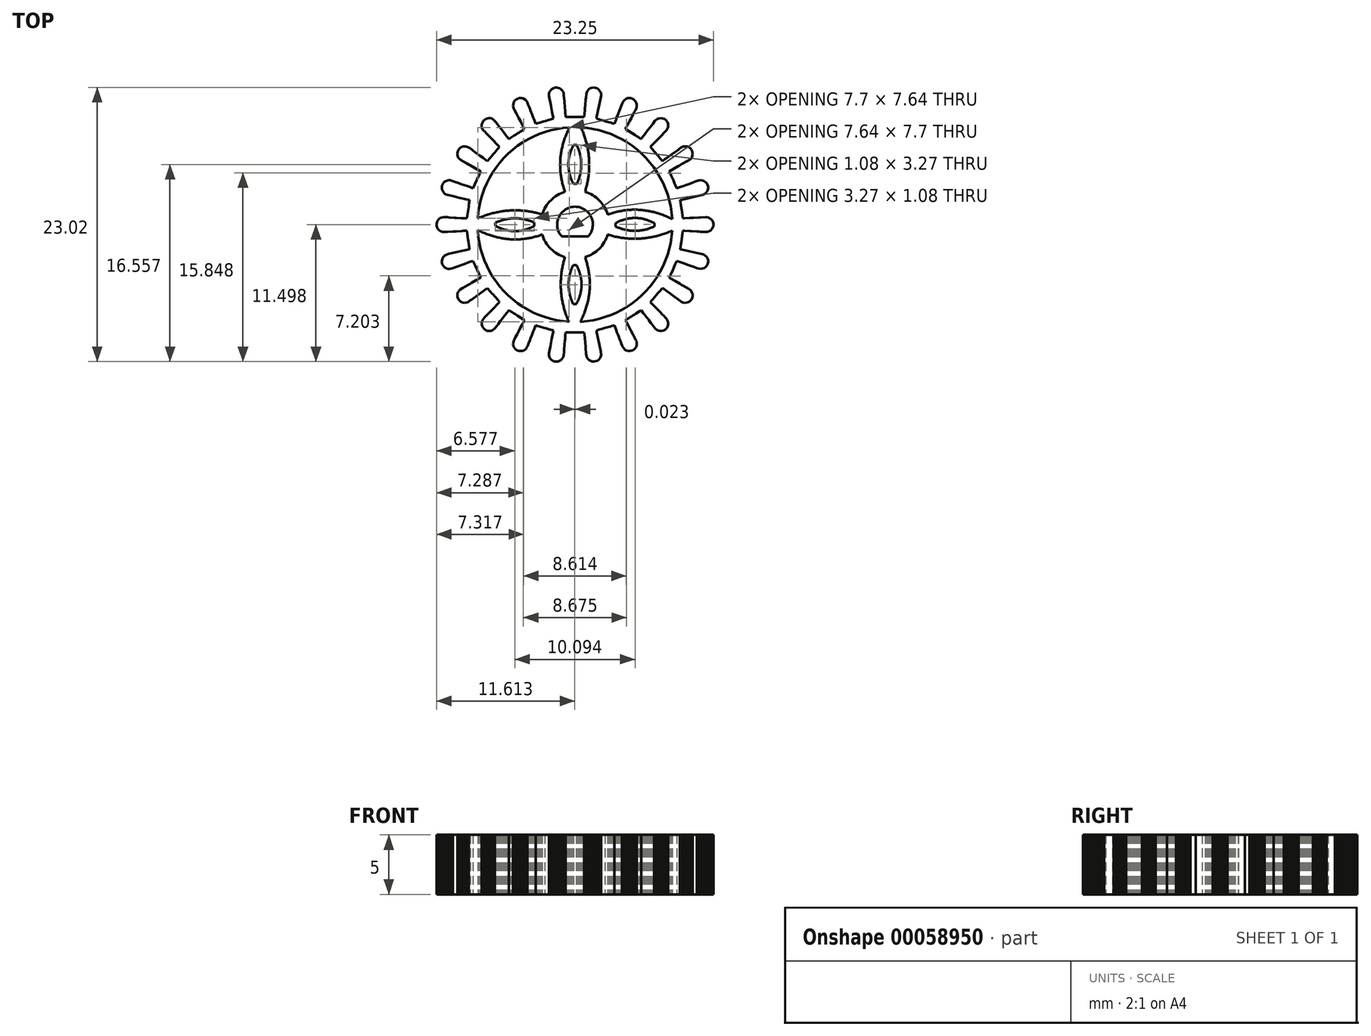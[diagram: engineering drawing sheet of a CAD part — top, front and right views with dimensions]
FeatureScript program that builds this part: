
annotation { "Feature Type Name" : "Feature", "Feature Type Description" : "" }
export const myFeature = defineFeature(function(context is Context, id is Id, definition is map)
    precondition{}
    {
        {
            var Q0;
            Q0=qCreatedBy(makeId("Top.planeOp"),FACE);
            var sketch = newSketch(context, id + "F0", { "sketchPlane" : qUnion([Q0])});
            skLineSegment(sketch, "E0", {"start": v(8.27, -0.52) * mm, "end": v(8.4, -0.52) * mm});
            skLineSegment(sketch, "E1", {"start": v(8.4, -0.52) * mm, "end": v(8.55, -0.53) * mm});
            skLineSegment(sketch, "E2", {"start": v(8.55, -0.53) * mm, "end": v(8.7, -0.54) * mm});
            skLineSegment(sketch, "E3", {"start": v(8.7, -0.54) * mm, "end": v(8.85, -0.55) * mm});
            skLineSegment(sketch, "E4", {"start": v(8.85, -0.55) * mm, "end": v(9, -0.56) * mm});
            skLineSegment(sketch, "E5", {"start": v(9, -0.56) * mm, "end": v(9.14, -0.57) * mm});
            skLineSegment(sketch, "E6", {"start": v(9.14, -0.57) * mm, "end": v(9.3, -0.57) * mm});
            skLineSegment(sketch, "E7", {"start": v(9.3, -0.57) * mm, "end": v(9.44, -0.58) * mm});
            skLineSegment(sketch, "E8", {"start": v(9.44, -0.58) * mm, "end": v(9.59, -0.6) * mm});
            skLineSegment(sketch, "E9", {"start": v(9.59, -0.6) * mm, "end": v(9.74, -0.6) * mm});
            skLineSegment(sketch, "E10", {"start": v(9.74, -0.6) * mm, "end": v(9.89, -0.6) * mm});
            skLineSegment(sketch, "E11", {"start": v(9.89, -0.6) * mm, "end": v(10.04, -0.62) * mm});
            skLineSegment(sketch, "E12", {"start": v(10.04, -0.62) * mm, "end": v(10.19, -0.63) * mm});
            skLineSegment(sketch, "E13", {"start": v(10.19, -0.63) * mm, "end": v(10.33, -0.6) * mm});
            skLineSegment(sketch, "E14", {"start": v(10.33, -0.6) * mm, "end": v(10.48, -0.56) * mm});
            skLineSegment(sketch, "E15", {"start": v(10.48, -0.56) * mm, "end": v(10.6, -0.48) * mm});
            skLineSegment(sketch, "E16", {"start": v(10.6, -0.48) * mm, "end": v(10.7, -0.37) * mm});
            skLineSegment(sketch, "E17", {"start": v(10.7, -0.37) * mm, "end": v(10.78, -0.24) * mm});
            skLineSegment(sketch, "E18", {"start": v(10.78, -0.24) * mm, "end": v(10.82, -0.1) * mm});
            skLineSegment(sketch, "E19", {"start": v(10.82, -0.1) * mm, "end": v(10.83, 0.05) * mm});
            skLineSegment(sketch, "E20", {"start": v(10.83, 0.05) * mm, "end": v(10.8, 0.2) * mm});
            skLineSegment(sketch, "E21", {"start": v(10.8, 0.2) * mm, "end": v(10.73, 0.33) * mm});
            skLineSegment(sketch, "E22", {"start": v(10.73, 0.33) * mm, "end": v(10.64, 0.45) * mm});
            skLineSegment(sketch, "E23", {"start": v(10.64, 0.45) * mm, "end": v(10.52, 0.54) * mm});
            skLineSegment(sketch, "E24", {"start": v(10.52, 0.54) * mm, "end": v(10.38, 0.6) * mm});
            skLineSegment(sketch, "E25", {"start": v(10.38, 0.6) * mm, "end": v(10.24, 0.62) * mm});
            skLineSegment(sketch, "E26", {"start": v(10.24, 0.62) * mm, "end": v(10.22, 0.62) * mm});
            skLineSegment(sketch, "E27", {"start": v(10.22, 0.62) * mm, "end": v(10.19, 0.62) * mm});
            skLineSegment(sketch, "E28", {"start": v(10.19, 0.62) * mm, "end": v(10.04, 0.62) * mm});
            skLineSegment(sketch, "E29", {"start": v(10.04, 0.62) * mm, "end": v(9.9, 0.6) * mm});
            skLineSegment(sketch, "E30", {"start": v(9.9, 0.6) * mm, "end": v(9.74, 0.6) * mm});
            skLineSegment(sketch, "E31", {"start": v(9.74, 0.6) * mm, "end": v(9.6, 0.6) * mm});
            skLineSegment(sketch, "E32", {"start": v(9.6, 0.6) * mm, "end": v(9.44, 0.58) * mm});
            skLineSegment(sketch, "E33", {"start": v(9.44, 0.58) * mm, "end": v(9.3, 0.57) * mm});
            skLineSegment(sketch, "E34", {"start": v(9.3, 0.57) * mm, "end": v(9.15, 0.57) * mm});
            skLineSegment(sketch, "E35", {"start": v(9.15, 0.57) * mm, "end": v(9, 0.56) * mm});
            skLineSegment(sketch, "E36", {"start": v(9, 0.56) * mm, "end": v(8.85, 0.55) * mm});
            skLineSegment(sketch, "E37", {"start": v(8.85, 0.55) * mm, "end": v(8.7, 0.54) * mm});
            skLineSegment(sketch, "E38", {"start": v(8.7, 0.54) * mm, "end": v(8.55, 0.53) * mm});
            skLineSegment(sketch, "E39", {"start": v(8.55, 0.53) * mm, "end": v(8.4, 0.52) * mm});
            skLineSegment(sketch, "E40", {"start": v(8.4, 0.52) * mm, "end": v(8.27, 0.52) * mm});
            skLineSegment(sketch, "E41", {"start": v(8.27, 0.52) * mm, "end": v(8.25, 0.66) * mm});
            skLineSegment(sketch, "E42", {"start": v(8.25, 0.66) * mm, "end": v(8.23, 0.8) * mm});
            skLineSegment(sketch, "E43", {"start": v(8.23, 0.8) * mm, "end": v(8.2, 0.95) * mm});
            skLineSegment(sketch, "E44", {"start": v(8.2, 0.95) * mm, "end": v(8.19, 1.1) * mm});
            skLineSegment(sketch, "E45", {"start": v(8.19, 1.1) * mm, "end": v(8.17, 1.25) * mm});
            skLineSegment(sketch, "E46", {"start": v(8.17, 1.25) * mm, "end": v(8.15, 1.4) * mm});
            skLineSegment(sketch, "E47", {"start": v(8.15, 1.4) * mm, "end": v(8.12, 1.54) * mm});
            skLineSegment(sketch, "E48", {"start": v(8.12, 1.54) * mm, "end": v(8.1, 1.69) * mm});
            skLineSegment(sketch, "E49", {"start": v(8.1, 1.69) * mm, "end": v(8.08, 1.83) * mm});
            skLineSegment(sketch, "E50", {"start": v(8.08, 1.83) * mm, "end": v(8.06, 1.98) * mm});
            skLineSegment(sketch, "E51", {"start": v(8.06, 1.98) * mm, "end": v(8.05, 2.06) * mm});
            skLineSegment(sketch, "E52", {"start": v(8.05, 2.06) * mm, "end": v(8.2, 2.1) * mm});
            skLineSegment(sketch, "E53", {"start": v(8.2, 2.1) * mm, "end": v(8.34, 2.13) * mm});
            skLineSegment(sketch, "E54", {"start": v(8.34, 2.13) * mm, "end": v(8.49, 2.16) * mm});
            skLineSegment(sketch, "E55", {"start": v(8.49, 2.16) * mm, "end": v(8.63, 2.2) * mm});
            skLineSegment(sketch, "E56", {"start": v(8.63, 2.2) * mm, "end": v(8.77, 2.23) * mm});
            skLineSegment(sketch, "E57", {"start": v(8.77, 2.23) * mm, "end": v(8.92, 2.26) * mm});
            skLineSegment(sketch, "E58", {"start": v(8.92, 2.26) * mm, "end": v(9.07, 2.3) * mm});
            skLineSegment(sketch, "E59", {"start": v(9.07, 2.3) * mm, "end": v(9.2, 2.33) * mm});
            skLineSegment(sketch, "E60", {"start": v(9.2, 2.33) * mm, "end": v(9.36, 2.36) * mm});
            skLineSegment(sketch, "E61", {"start": v(9.36, 2.36) * mm, "end": v(9.5, 2.4) * mm});
            skLineSegment(sketch, "E62", {"start": v(9.5, 2.4) * mm, "end": v(9.65, 2.43) * mm});
            skLineSegment(sketch, "E63", {"start": v(9.65, 2.43) * mm, "end": v(9.8, 2.47) * mm});
            skLineSegment(sketch, "E64", {"start": v(9.8, 2.47) * mm, "end": v(9.95, 2.5) * mm});
            skLineSegment(sketch, "E65", {"start": v(9.95, 2.5) * mm, "end": v(10.08, 2.57) * mm});
            skLineSegment(sketch, "E66", {"start": v(10.08, 2.57) * mm, "end": v(10.2, 2.66) * mm});
            skLineSegment(sketch, "E67", {"start": v(10.2, 2.66) * mm, "end": v(10.3, 2.78) * mm});
            skLineSegment(sketch, "E68", {"start": v(10.3, 2.78) * mm, "end": v(10.36, 2.91) * mm});
            skLineSegment(sketch, "E69", {"start": v(10.36, 2.91) * mm, "end": v(10.38, 3.06) * mm});
            skLineSegment(sketch, "E70", {"start": v(10.38, 3.06) * mm, "end": v(10.37, 3.21) * mm});
            skLineSegment(sketch, "E71", {"start": v(10.37, 3.21) * mm, "end": v(10.33, 3.35) * mm});
            skLineSegment(sketch, "E72", {"start": v(10.33, 3.35) * mm, "end": v(10.25, 3.48) * mm});
            skLineSegment(sketch, "E73", {"start": v(10.25, 3.48) * mm, "end": v(10.15, 3.59) * mm});
            skLineSegment(sketch, "E74", {"start": v(10.15, 3.59) * mm, "end": v(10.02, 3.67) * mm});
            skLineSegment(sketch, "E75", {"start": v(10.02, 3.67) * mm, "end": v(9.88, 3.71) * mm});
            skLineSegment(sketch, "E76", {"start": v(9.88, 3.71) * mm, "end": v(9.76, 3.72) * mm});
            skLineSegment(sketch, "E77", {"start": v(9.76, 3.72) * mm, "end": v(9.62, 3.7) * mm});
            skLineSegment(sketch, "E78", {"start": v(9.62, 3.7) * mm, "end": v(9.57, 3.7) * mm});
            skLineSegment(sketch, "E79", {"start": v(9.57, 3.7) * mm, "end": v(9.43, 3.64) * mm});
            skLineSegment(sketch, "E80", {"start": v(9.43, 3.64) * mm, "end": v(9.29, 3.6) * mm});
            skLineSegment(sketch, "E81", {"start": v(9.29, 3.6) * mm, "end": v(9.14, 3.54) * mm});
            skLineSegment(sketch, "E82", {"start": v(9.14, 3.54) * mm, "end": v(9, 3.5) * mm});
            skLineSegment(sketch, "E83", {"start": v(9, 3.5) * mm, "end": v(8.87, 3.44) * mm});
            skLineSegment(sketch, "E84", {"start": v(8.87, 3.44) * mm, "end": v(8.72, 3.4) * mm});
            skLineSegment(sketch, "E85", {"start": v(8.72, 3.4) * mm, "end": v(8.58, 3.34) * mm});
            skLineSegment(sketch, "E86", {"start": v(8.58, 3.34) * mm, "end": v(8.44, 3.3) * mm});
            skLineSegment(sketch, "E87", {"start": v(8.44, 3.3) * mm, "end": v(8.3, 3.24) * mm});
            skLineSegment(sketch, "E88", {"start": v(8.3, 3.24) * mm, "end": v(8.16, 3.2) * mm});
            skLineSegment(sketch, "E89", {"start": v(8.16, 3.2) * mm, "end": v(8.02, 3.14) * mm});
            skLineSegment(sketch, "E90", {"start": v(8.02, 3.14) * mm, "end": v(7.88, 3.1) * mm});
            skLineSegment(sketch, "E91", {"start": v(7.88, 3.1) * mm, "end": v(7.76, 3.05) * mm});
            skLineSegment(sketch, "E92", {"start": v(7.76, 3.05) * mm, "end": v(7.7, 3.18) * mm});
            skLineSegment(sketch, "E93", {"start": v(7.7, 3.18) * mm, "end": v(7.64, 3.32) * mm});
            skLineSegment(sketch, "E94", {"start": v(7.64, 3.32) * mm, "end": v(7.58, 3.45) * mm});
            skLineSegment(sketch, "E95", {"start": v(7.58, 3.45) * mm, "end": v(7.51, 3.59) * mm});
            skLineSegment(sketch, "E96", {"start": v(7.51, 3.59) * mm, "end": v(7.45, 3.72) * mm});
            skLineSegment(sketch, "E97", {"start": v(7.45, 3.72) * mm, "end": v(7.4, 3.86) * mm});
            skLineSegment(sketch, "E98", {"start": v(7.4, 3.86) * mm, "end": v(7.33, 4) * mm});
            skLineSegment(sketch, "E99", {"start": v(7.33, 4) * mm, "end": v(7.27, 4.13) * mm});
            skLineSegment(sketch, "E100", {"start": v(7.27, 4.13) * mm, "end": v(7.2, 4.26) * mm});
            skLineSegment(sketch, "E101", {"start": v(7.2, 4.26) * mm, "end": v(7.15, 4.4) * mm});
            skLineSegment(sketch, "E102", {"start": v(7.15, 4.4) * mm, "end": v(7.11, 4.47) * mm});
            skLineSegment(sketch, "E103", {"start": v(7.11, 4.47) * mm, "end": v(7.24, 4.54) * mm});
            skLineSegment(sketch, "E104", {"start": v(7.24, 4.54) * mm, "end": v(7.37, 4.61) * mm});
            skLineSegment(sketch, "E105", {"start": v(7.37, 4.61) * mm, "end": v(7.5, 4.69) * mm});
            skLineSegment(sketch, "E106", {"start": v(7.5, 4.69) * mm, "end": v(7.63, 4.76) * mm});
            skLineSegment(sketch, "E107", {"start": v(7.63, 4.76) * mm, "end": v(7.76, 4.83) * mm});
            skLineSegment(sketch, "E108", {"start": v(7.76, 4.83) * mm, "end": v(7.9, 4.9) * mm});
            skLineSegment(sketch, "E109", {"start": v(7.9, 4.9) * mm, "end": v(8.02, 4.98) * mm});
            skLineSegment(sketch, "E110", {"start": v(8.02, 4.98) * mm, "end": v(8.15, 5.05) * mm});
            skLineSegment(sketch, "E111", {"start": v(8.15, 5.05) * mm, "end": v(8.28, 5.13) * mm});
            skLineSegment(sketch, "E112", {"start": v(8.28, 5.13) * mm, "end": v(8.4, 5.2) * mm});
            skLineSegment(sketch, "E113", {"start": v(8.4, 5.2) * mm, "end": v(8.54, 5.27) * mm});
            skLineSegment(sketch, "E114", {"start": v(8.54, 5.27) * mm, "end": v(8.67, 5.35) * mm});
            skLineSegment(sketch, "E115", {"start": v(8.67, 5.35) * mm, "end": v(8.8, 5.43) * mm});
            skLineSegment(sketch, "E116", {"start": v(8.8, 5.43) * mm, "end": v(8.92, 5.53) * mm});
            skLineSegment(sketch, "E117", {"start": v(8.92, 5.53) * mm, "end": v(9, 5.65) * mm});
            skLineSegment(sketch, "E118", {"start": v(9, 5.65) * mm, "end": v(9.06, 5.79) * mm});
            skLineSegment(sketch, "E119", {"start": v(9.06, 5.79) * mm, "end": v(9.08, 5.94) * mm});
            skLineSegment(sketch, "E120", {"start": v(9.08, 5.94) * mm, "end": v(9.07, 6.08) * mm});
            skLineSegment(sketch, "E121", {"start": v(9.07, 6.08) * mm, "end": v(9.02, 6.23) * mm});
            skLineSegment(sketch, "E122", {"start": v(9.02, 6.23) * mm, "end": v(8.98, 6.28) * mm});
            skLineSegment(sketch, "E123", {"start": v(8.98, 6.28) * mm, "end": v(8.89, 6.4) * mm});
            skLineSegment(sketch, "E124", {"start": v(8.89, 6.4) * mm, "end": v(8.77, 6.49) * mm});
            skLineSegment(sketch, "E125", {"start": v(8.77, 6.49) * mm, "end": v(8.63, 6.55) * mm});
            skLineSegment(sketch, "E126", {"start": v(8.63, 6.55) * mm, "end": v(8.48, 6.57) * mm});
            skLineSegment(sketch, "E127", {"start": v(8.48, 6.57) * mm, "end": v(8.45, 6.57) * mm});
            skLineSegment(sketch, "E128", {"start": v(8.45, 6.57) * mm, "end": v(8.3, 6.55) * mm});
            skLineSegment(sketch, "E129", {"start": v(8.3, 6.55) * mm, "end": v(8.16, 6.5) * mm});
            skLineSegment(sketch, "E130", {"start": v(8.16, 6.5) * mm, "end": v(8.1, 6.46) * mm});
            skLineSegment(sketch, "E131", {"start": v(8.1, 6.46) * mm, "end": v(7.99, 6.38) * mm});
            skLineSegment(sketch, "E132", {"start": v(7.99, 6.38) * mm, "end": v(7.87, 6.29) * mm});
            skLineSegment(sketch, "E133", {"start": v(7.87, 6.29) * mm, "end": v(7.74, 6.2) * mm});
            skLineSegment(sketch, "E134", {"start": v(7.74, 6.2) * mm, "end": v(7.62, 6.11) * mm});
            skLineSegment(sketch, "E135", {"start": v(7.62, 6.11) * mm, "end": v(7.5, 6.03) * mm});
            skLineSegment(sketch, "E136", {"start": v(7.5, 6.03) * mm, "end": v(7.38, 5.94) * mm});
            skLineSegment(sketch, "E137", {"start": v(7.38, 5.94) * mm, "end": v(7.26, 5.85) * mm});
            skLineSegment(sketch, "E138", {"start": v(7.26, 5.85) * mm, "end": v(7.14, 5.76) * mm});
            skLineSegment(sketch, "E139", {"start": v(7.14, 5.76) * mm, "end": v(7.02, 5.67) * mm});
            skLineSegment(sketch, "E140", {"start": v(7.02, 5.67) * mm, "end": v(6.9, 5.59) * mm});
            skLineSegment(sketch, "E141", {"start": v(6.9, 5.59) * mm, "end": v(6.78, 5.5) * mm});
            skLineSegment(sketch, "E142", {"start": v(6.78, 5.5) * mm, "end": v(6.66, 5.41) * mm});
            skLineSegment(sketch, "E143", {"start": v(6.66, 5.41) * mm, "end": v(6.55, 5.34) * mm});
            skLineSegment(sketch, "E144", {"start": v(6.55, 5.34) * mm, "end": v(6.46, 5.45) * mm});
            skLineSegment(sketch, "E145", {"start": v(6.46, 5.45) * mm, "end": v(6.36, 5.56) * mm});
            skLineSegment(sketch, "E146", {"start": v(6.36, 5.56) * mm, "end": v(6.26, 5.67) * mm});
            skLineSegment(sketch, "E147", {"start": v(6.26, 5.67) * mm, "end": v(6.17, 5.78) * mm});
            skLineSegment(sketch, "E148", {"start": v(6.17, 5.78) * mm, "end": v(6.07, 5.9) * mm});
            skLineSegment(sketch, "E149", {"start": v(6.07, 5.9) * mm, "end": v(5.97, 6) * mm});
            skLineSegment(sketch, "E150", {"start": v(5.97, 6) * mm, "end": v(5.88, 6.12) * mm});
            skLineSegment(sketch, "E151", {"start": v(5.88, 6.12) * mm, "end": v(5.78, 6.23) * mm});
            skLineSegment(sketch, "E152", {"start": v(5.78, 6.23) * mm, "end": v(5.68, 6.34) * mm});
            skLineSegment(sketch, "E153", {"start": v(5.68, 6.34) * mm, "end": v(5.59, 6.45) * mm});
            skLineSegment(sketch, "E154", {"start": v(5.59, 6.45) * mm, "end": v(5.53, 6.52) * mm});
            skLineSegment(sketch, "E155", {"start": v(5.53, 6.52) * mm, "end": v(5.64, 6.62) * mm});
            skLineSegment(sketch, "E156", {"start": v(5.64, 6.62) * mm, "end": v(5.74, 6.73) * mm});
            skLineSegment(sketch, "E157", {"start": v(5.74, 6.73) * mm, "end": v(5.84, 6.84) * mm});
            skLineSegment(sketch, "E158", {"start": v(5.84, 6.84) * mm, "end": v(5.95, 6.94) * mm});
            skLineSegment(sketch, "E159", {"start": v(5.95, 6.94) * mm, "end": v(6.05, 7.05) * mm});
            skLineSegment(sketch, "E160", {"start": v(6.05, 7.05) * mm, "end": v(6.16, 7.16) * mm});
            skLineSegment(sketch, "E161", {"start": v(6.16, 7.16) * mm, "end": v(6.26, 7.26) * mm});
            skLineSegment(sketch, "E162", {"start": v(6.26, 7.26) * mm, "end": v(6.36, 7.37) * mm});
            skLineSegment(sketch, "E163", {"start": v(6.36, 7.37) * mm, "end": v(6.47, 7.48) * mm});
            skLineSegment(sketch, "E164", {"start": v(6.47, 7.48) * mm, "end": v(6.57, 7.58) * mm});
            skLineSegment(sketch, "E165", {"start": v(6.57, 7.58) * mm, "end": v(6.67, 7.69) * mm});
            skLineSegment(sketch, "E166", {"start": v(6.67, 7.69) * mm, "end": v(6.78, 7.8) * mm});
            skLineSegment(sketch, "E167", {"start": v(6.78, 7.8) * mm, "end": v(6.9, 7.92) * mm});
            skLineSegment(sketch, "E168", {"start": v(6.9, 7.92) * mm, "end": v(6.97, 8.04) * mm});
            skLineSegment(sketch, "E169", {"start": v(6.97, 8.04) * mm, "end": v(7.02, 8.18) * mm});
            skLineSegment(sketch, "E170", {"start": v(7.02, 8.18) * mm, "end": v(7.03, 8.33) * mm});
            skLineSegment(sketch, "E171", {"start": v(7.03, 8.33) * mm, "end": v(7.01, 8.48) * mm});
            skLineSegment(sketch, "E172", {"start": v(7.01, 8.48) * mm, "end": v(6.95, 8.62) * mm});
            skLineSegment(sketch, "E173", {"start": v(6.95, 8.62) * mm, "end": v(6.86, 8.74) * mm});
            skLineSegment(sketch, "E174", {"start": v(6.86, 8.74) * mm, "end": v(6.82, 8.79) * mm});
            skLineSegment(sketch, "E175", {"start": v(6.82, 8.79) * mm, "end": v(6.7, 8.87) * mm});
            skLineSegment(sketch, "E176", {"start": v(6.7, 8.87) * mm, "end": v(6.55, 8.92) * mm});
            skLineSegment(sketch, "E177", {"start": v(6.55, 8.92) * mm, "end": v(6.42, 8.94) * mm});
            skLineSegment(sketch, "E178", {"start": v(6.42, 8.94) * mm, "end": v(6.27, 8.92) * mm});
            skLineSegment(sketch, "E179", {"start": v(6.27, 8.92) * mm, "end": v(6.13, 8.87) * mm});
            skLineSegment(sketch, "E180", {"start": v(6.13, 8.87) * mm, "end": v(6, 8.8) * mm});
            skLineSegment(sketch, "E181", {"start": v(6, 8.8) * mm, "end": v(5.92, 8.7) * mm});
            skLineSegment(sketch, "E182", {"start": v(5.92, 8.7) * mm, "end": v(5.83, 8.6) * mm});
            skLineSegment(sketch, "E183", {"start": v(5.83, 8.6) * mm, "end": v(5.74, 8.47) * mm});
            skLineSegment(sketch, "E184", {"start": v(5.74, 8.47) * mm, "end": v(5.65, 8.35) * mm});
            skLineSegment(sketch, "E185", {"start": v(5.65, 8.35) * mm, "end": v(5.56, 8.24) * mm});
            skLineSegment(sketch, "E186", {"start": v(5.56, 8.24) * mm, "end": v(5.47, 8.12) * mm});
            skLineSegment(sketch, "E187", {"start": v(5.47, 8.12) * mm, "end": v(5.38, 8) * mm});
            skLineSegment(sketch, "E188", {"start": v(5.38, 8) * mm, "end": v(5.29, 7.88) * mm});
            skLineSegment(sketch, "E189", {"start": v(5.29, 7.88) * mm, "end": v(5.2, 7.77) * mm});
            skLineSegment(sketch, "E190", {"start": v(5.2, 7.77) * mm, "end": v(5.1, 7.65) * mm});
            skLineSegment(sketch, "E191", {"start": v(5.1, 7.65) * mm, "end": v(5.01, 7.53) * mm});
            skLineSegment(sketch, "E192", {"start": v(5.01, 7.53) * mm, "end": v(4.92, 7.41) * mm});
            skLineSegment(sketch, "E193", {"start": v(4.92, 7.41) * mm, "end": v(4.83, 7.3) * mm});
            skLineSegment(sketch, "E194", {"start": v(4.83, 7.3) * mm, "end": v(4.75, 7.2) * mm});
            skLineSegment(sketch, "E195", {"start": v(4.75, 7.2) * mm, "end": v(4.63, 7.27) * mm});
            skLineSegment(sketch, "E196", {"start": v(4.63, 7.27) * mm, "end": v(4.5, 7.35) * mm});
            skLineSegment(sketch, "E197", {"start": v(4.5, 7.35) * mm, "end": v(4.38, 7.43) * mm});
            skLineSegment(sketch, "E198", {"start": v(4.38, 7.43) * mm, "end": v(4.25, 7.51) * mm});
            skLineSegment(sketch, "E199", {"start": v(4.25, 7.51) * mm, "end": v(4.13, 7.6) * mm});
            skLineSegment(sketch, "E200", {"start": v(4.13, 7.6) * mm, "end": v(4, 7.67) * mm});
            skLineSegment(sketch, "E201", {"start": v(4, 7.67) * mm, "end": v(3.88, 7.75) * mm});
            skLineSegment(sketch, "E202", {"start": v(3.88, 7.75) * mm, "end": v(3.76, 7.83) * mm});
            skLineSegment(sketch, "E203", {"start": v(3.76, 7.83) * mm, "end": v(3.63, 7.91) * mm});
            skLineSegment(sketch, "E204", {"start": v(3.63, 7.91) * mm, "end": v(3.5, 8) * mm});
            skLineSegment(sketch, "E205", {"start": v(3.5, 8) * mm, "end": v(3.44, 8.03) * mm});
            skLineSegment(sketch, "E206", {"start": v(3.44, 8.03) * mm, "end": v(3.5, 8.16) * mm});
            skLineSegment(sketch, "E207", {"start": v(3.5, 8.16) * mm, "end": v(3.58, 8.3) * mm});
            skLineSegment(sketch, "E208", {"start": v(3.58, 8.3) * mm, "end": v(3.65, 8.43) * mm});
            skLineSegment(sketch, "E209", {"start": v(3.65, 8.43) * mm, "end": v(3.72, 8.56) * mm});
            skLineSegment(sketch, "E210", {"start": v(3.72, 8.56) * mm, "end": v(3.79, 8.7) * mm});
            skLineSegment(sketch, "E211", {"start": v(3.79, 8.7) * mm, "end": v(3.86, 8.83) * mm});
            skLineSegment(sketch, "E212", {"start": v(3.86, 8.83) * mm, "end": v(3.93, 8.96) * mm});
            skLineSegment(sketch, "E213", {"start": v(3.93, 8.96) * mm, "end": v(4, 9.09) * mm});
            skLineSegment(sketch, "E214", {"start": v(4, 9.09) * mm, "end": v(4.07, 9.22) * mm});
            skLineSegment(sketch, "E215", {"start": v(4.07, 9.22) * mm, "end": v(4.14, 9.35) * mm});
            skLineSegment(sketch, "E216", {"start": v(4.14, 9.35) * mm, "end": v(4.2, 9.48) * mm});
            skLineSegment(sketch, "E217", {"start": v(4.2, 9.48) * mm, "end": v(4.28, 9.62) * mm});
            skLineSegment(sketch, "E218", {"start": v(4.28, 9.62) * mm, "end": v(4.35, 9.76) * mm});
            skLineSegment(sketch, "E219", {"start": v(4.35, 9.76) * mm, "end": v(4.39, 9.9) * mm});
            skLineSegment(sketch, "E220", {"start": v(4.39, 9.9) * mm, "end": v(4.4, 10.05) * mm});
            skLineSegment(sketch, "E221", {"start": v(4.4, 10.05) * mm, "end": v(4.37, 10.2) * mm});
            skLineSegment(sketch, "E222", {"start": v(4.37, 10.2) * mm, "end": v(4.3, 10.34) * mm});
            skLineSegment(sketch, "E223", {"start": v(4.3, 10.34) * mm, "end": v(4.21, 10.45) * mm});
            skLineSegment(sketch, "E224", {"start": v(4.21, 10.45) * mm, "end": v(4.1, 10.54) * mm});
            skLineSegment(sketch, "E225", {"start": v(4.1, 10.54) * mm, "end": v(4.03, 10.57) * mm});
            skLineSegment(sketch, "E226", {"start": v(4.03, 10.57) * mm, "end": v(3.9, 10.62) * mm});
            skLineSegment(sketch, "E227", {"start": v(3.9, 10.62) * mm, "end": v(3.77, 10.63) * mm});
            skLineSegment(sketch, "E228", {"start": v(3.77, 10.63) * mm, "end": v(3.63, 10.61) * mm});
            skLineSegment(sketch, "E229", {"start": v(3.63, 10.61) * mm, "end": v(3.49, 10.56) * mm});
            skLineSegment(sketch, "E230", {"start": v(3.49, 10.56) * mm, "end": v(3.37, 10.48) * mm});
            skLineSegment(sketch, "E231", {"start": v(3.37, 10.48) * mm, "end": v(3.26, 10.37) * mm});
            skLineSegment(sketch, "E232", {"start": v(3.26, 10.37) * mm, "end": v(3.2, 10.25) * mm});
            skLineSegment(sketch, "E233", {"start": v(3.2, 10.25) * mm, "end": v(3.14, 10.11) * mm});
            skLineSegment(sketch, "E234", {"start": v(3.14, 10.11) * mm, "end": v(3.1, 9.97) * mm});
            skLineSegment(sketch, "E235", {"start": v(3.1, 9.97) * mm, "end": v(3.04, 9.83) * mm});
            skLineSegment(sketch, "E236", {"start": v(3.04, 9.83) * mm, "end": v(2.98, 9.7) * mm});
            skLineSegment(sketch, "E237", {"start": v(2.98, 9.7) * mm, "end": v(2.93, 9.56) * mm});
            skLineSegment(sketch, "E238", {"start": v(2.93, 9.56) * mm, "end": v(2.87, 9.42) * mm});
            skLineSegment(sketch, "E239", {"start": v(2.87, 9.42) * mm, "end": v(2.82, 9.28) * mm});
            skLineSegment(sketch, "E240", {"start": v(2.82, 9.28) * mm, "end": v(2.77, 9.14) * mm});
            skLineSegment(sketch, "E241", {"start": v(2.77, 9.14) * mm, "end": v(2.71, 9) * mm});
            skLineSegment(sketch, "E242", {"start": v(2.71, 9) * mm, "end": v(2.66, 8.86) * mm});
            skLineSegment(sketch, "E243", {"start": v(2.66, 8.86) * mm, "end": v(2.6, 8.72) * mm});
            skLineSegment(sketch, "E244", {"start": v(2.6, 8.72) * mm, "end": v(2.55, 8.58) * mm});
            skLineSegment(sketch, "E245", {"start": v(2.55, 8.58) * mm, "end": v(2.5, 8.46) * mm});
            skLineSegment(sketch, "E246", {"start": v(2.5, 8.46) * mm, "end": v(2.36, 8.5) * mm});
            skLineSegment(sketch, "E247", {"start": v(2.36, 8.5) * mm, "end": v(2.22, 8.55) * mm});
            skLineSegment(sketch, "E248", {"start": v(2.22, 8.55) * mm, "end": v(2.08, 8.59) * mm});
            skLineSegment(sketch, "E249", {"start": v(2.08, 8.59) * mm, "end": v(1.93, 8.63) * mm});
            skLineSegment(sketch, "E250", {"start": v(1.93, 8.63) * mm, "end": v(1.8, 8.67) * mm});
            skLineSegment(sketch, "E251", {"start": v(1.8, 8.67) * mm, "end": v(1.65, 8.71) * mm});
            skLineSegment(sketch, "E252", {"start": v(1.65, 8.71) * mm, "end": v(1.5, 8.75) * mm});
            skLineSegment(sketch, "E253", {"start": v(1.5, 8.75) * mm, "end": v(1.37, 8.8) * mm});
            skLineSegment(sketch, "E254", {"start": v(1.37, 8.8) * mm, "end": v(1.22, 8.84) * mm});
            skLineSegment(sketch, "E255", {"start": v(1.22, 8.84) * mm, "end": v(1.08, 8.88) * mm});
            skLineSegment(sketch, "E256", {"start": v(1.08, 8.88) * mm, "end": v(1, 8.9) * mm});
            skLineSegment(sketch, "E257", {"start": v(1, 8.9) * mm, "end": v(1.03, 9.05) * mm});
            skLineSegment(sketch, "E258", {"start": v(1.03, 9.05) * mm, "end": v(1.06, 9.2) * mm});
            skLineSegment(sketch, "E259", {"start": v(1.06, 9.2) * mm, "end": v(1.1, 9.34) * mm});
            skLineSegment(sketch, "E260", {"start": v(1.1, 9.34) * mm, "end": v(1.12, 9.49) * mm});
            skLineSegment(sketch, "E261", {"start": v(1.12, 9.49) * mm, "end": v(1.15, 9.63) * mm});
            skLineSegment(sketch, "E262", {"start": v(1.15, 9.63) * mm, "end": v(1.18, 9.78) * mm});
            skLineSegment(sketch, "E263", {"start": v(1.18, 9.78) * mm, "end": v(1.21, 9.92) * mm});
            skLineSegment(sketch, "E264", {"start": v(1.21, 9.92) * mm, "end": v(1.24, 10.07) * mm});
            skLineSegment(sketch, "E265", {"start": v(1.24, 10.07) * mm, "end": v(1.27, 10.22) * mm});
            skLineSegment(sketch, "E266", {"start": v(1.27, 10.22) * mm, "end": v(1.3, 10.36) * mm});
            skLineSegment(sketch, "E267", {"start": v(1.3, 10.36) * mm, "end": v(1.33, 10.5) * mm});
            skLineSegment(sketch, "E268", {"start": v(1.33, 10.5) * mm, "end": v(1.36, 10.66) * mm});
            skLineSegment(sketch, "E269", {"start": v(1.36, 10.66) * mm, "end": v(1.4, 10.81) * mm});
            skLineSegment(sketch, "E270", {"start": v(1.4, 10.81) * mm, "end": v(1.39, 10.96) * mm});
            skLineSegment(sketch, "E271", {"start": v(1.39, 10.96) * mm, "end": v(1.35, 11.1) * mm});
            skLineSegment(sketch, "E272", {"start": v(1.35, 11.1) * mm, "end": v(1.28, 11.24) * mm});
            skLineSegment(sketch, "E273", {"start": v(1.28, 11.24) * mm, "end": v(1.19, 11.35) * mm});
            skLineSegment(sketch, "E274", {"start": v(1.19, 11.35) * mm, "end": v(1.06, 11.44) * mm});
            skLineSegment(sketch, "E275", {"start": v(1.06, 11.44) * mm, "end": v(0.92, 11.5) * mm});
            skLineSegment(sketch, "E276", {"start": v(0.92, 11.5) * mm, "end": v(0.78, 11.51) * mm});
            skLineSegment(sketch, "E277", {"start": v(0.78, 11.51) * mm, "end": v(0.76, 11.51) * mm});
            skLineSegment(sketch, "E278", {"start": v(0.76, 11.51) * mm, "end": v(0.61, 11.5) * mm});
            skLineSegment(sketch, "E279", {"start": v(0.61, 11.5) * mm, "end": v(0.47, 11.44) * mm});
            skLineSegment(sketch, "E280", {"start": v(0.47, 11.44) * mm, "end": v(0.35, 11.35) * mm});
            skLineSegment(sketch, "E281", {"start": v(0.35, 11.35) * mm, "end": v(0.25, 11.24) * mm});
            skLineSegment(sketch, "E282", {"start": v(0.25, 11.24) * mm, "end": v(0.19, 11.1) * mm});
            skLineSegment(sketch, "E283", {"start": v(0.19, 11.1) * mm, "end": v(0.15, 10.96) * mm});
            skLineSegment(sketch, "E284", {"start": v(0.15, 10.96) * mm, "end": v(0.14, 10.81) * mm});
            skLineSegment(sketch, "E285", {"start": v(0.14, 10.81) * mm, "end": v(0.12, 10.66) * mm});
            skLineSegment(sketch, "E286", {"start": v(0.12, 10.66) * mm, "end": v(0.11, 10.51) * mm});
            skLineSegment(sketch, "E287", {"start": v(0.11, 10.51) * mm, "end": v(0.1, 10.37) * mm});
            skLineSegment(sketch, "E288", {"start": v(0.1, 10.37) * mm, "end": v(0.08, 10.22) * mm});
            skLineSegment(sketch, "E289", {"start": v(0.08, 10.22) * mm, "end": v(0.07, 10.07) * mm});
            skLineSegment(sketch, "E290", {"start": v(0.07, 10.07) * mm, "end": v(0.06, 9.92) * mm});
            skLineSegment(sketch, "E291", {"start": v(0.06, 9.92) * mm, "end": v(0.05, 9.77) * mm});
            skLineSegment(sketch, "E292", {"start": v(0.05, 9.77) * mm, "end": v(0.03, 9.62) * mm});
            skLineSegment(sketch, "E293", {"start": v(0.03, 9.62) * mm, "end": v(0.02, 9.47) * mm});
            skLineSegment(sketch, "E294", {"start": v(0.02, 9.47) * mm, "end": v(0, 9.33) * mm});
            skLineSegment(sketch, "E295", {"start": v(0, 9.33) * mm, "end": v(0, 9.18) * mm});
            skLineSegment(sketch, "E296", {"start": v(0, 9.18) * mm, "end": v(-0.02, 9.05) * mm});
            skLineSegment(sketch, "E297", {"start": v(-0.02, 9.05) * mm, "end": v(-0.16, 9.05) * mm});
            skLineSegment(sketch, "E298", {"start": v(-0.16, 9.05) * mm, "end": v(-0.31, 9.05) * mm});
            skLineSegment(sketch, "E299", {"start": v(-0.31, 9.05) * mm, "end": v(-0.46, 9.05) * mm});
            skLineSegment(sketch, "E300", {"start": v(-0.46, 9.05) * mm, "end": v(-0.6, 9.05) * mm});
            skLineSegment(sketch, "E301", {"start": v(-0.6, 9.05) * mm, "end": v(-0.76, 9.05) * mm});
            skLineSegment(sketch, "E302", {"start": v(-0.76, 9.05) * mm, "end": v(-0.9, 9.05) * mm});
            skLineSegment(sketch, "E303", {"start": v(-0.9, 9.05) * mm, "end": v(-1.05, 9.05) * mm});
            skLineSegment(sketch, "E304", {"start": v(-1.05, 9.05) * mm, "end": v(-1.2, 9.05) * mm});
            skLineSegment(sketch, "E305", {"start": v(-1.2, 9.05) * mm, "end": v(-1.35, 9.05) * mm});
            skLineSegment(sketch, "E306", {"start": v(-1.35, 9.05) * mm, "end": v(-1.5, 9.05) * mm});
            skLineSegment(sketch, "E307", {"start": v(-1.5, 9.05) * mm, "end": v(-1.58, 9.05) * mm});
            skLineSegment(sketch, "E308", {"start": v(-1.58, 9.05) * mm, "end": v(-1.59, 9.2) * mm});
            skLineSegment(sketch, "E309", {"start": v(-1.59, 9.2) * mm, "end": v(-1.6, 9.34) * mm});
            skLineSegment(sketch, "E310", {"start": v(-1.6, 9.34) * mm, "end": v(-1.61, 9.5) * mm});
            skLineSegment(sketch, "E311", {"start": v(-1.61, 9.5) * mm, "end": v(-1.63, 9.64) * mm});
            skLineSegment(sketch, "E312", {"start": v(-1.63, 9.64) * mm, "end": v(-1.64, 9.79) * mm});
            skLineSegment(sketch, "E313", {"start": v(-1.64, 9.79) * mm, "end": v(-1.65, 9.94) * mm});
            skLineSegment(sketch, "E314", {"start": v(-1.65, 9.94) * mm, "end": v(-1.67, 10.09) * mm});
            skLineSegment(sketch, "E315", {"start": v(-1.67, 10.09) * mm, "end": v(-1.68, 10.24) * mm});
            skLineSegment(sketch, "E316", {"start": v(-1.68, 10.24) * mm, "end": v(-1.7, 10.39) * mm});
            skLineSegment(sketch, "E317", {"start": v(-1.7, 10.39) * mm, "end": v(-1.7, 10.53) * mm});
            skLineSegment(sketch, "E318", {"start": v(-1.7, 10.53) * mm, "end": v(-1.72, 10.68) * mm});
            skLineSegment(sketch, "E319", {"start": v(-1.72, 10.68) * mm, "end": v(-1.73, 10.83) * mm});
            skLineSegment(sketch, "E320", {"start": v(-1.73, 10.83) * mm, "end": v(-1.74, 11) * mm});
            skLineSegment(sketch, "E321", {"start": v(-1.74, 11) * mm, "end": v(-1.79, 11.13) * mm});
            skLineSegment(sketch, "E322", {"start": v(-1.79, 11.13) * mm, "end": v(-1.86, 11.26) * mm});
            skLineSegment(sketch, "E323", {"start": v(-1.86, 11.26) * mm, "end": v(-1.97, 11.37) * mm});
            skLineSegment(sketch, "E324", {"start": v(-1.97, 11.37) * mm, "end": v(-2.1, 11.45) * mm});
            skLineSegment(sketch, "E325", {"start": v(-2.1, 11.45) * mm, "end": v(-2.23, 11.5) * mm});
            skLineSegment(sketch, "E326", {"start": v(-2.23, 11.5) * mm, "end": v(-2.35, 11.51) * mm});
            skLineSegment(sketch, "E327", {"start": v(-2.35, 11.51) * mm, "end": v(-2.45, 11.5) * mm});
            skLineSegment(sketch, "E328", {"start": v(-2.45, 11.5) * mm, "end": v(-2.6, 11.47) * mm});
            skLineSegment(sketch, "E329", {"start": v(-2.6, 11.47) * mm, "end": v(-2.73, 11.4) * mm});
            skLineSegment(sketch, "E330", {"start": v(-2.73, 11.4) * mm, "end": v(-2.83, 11.3) * mm});
            skLineSegment(sketch, "E331", {"start": v(-2.83, 11.3) * mm, "end": v(-2.92, 11.17) * mm});
            skLineSegment(sketch, "E332", {"start": v(-2.92, 11.17) * mm, "end": v(-2.97, 11.03) * mm});
            skLineSegment(sketch, "E333", {"start": v(-2.97, 11.03) * mm, "end": v(-2.99, 10.88) * mm});
            skLineSegment(sketch, "E334", {"start": v(-2.99, 10.88) * mm, "end": v(-2.98, 10.78) * mm});
            skLineSegment(sketch, "E335", {"start": v(-2.98, 10.78) * mm, "end": v(-2.95, 10.64) * mm});
            skLineSegment(sketch, "E336", {"start": v(-2.95, 10.64) * mm, "end": v(-2.92, 10.5) * mm});
            skLineSegment(sketch, "E337", {"start": v(-2.92, 10.5) * mm, "end": v(-2.89, 10.34) * mm});
            skLineSegment(sketch, "E338", {"start": v(-2.89, 10.34) * mm, "end": v(-2.86, 10.2) * mm});
            skLineSegment(sketch, "E339", {"start": v(-2.86, 10.2) * mm, "end": v(-2.83, 10.05) * mm});
            skLineSegment(sketch, "E340", {"start": v(-2.83, 10.05) * mm, "end": v(-2.8, 9.9) * mm});
            skLineSegment(sketch, "E341", {"start": v(-2.8, 9.9) * mm, "end": v(-2.77, 9.76) * mm});
            skLineSegment(sketch, "E342", {"start": v(-2.77, 9.76) * mm, "end": v(-2.74, 9.61) * mm});
            skLineSegment(sketch, "E343", {"start": v(-2.74, 9.61) * mm, "end": v(-2.71, 9.47) * mm});
            skLineSegment(sketch, "E344", {"start": v(-2.71, 9.47) * mm, "end": v(-2.68, 9.32) * mm});
            skLineSegment(sketch, "E345", {"start": v(-2.68, 9.32) * mm, "end": v(-2.65, 9.18) * mm});
            skLineSegment(sketch, "E346", {"start": v(-2.65, 9.18) * mm, "end": v(-2.62, 9.03) * mm});
            skLineSegment(sketch, "E347", {"start": v(-2.62, 9.03) * mm, "end": v(-2.6, 8.9) * mm});
            skLineSegment(sketch, "E348", {"start": v(-2.6, 8.9) * mm, "end": v(-2.74, 8.86) * mm});
            skLineSegment(sketch, "E349", {"start": v(-2.74, 8.86) * mm, "end": v(-2.88, 8.82) * mm});
            skLineSegment(sketch, "E350", {"start": v(-2.88, 8.82) * mm, "end": v(-3.02, 8.78) * mm});
            skLineSegment(sketch, "E351", {"start": v(-3.02, 8.78) * mm, "end": v(-3.16, 8.74) * mm});
            skLineSegment(sketch, "E352", {"start": v(-3.16, 8.74) * mm, "end": v(-3.3, 8.7) * mm});
            skLineSegment(sketch, "E353", {"start": v(-3.3, 8.7) * mm, "end": v(-3.45, 8.65) * mm});
            skLineSegment(sketch, "E354", {"start": v(-3.45, 8.65) * mm, "end": v(-3.6, 8.61) * mm});
            skLineSegment(sketch, "E355", {"start": v(-3.6, 8.61) * mm, "end": v(-3.73, 8.57) * mm});
            skLineSegment(sketch, "E356", {"start": v(-3.73, 8.57) * mm, "end": v(-3.87, 8.53) * mm});
            skLineSegment(sketch, "E357", {"start": v(-3.87, 8.53) * mm, "end": v(-4.02, 8.49) * mm});
            skLineSegment(sketch, "E358", {"start": v(-4.02, 8.49) * mm, "end": v(-4.1, 8.46) * mm});
            skLineSegment(sketch, "E359", {"start": v(-4.1, 8.46) * mm, "end": v(-4.15, 8.6) * mm});
            skLineSegment(sketch, "E360", {"start": v(-4.15, 8.6) * mm, "end": v(-4.2, 8.74) * mm});
            skLineSegment(sketch, "E361", {"start": v(-4.2, 8.74) * mm, "end": v(-4.26, 8.88) * mm});
            skLineSegment(sketch, "E362", {"start": v(-4.26, 8.88) * mm, "end": v(-4.3, 9.02) * mm});
            skLineSegment(sketch, "E363", {"start": v(-4.3, 9.02) * mm, "end": v(-4.36, 9.16) * mm});
            skLineSegment(sketch, "E364", {"start": v(-4.36, 9.16) * mm, "end": v(-4.42, 9.3) * mm});
            skLineSegment(sketch, "E365", {"start": v(-4.42, 9.3) * mm, "end": v(-4.47, 9.43) * mm});
            skLineSegment(sketch, "E366", {"start": v(-4.47, 9.43) * mm, "end": v(-4.53, 9.57) * mm});
            skLineSegment(sketch, "E367", {"start": v(-4.53, 9.57) * mm, "end": v(-4.58, 9.71) * mm});
            skLineSegment(sketch, "E368", {"start": v(-4.58, 9.71) * mm, "end": v(-4.63, 9.85) * mm});
            skLineSegment(sketch, "E369", {"start": v(-4.63, 9.85) * mm, "end": v(-4.69, 9.99) * mm});
            skLineSegment(sketch, "E370", {"start": v(-4.69, 9.99) * mm, "end": v(-4.74, 10.13) * mm});
            skLineSegment(sketch, "E371", {"start": v(-4.74, 10.13) * mm, "end": v(-4.8, 10.28) * mm});
            skLineSegment(sketch, "E372", {"start": v(-4.8, 10.28) * mm, "end": v(-4.89, 10.4) * mm});
            skLineSegment(sketch, "E373", {"start": v(-4.89, 10.4) * mm, "end": v(-5, 10.5) * mm});
            skLineSegment(sketch, "E374", {"start": v(-5, 10.5) * mm, "end": v(-5.12, 10.58) * mm});
            skLineSegment(sketch, "E375", {"start": v(-5.12, 10.58) * mm, "end": v(-5.27, 10.62) * mm});
            skLineSegment(sketch, "E376", {"start": v(-5.27, 10.62) * mm, "end": v(-5.37, 10.63) * mm});
            skLineSegment(sketch, "E377", {"start": v(-5.37, 10.63) * mm, "end": v(-5.51, 10.61) * mm});
            skLineSegment(sketch, "E378", {"start": v(-5.51, 10.61) * mm, "end": v(-5.62, 10.57) * mm});
            skLineSegment(sketch, "E379", {"start": v(-5.62, 10.57) * mm, "end": v(-5.75, 10.5) * mm});
            skLineSegment(sketch, "E380", {"start": v(-5.75, 10.5) * mm, "end": v(-5.86, 10.4) * mm});
            skLineSegment(sketch, "E381", {"start": v(-5.86, 10.4) * mm, "end": v(-5.93, 10.26) * mm});
            skLineSegment(sketch, "E382", {"start": v(-5.93, 10.26) * mm, "end": v(-5.98, 10.12) * mm});
            skLineSegment(sketch, "E383", {"start": v(-5.98, 10.12) * mm, "end": v(-5.99, 9.97) * mm});
            skLineSegment(sketch, "E384", {"start": v(-5.99, 9.97) * mm, "end": v(-5.96, 9.82) * mm});
            skLineSegment(sketch, "E385", {"start": v(-5.96, 9.82) * mm, "end": v(-5.93, 9.73) * mm});
            skLineSegment(sketch, "E386", {"start": v(-5.93, 9.73) * mm, "end": v(-5.86, 9.6) * mm});
            skLineSegment(sketch, "E387", {"start": v(-5.86, 9.6) * mm, "end": v(-5.79, 9.47) * mm});
            skLineSegment(sketch, "E388", {"start": v(-5.79, 9.47) * mm, "end": v(-5.72, 9.33) * mm});
            skLineSegment(sketch, "E389", {"start": v(-5.72, 9.33) * mm, "end": v(-5.65, 9.2) * mm});
            skLineSegment(sketch, "E390", {"start": v(-5.65, 9.2) * mm, "end": v(-5.58, 9.07) * mm});
            skLineSegment(sketch, "E391", {"start": v(-5.58, 9.07) * mm, "end": v(-5.5, 8.94) * mm});
            skLineSegment(sketch, "E392", {"start": v(-5.5, 8.94) * mm, "end": v(-5.44, 8.8) * mm});
            skLineSegment(sketch, "E393", {"start": v(-5.44, 8.8) * mm, "end": v(-5.37, 8.68) * mm});
            skLineSegment(sketch, "E394", {"start": v(-5.37, 8.68) * mm, "end": v(-5.3, 8.54) * mm});
            skLineSegment(sketch, "E395", {"start": v(-5.3, 8.54) * mm, "end": v(-5.23, 8.41) * mm});
            skLineSegment(sketch, "E396", {"start": v(-5.23, 8.41) * mm, "end": v(-5.16, 8.28) * mm});
            skLineSegment(sketch, "E397", {"start": v(-5.16, 8.28) * mm, "end": v(-5.1, 8.15) * mm});
            skLineSegment(sketch, "E398", {"start": v(-5.1, 8.15) * mm, "end": v(-5.03, 8.03) * mm});
            skLineSegment(sketch, "E399", {"start": v(-5.03, 8.03) * mm, "end": v(-5.16, 7.95) * mm});
            skLineSegment(sketch, "E400", {"start": v(-5.16, 7.95) * mm, "end": v(-5.28, 7.87) * mm});
            skLineSegment(sketch, "E401", {"start": v(-5.28, 7.87) * mm, "end": v(-5.4, 7.8) * mm});
            skLineSegment(sketch, "E402", {"start": v(-5.4, 7.8) * mm, "end": v(-5.53, 7.71) * mm});
            skLineSegment(sketch, "E403", {"start": v(-5.53, 7.71) * mm, "end": v(-5.65, 7.63) * mm});
            skLineSegment(sketch, "E404", {"start": v(-5.65, 7.63) * mm, "end": v(-5.78, 7.55) * mm});
            skLineSegment(sketch, "E405", {"start": v(-5.78, 7.55) * mm, "end": v(-5.9, 7.47) * mm});
            skLineSegment(sketch, "E406", {"start": v(-5.9, 7.47) * mm, "end": v(-6.03, 7.4) * mm});
            skLineSegment(sketch, "E407", {"start": v(-6.03, 7.4) * mm, "end": v(-6.15, 7.31) * mm});
            skLineSegment(sketch, "E408", {"start": v(-6.15, 7.31) * mm, "end": v(-6.28, 7.23) * mm});
            skLineSegment(sketch, "E409", {"start": v(-6.28, 7.23) * mm, "end": v(-6.34, 7.2) * mm});
            skLineSegment(sketch, "E410", {"start": v(-6.34, 7.2) * mm, "end": v(-6.43, 7.3) * mm});
            skLineSegment(sketch, "E411", {"start": v(-6.43, 7.3) * mm, "end": v(-6.52, 7.43) * mm});
            skLineSegment(sketch, "E412", {"start": v(-6.52, 7.43) * mm, "end": v(-6.62, 7.55) * mm});
            skLineSegment(sketch, "E413", {"start": v(-6.62, 7.55) * mm, "end": v(-6.7, 7.66) * mm});
            skLineSegment(sketch, "E414", {"start": v(-6.7, 7.66) * mm, "end": v(-6.8, 7.78) * mm});
            skLineSegment(sketch, "E415", {"start": v(-6.8, 7.78) * mm, "end": v(-6.9, 7.9) * mm});
            skLineSegment(sketch, "E416", {"start": v(-6.9, 7.9) * mm, "end": v(-6.98, 8.02) * mm});
            skLineSegment(sketch, "E417", {"start": v(-6.98, 8.02) * mm, "end": v(-7.07, 8.13) * mm});
            skLineSegment(sketch, "E418", {"start": v(-7.07, 8.13) * mm, "end": v(-7.16, 8.25) * mm});
            skLineSegment(sketch, "E419", {"start": v(-7.16, 8.25) * mm, "end": v(-7.25, 8.37) * mm});
            skLineSegment(sketch, "E420", {"start": v(-7.25, 8.37) * mm, "end": v(-7.34, 8.49) * mm});
            skLineSegment(sketch, "E421", {"start": v(-7.34, 8.49) * mm, "end": v(-7.44, 8.6) * mm});
            skLineSegment(sketch, "E422", {"start": v(-7.44, 8.6) * mm, "end": v(-7.54, 8.73) * mm});
            skLineSegment(sketch, "E423", {"start": v(-7.54, 8.73) * mm, "end": v(-7.65, 8.83) * mm});
            skLineSegment(sketch, "E424", {"start": v(-7.65, 8.83) * mm, "end": v(-7.78, 8.9) * mm});
            skLineSegment(sketch, "E425", {"start": v(-7.78, 8.9) * mm, "end": v(-7.93, 8.93) * mm});
            skLineSegment(sketch, "E426", {"start": v(-7.93, 8.93) * mm, "end": v(-8.01, 8.94) * mm});
            skLineSegment(sketch, "E427", {"start": v(-8.01, 8.94) * mm, "end": v(-8.16, 8.92) * mm});
            skLineSegment(sketch, "E428", {"start": v(-8.16, 8.92) * mm, "end": v(-8.3, 8.86) * mm});
            skLineSegment(sketch, "E429", {"start": v(-8.3, 8.86) * mm, "end": v(-8.4, 8.79) * mm});
            skLineSegment(sketch, "E430", {"start": v(-8.4, 8.79) * mm, "end": v(-8.5, 8.67) * mm});
            skLineSegment(sketch, "E431", {"start": v(-8.5, 8.67) * mm, "end": v(-8.58, 8.54) * mm});
            skLineSegment(sketch, "E432", {"start": v(-8.58, 8.54) * mm, "end": v(-8.62, 8.4) * mm});
            skLineSegment(sketch, "E433", {"start": v(-8.62, 8.4) * mm, "end": v(-8.62, 8.25) * mm});
            skLineSegment(sketch, "E434", {"start": v(-8.62, 8.25) * mm, "end": v(-8.59, 8.1) * mm});
            skLineSegment(sketch, "E435", {"start": v(-8.59, 8.1) * mm, "end": v(-8.52, 7.97) * mm});
            skLineSegment(sketch, "E436", {"start": v(-8.52, 7.97) * mm, "end": v(-8.46, 7.9) * mm});
            skLineSegment(sketch, "E437", {"start": v(-8.46, 7.9) * mm, "end": v(-8.36, 7.78) * mm});
            skLineSegment(sketch, "E438", {"start": v(-8.36, 7.78) * mm, "end": v(-8.25, 7.68) * mm});
            skLineSegment(sketch, "E439", {"start": v(-8.25, 7.68) * mm, "end": v(-8.15, 7.57) * mm});
            skLineSegment(sketch, "E440", {"start": v(-8.15, 7.57) * mm, "end": v(-8.05, 7.46) * mm});
            skLineSegment(sketch, "E441", {"start": v(-8.05, 7.46) * mm, "end": v(-7.94, 7.36) * mm});
            skLineSegment(sketch, "E442", {"start": v(-7.94, 7.36) * mm, "end": v(-7.84, 7.25) * mm});
            skLineSegment(sketch, "E443", {"start": v(-7.84, 7.25) * mm, "end": v(-7.73, 7.14) * mm});
            skLineSegment(sketch, "E444", {"start": v(-7.73, 7.14) * mm, "end": v(-7.63, 7.04) * mm});
            skLineSegment(sketch, "E445", {"start": v(-7.63, 7.04) * mm, "end": v(-7.52, 6.93) * mm});
            skLineSegment(sketch, "E446", {"start": v(-7.52, 6.93) * mm, "end": v(-7.42, 6.82) * mm});
            skLineSegment(sketch, "E447", {"start": v(-7.42, 6.82) * mm, "end": v(-7.32, 6.72) * mm});
            skLineSegment(sketch, "E448", {"start": v(-7.32, 6.72) * mm, "end": v(-7.21, 6.6) * mm});
            skLineSegment(sketch, "E449", {"start": v(-7.21, 6.6) * mm, "end": v(-7.12, 6.52) * mm});
            skLineSegment(sketch, "E450", {"start": v(-7.12, 6.52) * mm, "end": v(-7.22, 6.4) * mm});
            skLineSegment(sketch, "E451", {"start": v(-7.22, 6.4) * mm, "end": v(-7.32, 6.3) * mm});
            skLineSegment(sketch, "E452", {"start": v(-7.32, 6.3) * mm, "end": v(-7.41, 6.18) * mm});
            skLineSegment(sketch, "E453", {"start": v(-7.41, 6.18) * mm, "end": v(-7.51, 6.07) * mm});
            skLineSegment(sketch, "E454", {"start": v(-7.51, 6.07) * mm, "end": v(-7.6, 5.96) * mm});
            skLineSegment(sketch, "E455", {"start": v(-7.6, 5.96) * mm, "end": v(-7.7, 5.84) * mm});
            skLineSegment(sketch, "E456", {"start": v(-7.7, 5.84) * mm, "end": v(-7.8, 5.73) * mm});
            skLineSegment(sketch, "E457", {"start": v(-7.8, 5.73) * mm, "end": v(-7.9, 5.62) * mm});
            skLineSegment(sketch, "E458", {"start": v(-7.9, 5.62) * mm, "end": v(-8, 5.5) * mm});
            skLineSegment(sketch, "E459", {"start": v(-8, 5.5) * mm, "end": v(-8.1, 5.4) * mm});
            skLineSegment(sketch, "E460", {"start": v(-8.1, 5.4) * mm, "end": v(-8.15, 5.34) * mm});
            skLineSegment(sketch, "E461", {"start": v(-8.15, 5.34) * mm, "end": v(-8.26, 5.42) * mm});
            skLineSegment(sketch, "E462", {"start": v(-8.26, 5.42) * mm, "end": v(-8.38, 5.51) * mm});
            skLineSegment(sketch, "E463", {"start": v(-8.38, 5.51) * mm, "end": v(-8.5, 5.6) * mm});
            skLineSegment(sketch, "E464", {"start": v(-8.5, 5.6) * mm, "end": v(-8.63, 5.69) * mm});
            skLineSegment(sketch, "E465", {"start": v(-8.63, 5.69) * mm, "end": v(-8.75, 5.77) * mm});
            skLineSegment(sketch, "E466", {"start": v(-8.75, 5.77) * mm, "end": v(-8.87, 5.86) * mm});
            skLineSegment(sketch, "E467", {"start": v(-8.87, 5.86) * mm, "end": v(-8.99, 5.95) * mm});
            skLineSegment(sketch, "E468", {"start": v(-8.99, 5.95) * mm, "end": v(-9.1, 6.04) * mm});
            skLineSegment(sketch, "E469", {"start": v(-9.1, 6.04) * mm, "end": v(-9.23, 6.13) * mm});
            skLineSegment(sketch, "E470", {"start": v(-9.23, 6.13) * mm, "end": v(-9.35, 6.21) * mm});
            skLineSegment(sketch, "E471", {"start": v(-9.35, 6.21) * mm, "end": v(-9.47, 6.3) * mm});
            skLineSegment(sketch, "E472", {"start": v(-9.47, 6.3) * mm, "end": v(-9.6, 6.39) * mm});
            skLineSegment(sketch, "E473", {"start": v(-9.6, 6.39) * mm, "end": v(-9.72, 6.48) * mm});
            skLineSegment(sketch, "E474", {"start": v(-9.72, 6.48) * mm, "end": v(-9.86, 6.54) * mm});
            skLineSegment(sketch, "E475", {"start": v(-9.86, 6.54) * mm, "end": v(-10, 6.57) * mm});
            skLineSegment(sketch, "E476", {"start": v(-10, 6.57) * mm, "end": v(-10.04, 6.57) * mm});
            skLineSegment(sketch, "E477", {"start": v(-10.04, 6.57) * mm, "end": v(-10.19, 6.55) * mm});
            skLineSegment(sketch, "E478", {"start": v(-10.19, 6.55) * mm, "end": v(-10.33, 6.5) * mm});
            skLineSegment(sketch, "E479", {"start": v(-10.33, 6.5) * mm, "end": v(-10.45, 6.42) * mm});
            skLineSegment(sketch, "E480", {"start": v(-10.45, 6.42) * mm, "end": v(-10.56, 6.31) * mm});
            skLineSegment(sketch, "E481", {"start": v(-10.56, 6.31) * mm, "end": v(-10.58, 6.28) * mm});
            skLineSegment(sketch, "E482", {"start": v(-10.58, 6.28) * mm, "end": v(-10.64, 6.15) * mm});
            skLineSegment(sketch, "E483", {"start": v(-10.64, 6.15) * mm, "end": v(-10.67, 6) * mm});
            skLineSegment(sketch, "E484", {"start": v(-10.67, 6) * mm, "end": v(-10.67, 5.86) * mm});
            skLineSegment(sketch, "E485", {"start": v(-10.67, 5.86) * mm, "end": v(-10.63, 5.71) * mm});
            skLineSegment(sketch, "E486", {"start": v(-10.63, 5.71) * mm, "end": v(-10.55, 5.58) * mm});
            skLineSegment(sketch, "E487", {"start": v(-10.55, 5.58) * mm, "end": v(-10.45, 5.47) * mm});
            skLineSegment(sketch, "E488", {"start": v(-10.45, 5.47) * mm, "end": v(-10.37, 5.41) * mm});
            skLineSegment(sketch, "E489", {"start": v(-10.37, 5.41) * mm, "end": v(-10.24, 5.34) * mm});
            skLineSegment(sketch, "E490", {"start": v(-10.24, 5.34) * mm, "end": v(-10.12, 5.27) * mm});
            skLineSegment(sketch, "E491", {"start": v(-10.12, 5.27) * mm, "end": v(-9.98, 5.2) * mm});
            skLineSegment(sketch, "E492", {"start": v(-9.98, 5.2) * mm, "end": v(-9.85, 5.12) * mm});
            skLineSegment(sketch, "E493", {"start": v(-9.85, 5.12) * mm, "end": v(-9.73, 5.05) * mm});
            skLineSegment(sketch, "E494", {"start": v(-9.73, 5.05) * mm, "end": v(-9.6, 4.97) * mm});
            skLineSegment(sketch, "E495", {"start": v(-9.6, 4.97) * mm, "end": v(-9.46, 4.9) * mm});
            skLineSegment(sketch, "E496", {"start": v(-9.46, 4.9) * mm, "end": v(-9.34, 4.83) * mm});
            skLineSegment(sketch, "E497", {"start": v(-9.34, 4.83) * mm, "end": v(-9.2, 4.75) * mm});
            skLineSegment(sketch, "E498", {"start": v(-9.2, 4.75) * mm, "end": v(-9.08, 4.68) * mm});
            skLineSegment(sketch, "E499", {"start": v(-9.08, 4.68) * mm, "end": v(-8.95, 4.6) * mm});
            skLineSegment(sketch, "E500", {"start": v(-8.95, 4.6) * mm, "end": v(-8.81, 4.53) * mm});
            skLineSegment(sketch, "E501", {"start": v(-8.81, 4.53) * mm, "end": v(-8.7, 4.47) * mm});
            skLineSegment(sketch, "E502", {"start": v(-8.7, 4.47) * mm, "end": v(-8.76, 4.33) * mm});
            skLineSegment(sketch, "E503", {"start": v(-8.76, 4.33) * mm, "end": v(-8.83, 4.2) * mm});
            skLineSegment(sketch, "E504", {"start": v(-8.83, 4.2) * mm, "end": v(-8.89, 4.06) * mm});
            skLineSegment(sketch, "E505", {"start": v(-8.89, 4.06) * mm, "end": v(-8.95, 3.93) * mm});
            skLineSegment(sketch, "E506", {"start": v(-8.95, 3.93) * mm, "end": v(-9.01, 3.8) * mm});
            skLineSegment(sketch, "E507", {"start": v(-9.01, 3.8) * mm, "end": v(-9.07, 3.66) * mm});
            skLineSegment(sketch, "E508", {"start": v(-9.07, 3.66) * mm, "end": v(-9.13, 3.53) * mm});
            skLineSegment(sketch, "E509", {"start": v(-9.13, 3.53) * mm, "end": v(-9.2, 3.4) * mm});
            skLineSegment(sketch, "E510", {"start": v(-9.2, 3.4) * mm, "end": v(-9.26, 3.26) * mm});
            skLineSegment(sketch, "E511", {"start": v(-9.26, 3.26) * mm, "end": v(-9.32, 3.12) * mm});
            skLineSegment(sketch, "E512", {"start": v(-9.32, 3.12) * mm, "end": v(-9.35, 3.05) * mm});
            skLineSegment(sketch, "E513", {"start": v(-9.35, 3.05) * mm, "end": v(-9.5, 3.1) * mm});
            skLineSegment(sketch, "E514", {"start": v(-9.5, 3.1) * mm, "end": v(-9.63, 3.15) * mm});
            skLineSegment(sketch, "E515", {"start": v(-9.63, 3.15) * mm, "end": v(-9.77, 3.2) * mm});
            skLineSegment(sketch, "E516", {"start": v(-9.77, 3.2) * mm, "end": v(-9.91, 3.25) * mm});
            skLineSegment(sketch, "E517", {"start": v(-9.91, 3.25) * mm, "end": v(-10.05, 3.3) * mm});
            skLineSegment(sketch, "E518", {"start": v(-10.05, 3.3) * mm, "end": v(-10.2, 3.35) * mm});
            skLineSegment(sketch, "E519", {"start": v(-10.2, 3.35) * mm, "end": v(-10.33, 3.4) * mm});
            skLineSegment(sketch, "E520", {"start": v(-10.33, 3.4) * mm, "end": v(-10.47, 3.45) * mm});
            skLineSegment(sketch, "E521", {"start": v(-10.47, 3.45) * mm, "end": v(-10.62, 3.5) * mm});
            skLineSegment(sketch, "E522", {"start": v(-10.62, 3.5) * mm, "end": v(-10.75, 3.55) * mm});
            skLineSegment(sketch, "E523", {"start": v(-10.75, 3.55) * mm, "end": v(-10.9, 3.6) * mm});
            skLineSegment(sketch, "E524", {"start": v(-10.9, 3.6) * mm, "end": v(-11.04, 3.65) * mm});
            skLineSegment(sketch, "E525", {"start": v(-11.04, 3.65) * mm, "end": v(-11.19, 3.7) * mm});
            skLineSegment(sketch, "E526", {"start": v(-11.19, 3.7) * mm, "end": v(-11.34, 3.72) * mm});
            skLineSegment(sketch, "E527", {"start": v(-11.34, 3.72) * mm, "end": v(-11.35, 3.72) * mm});
            skLineSegment(sketch, "E528", {"start": v(-11.35, 3.72) * mm, "end": v(-11.5, 3.7) * mm});
            skLineSegment(sketch, "E529", {"start": v(-11.5, 3.7) * mm, "end": v(-11.64, 3.65) * mm});
            skLineSegment(sketch, "E530", {"start": v(-11.64, 3.65) * mm, "end": v(-11.76, 3.57) * mm});
            skLineSegment(sketch, "E531", {"start": v(-11.76, 3.57) * mm, "end": v(-11.86, 3.45) * mm});
            skLineSegment(sketch, "E532", {"start": v(-11.86, 3.45) * mm, "end": v(-11.93, 3.32) * mm});
            skLineSegment(sketch, "E533", {"start": v(-11.93, 3.32) * mm, "end": v(-11.95, 3.27) * mm});
            skLineSegment(sketch, "E534", {"start": v(-11.95, 3.27) * mm, "end": v(-11.97, 3.13) * mm});
            skLineSegment(sketch, "E535", {"start": v(-11.97, 3.13) * mm, "end": v(-11.96, 2.98) * mm});
            skLineSegment(sketch, "E536", {"start": v(-11.96, 2.98) * mm, "end": v(-11.92, 2.84) * mm});
            skLineSegment(sketch, "E537", {"start": v(-11.92, 2.84) * mm, "end": v(-11.84, 2.7) * mm});
            skLineSegment(sketch, "E538", {"start": v(-11.84, 2.7) * mm, "end": v(-11.73, 2.6) * mm});
            skLineSegment(sketch, "E539", {"start": v(-11.73, 2.6) * mm, "end": v(-11.6, 2.53) * mm});
            skLineSegment(sketch, "E540", {"start": v(-11.6, 2.53) * mm, "end": v(-11.5, 2.5) * mm});
            skLineSegment(sketch, "E541", {"start": v(-11.5, 2.5) * mm, "end": v(-11.37, 2.46) * mm});
            skLineSegment(sketch, "E542", {"start": v(-11.37, 2.46) * mm, "end": v(-11.22, 2.43) * mm});
            skLineSegment(sketch, "E543", {"start": v(-11.22, 2.43) * mm, "end": v(-11.07, 2.4) * mm});
            skLineSegment(sketch, "E544", {"start": v(-11.07, 2.4) * mm, "end": v(-10.93, 2.36) * mm});
            skLineSegment(sketch, "E545", {"start": v(-10.93, 2.36) * mm, "end": v(-10.79, 2.33) * mm});
            skLineSegment(sketch, "E546", {"start": v(-10.79, 2.33) * mm, "end": v(-10.64, 2.3) * mm});
            skLineSegment(sketch, "E547", {"start": v(-10.64, 2.3) * mm, "end": v(-10.5, 2.26) * mm});
            skLineSegment(sketch, "E548", {"start": v(-10.5, 2.26) * mm, "end": v(-10.35, 2.22) * mm});
            skLineSegment(sketch, "E549", {"start": v(-10.35, 2.22) * mm, "end": v(-10.2, 2.19) * mm});
            skLineSegment(sketch, "E550", {"start": v(-10.2, 2.19) * mm, "end": v(-10.06, 2.16) * mm});
            skLineSegment(sketch, "E551", {"start": v(-10.06, 2.16) * mm, "end": v(-9.91, 2.12) * mm});
            skLineSegment(sketch, "E552", {"start": v(-9.91, 2.12) * mm, "end": v(-9.77, 2.09) * mm});
            skLineSegment(sketch, "E553", {"start": v(-9.77, 2.09) * mm, "end": v(-9.64, 2.06) * mm});
            skLineSegment(sketch, "E554", {"start": v(-9.64, 2.06) * mm, "end": v(-9.66, 1.91) * mm});
            skLineSegment(sketch, "E555", {"start": v(-9.66, 1.91) * mm, "end": v(-9.68, 1.77) * mm});
            skLineSegment(sketch, "E556", {"start": v(-9.68, 1.77) * mm, "end": v(-9.7, 1.62) * mm});
            skLineSegment(sketch, "E557", {"start": v(-9.7, 1.62) * mm, "end": v(-9.73, 1.47) * mm});
            skLineSegment(sketch, "E558", {"start": v(-9.73, 1.47) * mm, "end": v(-9.75, 1.33) * mm});
            skLineSegment(sketch, "E559", {"start": v(-9.75, 1.33) * mm, "end": v(-9.77, 1.18) * mm});
            skLineSegment(sketch, "E560", {"start": v(-9.77, 1.18) * mm, "end": v(-9.79, 1.03) * mm});
            skLineSegment(sketch, "E561", {"start": v(-9.79, 1.03) * mm, "end": v(-9.81, 0.89) * mm});
            skLineSegment(sketch, "E562", {"start": v(-9.81, 0.89) * mm, "end": v(-9.83, 0.74) * mm});
            skLineSegment(sketch, "E563", {"start": v(-9.83, 0.74) * mm, "end": v(-9.85, 0.6) * mm});
            skLineSegment(sketch, "E564", {"start": v(-9.85, 0.6) * mm, "end": v(-9.86, 0.52) * mm});
            skLineSegment(sketch, "E565", {"start": v(-9.86, 0.52) * mm, "end": v(-10.01, 0.52) * mm});
            skLineSegment(sketch, "E566", {"start": v(-10.01, 0.52) * mm, "end": v(-10.16, 0.53) * mm});
            skLineSegment(sketch, "E567", {"start": v(-10.16, 0.53) * mm, "end": v(-10.31, 0.54) * mm});
            skLineSegment(sketch, "E568", {"start": v(-10.31, 0.54) * mm, "end": v(-10.46, 0.55) * mm});
            skLineSegment(sketch, "E569", {"start": v(-10.46, 0.55) * mm, "end": v(-10.6, 0.56) * mm});
            skLineSegment(sketch, "E570", {"start": v(-10.6, 0.56) * mm, "end": v(-10.76, 0.57) * mm});
            skLineSegment(sketch, "E571", {"start": v(-10.76, 0.57) * mm, "end": v(-10.9, 0.58) * mm});
            skLineSegment(sketch, "E572", {"start": v(-10.9, 0.58) * mm, "end": v(-11.05, 0.58) * mm});
            skLineSegment(sketch, "E573", {"start": v(-11.05, 0.58) * mm, "end": v(-11.2, 0.6) * mm});
            skLineSegment(sketch, "E574", {"start": v(-11.2, 0.6) * mm, "end": v(-11.35, 0.6) * mm});
            skLineSegment(sketch, "E575", {"start": v(-11.35, 0.6) * mm, "end": v(-11.5, 0.6) * mm});
            skLineSegment(sketch, "E576", {"start": v(-11.5, 0.6) * mm, "end": v(-11.65, 0.62) * mm});
            skLineSegment(sketch, "E577", {"start": v(-11.65, 0.62) * mm, "end": v(-11.81, 0.62) * mm});
            skLineSegment(sketch, "E578", {"start": v(-11.81, 0.62) * mm, "end": v(-11.96, 0.6) * mm});
            skLineSegment(sketch, "E579", {"start": v(-11.96, 0.6) * mm, "end": v(-12.1, 0.55) * mm});
            skLineSegment(sketch, "E580", {"start": v(-12.1, 0.55) * mm, "end": v(-12.22, 0.46) * mm});
            skLineSegment(sketch, "E581", {"start": v(-12.22, 0.46) * mm, "end": v(-12.32, 0.35) * mm});
            skLineSegment(sketch, "E582", {"start": v(-12.32, 0.35) * mm, "end": v(-12.38, 0.21) * mm});
            skLineSegment(sketch, "E583", {"start": v(-12.38, 0.21) * mm, "end": v(-12.42, 0.07) * mm});
            skLineSegment(sketch, "E584", {"start": v(-12.42, 0.07) * mm, "end": v(-12.41, -0.08) * mm});
            skLineSegment(sketch, "E585", {"start": v(-12.41, -0.08) * mm, "end": v(-12.38, -0.23) * mm});
            skLineSegment(sketch, "E586", {"start": v(-12.38, -0.23) * mm, "end": v(-12.3, -0.36) * mm});
            skLineSegment(sketch, "E587", {"start": v(-12.3, -0.36) * mm, "end": v(-12.2, -0.47) * mm});
            skLineSegment(sketch, "E588", {"start": v(-12.2, -0.47) * mm, "end": v(-12.08, -0.55) * mm});
            skLineSegment(sketch, "E589", {"start": v(-12.08, -0.55) * mm, "end": v(-11.94, -0.6) * mm});
            skLineSegment(sketch, "E590", {"start": v(-11.94, -0.6) * mm, "end": v(-11.8, -0.62) * mm});
            skLineSegment(sketch, "E591", {"start": v(-11.8, -0.62) * mm, "end": v(-11.65, -0.62) * mm});
            skLineSegment(sketch, "E592", {"start": v(-11.65, -0.62) * mm, "end": v(-11.5, -0.6) * mm});
            skLineSegment(sketch, "E593", {"start": v(-11.5, -0.6) * mm, "end": v(-11.36, -0.6) * mm});
            skLineSegment(sketch, "E594", {"start": v(-11.36, -0.6) * mm, "end": v(-11.2, -0.6) * mm});
            skLineSegment(sketch, "E595", {"start": v(-11.2, -0.6) * mm, "end": v(-11.06, -0.58) * mm});
            skLineSegment(sketch, "E596", {"start": v(-11.06, -0.58) * mm, "end": v(-10.9, -0.58) * mm});
            skLineSegment(sketch, "E597", {"start": v(-10.9, -0.58) * mm, "end": v(-10.76, -0.57) * mm});
            skLineSegment(sketch, "E598", {"start": v(-10.76, -0.57) * mm, "end": v(-10.6, -0.56) * mm});
            skLineSegment(sketch, "E599", {"start": v(-10.6, -0.56) * mm, "end": v(-10.46, -0.55) * mm});
            skLineSegment(sketch, "E600", {"start": v(-10.46, -0.55) * mm, "end": v(-10.31, -0.54) * mm});
            skLineSegment(sketch, "E601", {"start": v(-10.31, -0.54) * mm, "end": v(-10.16, -0.53) * mm});
            skLineSegment(sketch, "E602", {"start": v(-10.16, -0.53) * mm, "end": v(-10.02, -0.52) * mm});
            skLineSegment(sketch, "E603", {"start": v(-10.02, -0.52) * mm, "end": v(-9.86, -0.52) * mm});
            skLineSegment(sketch, "E604", {"start": v(-9.86, -0.52) * mm, "end": v(-9.84, -0.66) * mm});
            skLineSegment(sketch, "E605", {"start": v(-9.84, -0.66) * mm, "end": v(-9.82, -0.8) * mm});
            skLineSegment(sketch, "E606", {"start": v(-9.82, -0.8) * mm, "end": v(-9.8, -0.96) * mm});
            skLineSegment(sketch, "E607", {"start": v(-9.8, -0.96) * mm, "end": v(-9.78, -1.1) * mm});
            skLineSegment(sketch, "E608", {"start": v(-9.78, -1.1) * mm, "end": v(-9.76, -1.25) * mm});
            skLineSegment(sketch, "E609", {"start": v(-9.76, -1.25) * mm, "end": v(-9.74, -1.4) * mm});
            skLineSegment(sketch, "E610", {"start": v(-9.74, -1.4) * mm, "end": v(-9.72, -1.54) * mm});
            skLineSegment(sketch, "E611", {"start": v(-9.72, -1.54) * mm, "end": v(-9.7, -1.69) * mm});
            skLineSegment(sketch, "E612", {"start": v(-9.7, -1.69) * mm, "end": v(-9.67, -1.83) * mm});
            skLineSegment(sketch, "E613", {"start": v(-9.67, -1.83) * mm, "end": v(-9.65, -1.98) * mm});
            skLineSegment(sketch, "E614", {"start": v(-9.65, -1.98) * mm, "end": v(-9.64, -2.06) * mm});
            skLineSegment(sketch, "E615", {"start": v(-9.64, -2.06) * mm, "end": v(-9.79, -2.1) * mm});
            skLineSegment(sketch, "E616", {"start": v(-9.79, -2.1) * mm, "end": v(-9.93, -2.13) * mm});
            skLineSegment(sketch, "E617", {"start": v(-9.93, -2.13) * mm, "end": v(-10.08, -2.16) * mm});
            skLineSegment(sketch, "E618", {"start": v(-10.08, -2.16) * mm, "end": v(-10.22, -2.2) * mm});
            skLineSegment(sketch, "E619", {"start": v(-10.22, -2.2) * mm, "end": v(-10.37, -2.23) * mm});
            skLineSegment(sketch, "E620", {"start": v(-10.37, -2.23) * mm, "end": v(-10.51, -2.26) * mm});
            skLineSegment(sketch, "E621", {"start": v(-10.51, -2.26) * mm, "end": v(-10.66, -2.3) * mm});
            skLineSegment(sketch, "E622", {"start": v(-10.66, -2.3) * mm, "end": v(-10.8, -2.33) * mm});
            skLineSegment(sketch, "E623", {"start": v(-10.8, -2.33) * mm, "end": v(-10.95, -2.36) * mm});
            skLineSegment(sketch, "E624", {"start": v(-10.95, -2.36) * mm, "end": v(-11.1, -2.4) * mm});
            skLineSegment(sketch, "E625", {"start": v(-11.1, -2.4) * mm, "end": v(-11.24, -2.43) * mm});
            skLineSegment(sketch, "E626", {"start": v(-11.24, -2.43) * mm, "end": v(-11.38, -2.47) * mm});
            skLineSegment(sketch, "E627", {"start": v(-11.38, -2.47) * mm, "end": v(-11.54, -2.5) * mm});
            skLineSegment(sketch, "E628", {"start": v(-11.54, -2.5) * mm, "end": v(-11.67, -2.57) * mm});
            skLineSegment(sketch, "E629", {"start": v(-11.67, -2.57) * mm, "end": v(-11.8, -2.66) * mm});
            skLineSegment(sketch, "E630", {"start": v(-11.8, -2.66) * mm, "end": v(-11.88, -2.78) * mm});
            skLineSegment(sketch, "E631", {"start": v(-11.88, -2.78) * mm, "end": v(-11.95, -2.91) * mm});
            skLineSegment(sketch, "E632", {"start": v(-11.95, -2.91) * mm, "end": v(-11.97, -3.06) * mm});
            skLineSegment(sketch, "E633", {"start": v(-11.97, -3.06) * mm, "end": v(-11.97, -3.21) * mm});
            skLineSegment(sketch, "E634", {"start": v(-11.97, -3.21) * mm, "end": v(-11.92, -3.35) * mm});
            skLineSegment(sketch, "E635", {"start": v(-11.92, -3.35) * mm, "end": v(-11.84, -3.48) * mm});
            skLineSegment(sketch, "E636", {"start": v(-11.84, -3.48) * mm, "end": v(-11.74, -3.59) * mm});
            skLineSegment(sketch, "E637", {"start": v(-11.74, -3.59) * mm, "end": v(-11.61, -3.67) * mm});
            skLineSegment(sketch, "E638", {"start": v(-11.61, -3.67) * mm, "end": v(-11.47, -3.71) * mm});
            skLineSegment(sketch, "E639", {"start": v(-11.47, -3.71) * mm, "end": v(-11.32, -3.72) * mm});
            skLineSegment(sketch, "E640", {"start": v(-11.32, -3.72) * mm, "end": v(-11.18, -3.7) * mm});
            skLineSegment(sketch, "E641", {"start": v(-11.18, -3.7) * mm, "end": v(-11.04, -3.65) * mm});
            skLineSegment(sketch, "E642", {"start": v(-11.04, -3.65) * mm, "end": v(-10.9, -3.6) * mm});
            skLineSegment(sketch, "E643", {"start": v(-10.9, -3.6) * mm, "end": v(-10.76, -3.55) * mm});
            skLineSegment(sketch, "E644", {"start": v(-10.76, -3.55) * mm, "end": v(-10.62, -3.5) * mm});
            skLineSegment(sketch, "E645", {"start": v(-10.62, -3.5) * mm, "end": v(-10.48, -3.45) * mm});
            skLineSegment(sketch, "E646", {"start": v(-10.48, -3.45) * mm, "end": v(-10.34, -3.4) * mm});
            skLineSegment(sketch, "E647", {"start": v(-10.34, -3.4) * mm, "end": v(-10.2, -3.35) * mm});
            skLineSegment(sketch, "E648", {"start": v(-10.2, -3.35) * mm, "end": v(-10.05, -3.3) * mm});
            skLineSegment(sketch, "E649", {"start": v(-10.05, -3.3) * mm, "end": v(-9.92, -3.25) * mm});
            skLineSegment(sketch, "E650", {"start": v(-9.92, -3.25) * mm, "end": v(-9.77, -3.2) * mm});
            skLineSegment(sketch, "E651", {"start": v(-9.77, -3.2) * mm, "end": v(-9.63, -3.15) * mm});
            skLineSegment(sketch, "E652", {"start": v(-9.63, -3.15) * mm, "end": v(-9.5, -3.1) * mm});
            skLineSegment(sketch, "E653", {"start": v(-9.5, -3.1) * mm, "end": v(-9.35, -3.05) * mm});
            skLineSegment(sketch, "E654", {"start": v(-9.35, -3.05) * mm, "end": v(-9.29, -3.18) * mm});
            skLineSegment(sketch, "E655", {"start": v(-9.29, -3.18) * mm, "end": v(-9.23, -3.32) * mm});
            skLineSegment(sketch, "E656", {"start": v(-9.23, -3.32) * mm, "end": v(-9.17, -3.45) * mm});
            skLineSegment(sketch, "E657", {"start": v(-9.17, -3.45) * mm, "end": v(-9.1, -3.59) * mm});
            skLineSegment(sketch, "E658", {"start": v(-9.1, -3.59) * mm, "end": v(-9.04, -3.72) * mm});
            skLineSegment(sketch, "E659", {"start": v(-9.04, -3.72) * mm, "end": v(-8.98, -3.86) * mm});
            skLineSegment(sketch, "E660", {"start": v(-8.98, -3.86) * mm, "end": v(-8.92, -4) * mm});
            skLineSegment(sketch, "E661", {"start": v(-8.92, -4) * mm, "end": v(-8.86, -4.13) * mm});
            skLineSegment(sketch, "E662", {"start": v(-8.86, -4.13) * mm, "end": v(-8.8, -4.26) * mm});
            skLineSegment(sketch, "E663", {"start": v(-8.8, -4.26) * mm, "end": v(-8.74, -4.4) * mm});
            skLineSegment(sketch, "E664", {"start": v(-8.74, -4.4) * mm, "end": v(-8.7, -4.47) * mm});
            skLineSegment(sketch, "E665", {"start": v(-8.7, -4.47) * mm, "end": v(-8.83, -4.54) * mm});
            skLineSegment(sketch, "E666", {"start": v(-8.83, -4.54) * mm, "end": v(-8.96, -4.61) * mm});
            skLineSegment(sketch, "E667", {"start": v(-8.96, -4.61) * mm, "end": v(-9.1, -4.69) * mm});
            skLineSegment(sketch, "E668", {"start": v(-9.1, -4.69) * mm, "end": v(-9.22, -4.76) * mm});
            skLineSegment(sketch, "E669", {"start": v(-9.22, -4.76) * mm, "end": v(-9.35, -4.83) * mm});
            skLineSegment(sketch, "E670", {"start": v(-9.35, -4.83) * mm, "end": v(-9.48, -4.9) * mm});
            skLineSegment(sketch, "E671", {"start": v(-9.48, -4.9) * mm, "end": v(-9.61, -4.98) * mm});
            skLineSegment(sketch, "E672", {"start": v(-9.61, -4.98) * mm, "end": v(-9.74, -5.05) * mm});
            skLineSegment(sketch, "E673", {"start": v(-9.74, -5.05) * mm, "end": v(-9.87, -5.13) * mm});
            skLineSegment(sketch, "E674", {"start": v(-9.87, -5.13) * mm, "end": v(-10, -5.2) * mm});
            skLineSegment(sketch, "E675", {"start": v(-10, -5.2) * mm, "end": v(-10.13, -5.27) * mm});
            skLineSegment(sketch, "E676", {"start": v(-10.13, -5.27) * mm, "end": v(-10.26, -5.35) * mm});
            skLineSegment(sketch, "E677", {"start": v(-10.26, -5.35) * mm, "end": v(-10.4, -5.43) * mm});
            skLineSegment(sketch, "E678", {"start": v(-10.4, -5.43) * mm, "end": v(-10.51, -5.53) * mm});
            skLineSegment(sketch, "E679", {"start": v(-10.51, -5.53) * mm, "end": v(-10.6, -5.65) * mm});
            skLineSegment(sketch, "E680", {"start": v(-10.6, -5.65) * mm, "end": v(-10.65, -5.79) * mm});
            skLineSegment(sketch, "E681", {"start": v(-10.65, -5.79) * mm, "end": v(-10.67, -5.94) * mm});
            skLineSegment(sketch, "E682", {"start": v(-10.67, -5.94) * mm, "end": v(-10.66, -6.08) * mm});
            skLineSegment(sketch, "E683", {"start": v(-10.66, -6.08) * mm, "end": v(-10.6, -6.23) * mm});
            skLineSegment(sketch, "E684", {"start": v(-10.6, -6.23) * mm, "end": v(-10.58, -6.29) * mm});
            skLineSegment(sketch, "E685", {"start": v(-10.58, -6.29) * mm, "end": v(-10.48, -6.4) * mm});
            skLineSegment(sketch, "E686", {"start": v(-10.48, -6.4) * mm, "end": v(-10.36, -6.49) * mm});
            skLineSegment(sketch, "E687", {"start": v(-10.36, -6.49) * mm, "end": v(-10.22, -6.55) * mm});
            skLineSegment(sketch, "E688", {"start": v(-10.22, -6.55) * mm, "end": v(-10.07, -6.57) * mm});
            skLineSegment(sketch, "E689", {"start": v(-10.07, -6.57) * mm, "end": v(-9.93, -6.56) * mm});
            skLineSegment(sketch, "E690", {"start": v(-9.93, -6.56) * mm, "end": v(-9.78, -6.51) * mm});
            skLineSegment(sketch, "E691", {"start": v(-9.78, -6.51) * mm, "end": v(-9.7, -6.46) * mm});
            skLineSegment(sketch, "E692", {"start": v(-9.7, -6.46) * mm, "end": v(-9.58, -6.38) * mm});
            skLineSegment(sketch, "E693", {"start": v(-9.58, -6.38) * mm, "end": v(-9.46, -6.29) * mm});
            skLineSegment(sketch, "E694", {"start": v(-9.46, -6.29) * mm, "end": v(-9.33, -6.2) * mm});
            skLineSegment(sketch, "E695", {"start": v(-9.33, -6.2) * mm, "end": v(-9.22, -6.11) * mm});
            skLineSegment(sketch, "E696", {"start": v(-9.22, -6.11) * mm, "end": v(-9.1, -6.03) * mm});
            skLineSegment(sketch, "E697", {"start": v(-9.1, -6.03) * mm, "end": v(-8.97, -5.94) * mm});
            skLineSegment(sketch, "E698", {"start": v(-8.97, -5.94) * mm, "end": v(-8.85, -5.85) * mm});
            skLineSegment(sketch, "E699", {"start": v(-8.85, -5.85) * mm, "end": v(-8.73, -5.76) * mm});
            skLineSegment(sketch, "E700", {"start": v(-8.73, -5.76) * mm, "end": v(-8.61, -5.67) * mm});
            skLineSegment(sketch, "E701", {"start": v(-8.61, -5.67) * mm, "end": v(-8.5, -5.59) * mm});
            skLineSegment(sketch, "E702", {"start": v(-8.5, -5.59) * mm, "end": v(-8.37, -5.5) * mm});
            skLineSegment(sketch, "E703", {"start": v(-8.37, -5.5) * mm, "end": v(-8.25, -5.41) * mm});
            skLineSegment(sketch, "E704", {"start": v(-8.25, -5.41) * mm, "end": v(-8.15, -5.34) * mm});
            skLineSegment(sketch, "E705", {"start": v(-8.15, -5.34) * mm, "end": v(-8.05, -5.45) * mm});
            skLineSegment(sketch, "E706", {"start": v(-8.05, -5.45) * mm, "end": v(-7.95, -5.56) * mm});
            skLineSegment(sketch, "E707", {"start": v(-7.95, -5.56) * mm, "end": v(-7.85, -5.67) * mm});
            skLineSegment(sketch, "E708", {"start": v(-7.85, -5.67) * mm, "end": v(-7.76, -5.78) * mm});
            skLineSegment(sketch, "E709", {"start": v(-7.76, -5.78) * mm, "end": v(-7.66, -5.9) * mm});
            skLineSegment(sketch, "E710", {"start": v(-7.66, -5.9) * mm, "end": v(-7.56, -6) * mm});
            skLineSegment(sketch, "E711", {"start": v(-7.56, -6) * mm, "end": v(-7.47, -6.12) * mm});
            skLineSegment(sketch, "E712", {"start": v(-7.47, -6.12) * mm, "end": v(-7.37, -6.23) * mm});
            skLineSegment(sketch, "E713", {"start": v(-7.37, -6.23) * mm, "end": v(-7.27, -6.34) * mm});
            skLineSegment(sketch, "E714", {"start": v(-7.27, -6.34) * mm, "end": v(-7.18, -6.45) * mm});
            skLineSegment(sketch, "E715", {"start": v(-7.18, -6.45) * mm, "end": v(-7.12, -6.52) * mm});
            skLineSegment(sketch, "E716", {"start": v(-7.12, -6.52) * mm, "end": v(-7.23, -6.62) * mm});
            skLineSegment(sketch, "E717", {"start": v(-7.23, -6.62) * mm, "end": v(-7.33, -6.73) * mm});
            skLineSegment(sketch, "E718", {"start": v(-7.33, -6.73) * mm, "end": v(-7.44, -6.84) * mm});
            skLineSegment(sketch, "E719", {"start": v(-7.44, -6.84) * mm, "end": v(-7.54, -6.94) * mm});
            skLineSegment(sketch, "E720", {"start": v(-7.54, -6.94) * mm, "end": v(-7.64, -7.05) * mm});
            skLineSegment(sketch, "E721", {"start": v(-7.64, -7.05) * mm, "end": v(-7.75, -7.16) * mm});
            skLineSegment(sketch, "E722", {"start": v(-7.75, -7.16) * mm, "end": v(-7.85, -7.26) * mm});
            skLineSegment(sketch, "E723", {"start": v(-7.85, -7.26) * mm, "end": v(-7.95, -7.37) * mm});
            skLineSegment(sketch, "E724", {"start": v(-7.95, -7.37) * mm, "end": v(-8.06, -7.48) * mm});
            skLineSegment(sketch, "E725", {"start": v(-8.06, -7.48) * mm, "end": v(-8.16, -7.58) * mm});
            skLineSegment(sketch, "E726", {"start": v(-8.16, -7.58) * mm, "end": v(-8.27, -7.7) * mm});
            skLineSegment(sketch, "E727", {"start": v(-8.27, -7.7) * mm, "end": v(-8.37, -7.8) * mm});
            skLineSegment(sketch, "E728", {"start": v(-8.37, -7.8) * mm, "end": v(-8.48, -7.92) * mm});
            skLineSegment(sketch, "E729", {"start": v(-8.48, -7.92) * mm, "end": v(-8.56, -8.04) * mm});
            skLineSegment(sketch, "E730", {"start": v(-8.56, -8.04) * mm, "end": v(-8.61, -8.18) * mm});
            skLineSegment(sketch, "E731", {"start": v(-8.61, -8.18) * mm, "end": v(-8.62, -8.33) * mm});
            skLineSegment(sketch, "E732", {"start": v(-8.62, -8.33) * mm, "end": v(-8.6, -8.48) * mm});
            skLineSegment(sketch, "E733", {"start": v(-8.6, -8.48) * mm, "end": v(-8.54, -8.62) * mm});
            skLineSegment(sketch, "E734", {"start": v(-8.54, -8.62) * mm, "end": v(-8.46, -8.74) * mm});
            skLineSegment(sketch, "E735", {"start": v(-8.46, -8.74) * mm, "end": v(-8.4, -8.79) * mm});
            skLineSegment(sketch, "E736", {"start": v(-8.4, -8.79) * mm, "end": v(-8.28, -8.87) * mm});
            skLineSegment(sketch, "E737", {"start": v(-8.28, -8.87) * mm, "end": v(-8.14, -8.92) * mm});
            skLineSegment(sketch, "E738", {"start": v(-8.14, -8.92) * mm, "end": v(-8, -8.94) * mm});
            skLineSegment(sketch, "E739", {"start": v(-8, -8.94) * mm, "end": v(-7.85, -8.92) * mm});
            skLineSegment(sketch, "E740", {"start": v(-7.85, -8.92) * mm, "end": v(-7.7, -8.87) * mm});
            skLineSegment(sketch, "E741", {"start": v(-7.7, -8.87) * mm, "end": v(-7.58, -8.78) * mm});
            skLineSegment(sketch, "E742", {"start": v(-7.58, -8.78) * mm, "end": v(-7.52, -8.7) * mm});
            skLineSegment(sketch, "E743", {"start": v(-7.52, -8.7) * mm, "end": v(-7.42, -8.6) * mm});
            skLineSegment(sketch, "E744", {"start": v(-7.42, -8.6) * mm, "end": v(-7.33, -8.48) * mm});
            skLineSegment(sketch, "E745", {"start": v(-7.33, -8.48) * mm, "end": v(-7.24, -8.36) * mm});
            skLineSegment(sketch, "E746", {"start": v(-7.24, -8.36) * mm, "end": v(-7.15, -8.24) * mm});
            skLineSegment(sketch, "E747", {"start": v(-7.15, -8.24) * mm, "end": v(-7.06, -8.12) * mm});
            skLineSegment(sketch, "E748", {"start": v(-7.06, -8.12) * mm, "end": v(-6.97, -8) * mm});
            skLineSegment(sketch, "E749", {"start": v(-6.97, -8) * mm, "end": v(-6.88, -7.88) * mm});
            skLineSegment(sketch, "E750", {"start": v(-6.88, -7.88) * mm, "end": v(-6.79, -7.77) * mm});
            skLineSegment(sketch, "E751", {"start": v(-6.79, -7.77) * mm, "end": v(-6.7, -7.65) * mm});
            skLineSegment(sketch, "E752", {"start": v(-6.7, -7.65) * mm, "end": v(-6.6, -7.53) * mm});
            skLineSegment(sketch, "E753", {"start": v(-6.6, -7.53) * mm, "end": v(-6.51, -7.41) * mm});
            skLineSegment(sketch, "E754", {"start": v(-6.51, -7.41) * mm, "end": v(-6.42, -7.3) * mm});
            skLineSegment(sketch, "E755", {"start": v(-6.42, -7.3) * mm, "end": v(-6.34, -7.2) * mm});
            skLineSegment(sketch, "E756", {"start": v(-6.34, -7.2) * mm, "end": v(-6.22, -7.27) * mm});
            skLineSegment(sketch, "E757", {"start": v(-6.22, -7.27) * mm, "end": v(-6.1, -7.35) * mm});
            skLineSegment(sketch, "E758", {"start": v(-6.1, -7.35) * mm, "end": v(-5.97, -7.43) * mm});
            skLineSegment(sketch, "E759", {"start": v(-5.97, -7.43) * mm, "end": v(-5.85, -7.51) * mm});
            skLineSegment(sketch, "E760", {"start": v(-5.85, -7.51) * mm, "end": v(-5.72, -7.6) * mm});
            skLineSegment(sketch, "E761", {"start": v(-5.72, -7.6) * mm, "end": v(-5.6, -7.67) * mm});
            skLineSegment(sketch, "E762", {"start": v(-5.6, -7.67) * mm, "end": v(-5.47, -7.75) * mm});
            skLineSegment(sketch, "E763", {"start": v(-5.47, -7.75) * mm, "end": v(-5.35, -7.83) * mm});
            skLineSegment(sketch, "E764", {"start": v(-5.35, -7.83) * mm, "end": v(-5.22, -7.91) * mm});
            skLineSegment(sketch, "E765", {"start": v(-5.22, -7.91) * mm, "end": v(-5.1, -8) * mm});
            skLineSegment(sketch, "E766", {"start": v(-5.1, -8) * mm, "end": v(-5.03, -8.03) * mm});
            skLineSegment(sketch, "E767", {"start": v(-5.03, -8.03) * mm, "end": v(-5.1, -8.17) * mm});
            skLineSegment(sketch, "E768", {"start": v(-5.1, -8.17) * mm, "end": v(-5.17, -8.3) * mm});
            skLineSegment(sketch, "E769", {"start": v(-5.17, -8.3) * mm, "end": v(-5.24, -8.43) * mm});
            skLineSegment(sketch, "E770", {"start": v(-5.24, -8.43) * mm, "end": v(-5.3, -8.56) * mm});
            skLineSegment(sketch, "E771", {"start": v(-5.3, -8.56) * mm, "end": v(-5.38, -8.7) * mm});
            skLineSegment(sketch, "E772", {"start": v(-5.38, -8.7) * mm, "end": v(-5.45, -8.83) * mm});
            skLineSegment(sketch, "E773", {"start": v(-5.45, -8.83) * mm, "end": v(-5.52, -8.96) * mm});
            skLineSegment(sketch, "E774", {"start": v(-5.52, -8.96) * mm, "end": v(-5.59, -9.09) * mm});
            skLineSegment(sketch, "E775", {"start": v(-5.59, -9.09) * mm, "end": v(-5.66, -9.22) * mm});
            skLineSegment(sketch, "E776", {"start": v(-5.66, -9.22) * mm, "end": v(-5.73, -9.35) * mm});
            skLineSegment(sketch, "E777", {"start": v(-5.73, -9.35) * mm, "end": v(-5.8, -9.48) * mm});
            skLineSegment(sketch, "E778", {"start": v(-5.8, -9.48) * mm, "end": v(-5.87, -9.62) * mm});
            skLineSegment(sketch, "E779", {"start": v(-5.87, -9.62) * mm, "end": v(-5.94, -9.76) * mm});
            skLineSegment(sketch, "E780", {"start": v(-5.94, -9.76) * mm, "end": v(-5.98, -9.9) * mm});
            skLineSegment(sketch, "E781", {"start": v(-5.98, -9.9) * mm, "end": v(-5.99, -10.05) * mm});
            skLineSegment(sketch, "E782", {"start": v(-5.99, -10.05) * mm, "end": v(-5.96, -10.2) * mm});
            skLineSegment(sketch, "E783", {"start": v(-5.96, -10.2) * mm, "end": v(-5.9, -10.34) * mm});
            skLineSegment(sketch, "E784", {"start": v(-5.9, -10.34) * mm, "end": v(-5.8, -10.45) * mm});
            skLineSegment(sketch, "E785", {"start": v(-5.8, -10.45) * mm, "end": v(-5.68, -10.54) * mm});
            skLineSegment(sketch, "E786", {"start": v(-5.68, -10.54) * mm, "end": v(-5.62, -10.57) * mm});
            skLineSegment(sketch, "E787", {"start": v(-5.62, -10.57) * mm, "end": v(-5.48, -10.62) * mm});
            skLineSegment(sketch, "E788", {"start": v(-5.48, -10.62) * mm, "end": v(-5.33, -10.63) * mm});
            skLineSegment(sketch, "E789", {"start": v(-5.33, -10.63) * mm, "end": v(-5.19, -10.6) * mm});
            skLineSegment(sketch, "E790", {"start": v(-5.19, -10.6) * mm, "end": v(-5.05, -10.55) * mm});
            skLineSegment(sketch, "E791", {"start": v(-5.05, -10.55) * mm, "end": v(-4.93, -10.45) * mm});
            skLineSegment(sketch, "E792", {"start": v(-4.93, -10.45) * mm, "end": v(-4.84, -10.34) * mm});
            skLineSegment(sketch, "E793", {"start": v(-4.84, -10.34) * mm, "end": v(-4.79, -10.25) * mm});
            skLineSegment(sketch, "E794", {"start": v(-4.79, -10.25) * mm, "end": v(-4.74, -10.11) * mm});
            skLineSegment(sketch, "E795", {"start": v(-4.74, -10.11) * mm, "end": v(-4.68, -9.97) * mm});
            skLineSegment(sketch, "E796", {"start": v(-4.68, -9.97) * mm, "end": v(-4.63, -9.83) * mm});
            skLineSegment(sketch, "E797", {"start": v(-4.63, -9.83) * mm, "end": v(-4.57, -9.7) * mm});
            skLineSegment(sketch, "E798", {"start": v(-4.57, -9.7) * mm, "end": v(-4.52, -9.56) * mm});
            skLineSegment(sketch, "E799", {"start": v(-4.52, -9.56) * mm, "end": v(-4.46, -9.42) * mm});
            skLineSegment(sketch, "E800", {"start": v(-4.46, -9.42) * mm, "end": v(-4.41, -9.28) * mm});
            skLineSegment(sketch, "E801", {"start": v(-4.41, -9.28) * mm, "end": v(-4.36, -9.14) * mm});
            skLineSegment(sketch, "E802", {"start": v(-4.36, -9.14) * mm, "end": v(-4.3, -9) * mm});
            skLineSegment(sketch, "E803", {"start": v(-4.3, -9) * mm, "end": v(-4.25, -8.86) * mm});
            skLineSegment(sketch, "E804", {"start": v(-4.25, -8.86) * mm, "end": v(-4.2, -8.72) * mm});
            skLineSegment(sketch, "E805", {"start": v(-4.2, -8.72) * mm, "end": v(-4.14, -8.58) * mm});
            skLineSegment(sketch, "E806", {"start": v(-4.14, -8.58) * mm, "end": v(-4.1, -8.46) * mm});
            skLineSegment(sketch, "E807", {"start": v(-4.1, -8.46) * mm, "end": v(-3.95, -8.5) * mm});
            skLineSegment(sketch, "E808", {"start": v(-3.95, -8.5) * mm, "end": v(-3.8, -8.55) * mm});
            skLineSegment(sketch, "E809", {"start": v(-3.8, -8.55) * mm, "end": v(-3.67, -8.59) * mm});
            skLineSegment(sketch, "E810", {"start": v(-3.67, -8.59) * mm, "end": v(-3.53, -8.63) * mm});
            skLineSegment(sketch, "E811", {"start": v(-3.53, -8.63) * mm, "end": v(-3.38, -8.67) * mm});
            skLineSegment(sketch, "E812", {"start": v(-3.38, -8.67) * mm, "end": v(-3.24, -8.71) * mm});
            skLineSegment(sketch, "E813", {"start": v(-3.24, -8.71) * mm, "end": v(-3.1, -8.75) * mm});
            skLineSegment(sketch, "E814", {"start": v(-3.1, -8.75) * mm, "end": v(-2.96, -8.8) * mm});
            skLineSegment(sketch, "E815", {"start": v(-2.96, -8.8) * mm, "end": v(-2.82, -8.84) * mm});
            skLineSegment(sketch, "E816", {"start": v(-2.82, -8.84) * mm, "end": v(-2.67, -8.88) * mm});
            skLineSegment(sketch, "E817", {"start": v(-2.67, -8.88) * mm, "end": v(-2.6, -8.9) * mm});
            skLineSegment(sketch, "E818", {"start": v(-2.6, -8.9) * mm, "end": v(-2.63, -9.05) * mm});
            skLineSegment(sketch, "E819", {"start": v(-2.63, -9.05) * mm, "end": v(-2.66, -9.2) * mm});
            skLineSegment(sketch, "E820", {"start": v(-2.66, -9.2) * mm, "end": v(-2.69, -9.34) * mm});
            skLineSegment(sketch, "E821", {"start": v(-2.69, -9.34) * mm, "end": v(-2.72, -9.49) * mm});
            skLineSegment(sketch, "E822", {"start": v(-2.72, -9.49) * mm, "end": v(-2.74, -9.63) * mm});
            skLineSegment(sketch, "E823", {"start": v(-2.74, -9.63) * mm, "end": v(-2.77, -9.78) * mm});
            skLineSegment(sketch, "E824", {"start": v(-2.77, -9.78) * mm, "end": v(-2.8, -9.92) * mm});
            skLineSegment(sketch, "E825", {"start": v(-2.8, -9.92) * mm, "end": v(-2.83, -10.07) * mm});
            skLineSegment(sketch, "E826", {"start": v(-2.83, -10.07) * mm, "end": v(-2.86, -10.22) * mm});
            skLineSegment(sketch, "E827", {"start": v(-2.86, -10.22) * mm, "end": v(-2.9, -10.36) * mm});
            skLineSegment(sketch, "E828", {"start": v(-2.9, -10.36) * mm, "end": v(-2.92, -10.5) * mm});
            skLineSegment(sketch, "E829", {"start": v(-2.92, -10.5) * mm, "end": v(-2.95, -10.66) * mm});
            skLineSegment(sketch, "E830", {"start": v(-2.95, -10.66) * mm, "end": v(-2.98, -10.81) * mm});
            skLineSegment(sketch, "E831", {"start": v(-2.98, -10.81) * mm, "end": v(-2.98, -10.96) * mm});
            skLineSegment(sketch, "E832", {"start": v(-2.98, -10.96) * mm, "end": v(-2.95, -11.1) * mm});
            skLineSegment(sketch, "E833", {"start": v(-2.95, -11.1) * mm, "end": v(-2.88, -11.24) * mm});
            skLineSegment(sketch, "E834", {"start": v(-2.88, -11.24) * mm, "end": v(-2.78, -11.35) * mm});
            skLineSegment(sketch, "E835", {"start": v(-2.78, -11.35) * mm, "end": v(-2.66, -11.44) * mm});
            skLineSegment(sketch, "E836", {"start": v(-2.66, -11.44) * mm, "end": v(-2.52, -11.5) * mm});
            skLineSegment(sketch, "E837", {"start": v(-2.52, -11.5) * mm, "end": v(-2.37, -11.51) * mm});
            skLineSegment(sketch, "E838", {"start": v(-2.37, -11.51) * mm, "end": v(-2.22, -11.5) * mm});
            skLineSegment(sketch, "E839", {"start": v(-2.22, -11.5) * mm, "end": v(-2.08, -11.44) * mm});
            skLineSegment(sketch, "E840", {"start": v(-2.08, -11.44) * mm, "end": v(-1.95, -11.36) * mm});
            skLineSegment(sketch, "E841", {"start": v(-1.95, -11.36) * mm, "end": v(-1.86, -11.25) * mm});
            skLineSegment(sketch, "E842", {"start": v(-1.86, -11.25) * mm, "end": v(-1.78, -11.12) * mm});
            skLineSegment(sketch, "E843", {"start": v(-1.78, -11.12) * mm, "end": v(-1.74, -10.98) * mm});
            skLineSegment(sketch, "E844", {"start": v(-1.74, -10.98) * mm, "end": v(-1.74, -10.96) * mm});
            skLineSegment(sketch, "E845", {"start": v(-1.74, -10.96) * mm, "end": v(-1.73, -10.81) * mm});
            skLineSegment(sketch, "E846", {"start": v(-1.73, -10.81) * mm, "end": v(-1.71, -10.66) * mm});
            skLineSegment(sketch, "E847", {"start": v(-1.71, -10.66) * mm, "end": v(-1.7, -10.51) * mm});
            skLineSegment(sketch, "E848", {"start": v(-1.7, -10.51) * mm, "end": v(-1.69, -10.37) * mm});
            skLineSegment(sketch, "E849", {"start": v(-1.69, -10.37) * mm, "end": v(-1.68, -10.22) * mm});
            skLineSegment(sketch, "E850", {"start": v(-1.68, -10.22) * mm, "end": v(-1.66, -10.07) * mm});
            skLineSegment(sketch, "E851", {"start": v(-1.66, -10.07) * mm, "end": v(-1.65, -9.92) * mm});
            skLineSegment(sketch, "E852", {"start": v(-1.65, -9.92) * mm, "end": v(-1.64, -9.77) * mm});
            skLineSegment(sketch, "E853", {"start": v(-1.64, -9.77) * mm, "end": v(-1.62, -9.62) * mm});
            skLineSegment(sketch, "E854", {"start": v(-1.62, -9.62) * mm, "end": v(-1.61, -9.48) * mm});
            skLineSegment(sketch, "E855", {"start": v(-1.61, -9.48) * mm, "end": v(-1.6, -9.33) * mm});
            skLineSegment(sketch, "E856", {"start": v(-1.6, -9.33) * mm, "end": v(-1.59, -9.18) * mm});
            skLineSegment(sketch, "E857", {"start": v(-1.59, -9.18) * mm, "end": v(-1.58, -9.05) * mm});
            skLineSegment(sketch, "E858", {"start": v(-1.58, -9.05) * mm, "end": v(-1.43, -9.05) * mm});
            skLineSegment(sketch, "E859", {"start": v(-1.43, -9.05) * mm, "end": v(-1.28, -9.05) * mm});
            skLineSegment(sketch, "E860", {"start": v(-1.28, -9.05) * mm, "end": v(-1.13, -9.05) * mm});
            skLineSegment(sketch, "E861", {"start": v(-1.13, -9.05) * mm, "end": v(-0.98, -9.05) * mm});
            skLineSegment(sketch, "E862", {"start": v(-0.98, -9.05) * mm, "end": v(-0.84, -9.05) * mm});
            skLineSegment(sketch, "E863", {"start": v(-0.84, -9.05) * mm, "end": v(-0.69, -9.05) * mm});
            skLineSegment(sketch, "E864", {"start": v(-0.69, -9.05) * mm, "end": v(-0.54, -9.05) * mm});
            skLineSegment(sketch, "E865", {"start": v(-0.54, -9.05) * mm, "end": v(-0.4, -9.05) * mm});
            skLineSegment(sketch, "E866", {"start": v(-0.4, -9.05) * mm, "end": v(-0.24, -9.05) * mm});
            skLineSegment(sketch, "E867", {"start": v(-0.24, -9.05) * mm, "end": v(-0.1, -9.05) * mm});
            skLineSegment(sketch, "E868", {"start": v(-0.1, -9.05) * mm, "end": v(-0.02, -9.05) * mm});
            skLineSegment(sketch, "E869", {"start": v(-0.02, -9.05) * mm, "end": v(0, -9.2) * mm});
            skLineSegment(sketch, "E870", {"start": v(0, -9.2) * mm, "end": v(0, -9.34) * mm});
            skLineSegment(sketch, "E871", {"start": v(0, -9.34) * mm, "end": v(0.02, -9.5) * mm});
            skLineSegment(sketch, "E872", {"start": v(0.02, -9.5) * mm, "end": v(0.04, -9.64) * mm});
            skLineSegment(sketch, "E873", {"start": v(0.04, -9.64) * mm, "end": v(0.05, -9.79) * mm});
            skLineSegment(sketch, "E874", {"start": v(0.05, -9.79) * mm, "end": v(0.06, -9.94) * mm});
            skLineSegment(sketch, "E875", {"start": v(0.06, -9.94) * mm, "end": v(0.07, -10.09) * mm});
            skLineSegment(sketch, "E876", {"start": v(0.07, -10.09) * mm, "end": v(0.09, -10.24) * mm});
            skLineSegment(sketch, "E877", {"start": v(0.09, -10.24) * mm, "end": v(0.1, -10.39) * mm});
            skLineSegment(sketch, "E878", {"start": v(0.1, -10.39) * mm, "end": v(0.11, -10.53) * mm});
            skLineSegment(sketch, "E879", {"start": v(0.11, -10.53) * mm, "end": v(0.12, -10.68) * mm});
            skLineSegment(sketch, "E880", {"start": v(0.12, -10.68) * mm, "end": v(0.14, -10.83) * mm});
            skLineSegment(sketch, "E881", {"start": v(0.14, -10.83) * mm, "end": v(0.15, -11) * mm});
            skLineSegment(sketch, "E882", {"start": v(0.15, -11) * mm, "end": v(0.2, -11.13) * mm});
            skLineSegment(sketch, "E883", {"start": v(0.2, -11.13) * mm, "end": v(0.27, -11.27) * mm});
            skLineSegment(sketch, "E884", {"start": v(0.27, -11.27) * mm, "end": v(0.38, -11.37) * mm});
            skLineSegment(sketch, "E885", {"start": v(0.38, -11.37) * mm, "end": v(0.5, -11.45) * mm});
            skLineSegment(sketch, "E886", {"start": v(0.5, -11.45) * mm, "end": v(0.64, -11.5) * mm});
            skLineSegment(sketch, "E887", {"start": v(0.64, -11.5) * mm, "end": v(0.8, -11.51) * mm});
            skLineSegment(sketch, "E888", {"start": v(0.8, -11.51) * mm, "end": v(0.94, -11.49) * mm});
            skLineSegment(sketch, "E889", {"start": v(0.94, -11.49) * mm, "end": v(1.08, -11.43) * mm});
            skLineSegment(sketch, "E890", {"start": v(1.08, -11.43) * mm, "end": v(1.2, -11.34) * mm});
            skLineSegment(sketch, "E891", {"start": v(1.2, -11.34) * mm, "end": v(1.3, -11.23) * mm});
            skLineSegment(sketch, "E892", {"start": v(1.3, -11.23) * mm, "end": v(1.36, -11.1) * mm});
            skLineSegment(sketch, "E893", {"start": v(1.36, -11.1) * mm, "end": v(1.4, -10.95) * mm});
            skLineSegment(sketch, "E894", {"start": v(1.4, -10.95) * mm, "end": v(1.39, -10.8) * mm});
            skLineSegment(sketch, "E895", {"start": v(1.39, -10.8) * mm, "end": v(1.39, -10.78) * mm});
            skLineSegment(sketch, "E896", {"start": v(1.39, -10.78) * mm, "end": v(1.36, -10.64) * mm});
            skLineSegment(sketch, "E897", {"start": v(1.36, -10.64) * mm, "end": v(1.33, -10.5) * mm});
            skLineSegment(sketch, "E898", {"start": v(1.33, -10.5) * mm, "end": v(1.3, -10.34) * mm});
            skLineSegment(sketch, "E899", {"start": v(1.3, -10.34) * mm, "end": v(1.27, -10.2) * mm});
            skLineSegment(sketch, "E900", {"start": v(1.27, -10.2) * mm, "end": v(1.24, -10.05) * mm});
            skLineSegment(sketch, "E901", {"start": v(1.24, -10.05) * mm, "end": v(1.2, -9.9) * mm});
            skLineSegment(sketch, "E902", {"start": v(1.2, -9.9) * mm, "end": v(1.18, -9.76) * mm});
            skLineSegment(sketch, "E903", {"start": v(1.18, -9.76) * mm, "end": v(1.15, -9.61) * mm});
            skLineSegment(sketch, "E904", {"start": v(1.15, -9.61) * mm, "end": v(1.12, -9.47) * mm});
            skLineSegment(sketch, "E905", {"start": v(1.12, -9.47) * mm, "end": v(1.1, -9.32) * mm});
            skLineSegment(sketch, "E906", {"start": v(1.1, -9.32) * mm, "end": v(1.06, -9.18) * mm});
            skLineSegment(sketch, "E907", {"start": v(1.06, -9.18) * mm, "end": v(1.03, -9.03) * mm});
            skLineSegment(sketch, "E908", {"start": v(1.03, -9.03) * mm, "end": v(1, -8.9) * mm});
            skLineSegment(sketch, "E909", {"start": v(1, -8.9) * mm, "end": v(1.15, -8.86) * mm});
            skLineSegment(sketch, "E910", {"start": v(1.15, -8.86) * mm, "end": v(1.29, -8.82) * mm});
            skLineSegment(sketch, "E911", {"start": v(1.29, -8.82) * mm, "end": v(1.43, -8.78) * mm});
            skLineSegment(sketch, "E912", {"start": v(1.43, -8.78) * mm, "end": v(1.57, -8.74) * mm});
            skLineSegment(sketch, "E913", {"start": v(1.57, -8.74) * mm, "end": v(1.71, -8.7) * mm});
            skLineSegment(sketch, "E914", {"start": v(1.71, -8.7) * mm, "end": v(1.86, -8.65) * mm});
            skLineSegment(sketch, "E915", {"start": v(1.86, -8.65) * mm, "end": v(2, -8.61) * mm});
            skLineSegment(sketch, "E916", {"start": v(2, -8.61) * mm, "end": v(2.14, -8.57) * mm});
            skLineSegment(sketch, "E917", {"start": v(2.14, -8.57) * mm, "end": v(2.28, -8.53) * mm});
            skLineSegment(sketch, "E918", {"start": v(2.28, -8.53) * mm, "end": v(2.42, -8.49) * mm});
            skLineSegment(sketch, "E919", {"start": v(2.42, -8.49) * mm, "end": v(2.5, -8.46) * mm});
            skLineSegment(sketch, "E920", {"start": v(2.5, -8.46) * mm, "end": v(2.56, -8.6) * mm});
            skLineSegment(sketch, "E921", {"start": v(2.56, -8.6) * mm, "end": v(2.6, -8.74) * mm});
            skLineSegment(sketch, "E922", {"start": v(2.6, -8.74) * mm, "end": v(2.66, -8.88) * mm});
            skLineSegment(sketch, "E923", {"start": v(2.66, -8.88) * mm, "end": v(2.72, -9.02) * mm});
            skLineSegment(sketch, "E924", {"start": v(2.72, -9.02) * mm, "end": v(2.77, -9.16) * mm});
            skLineSegment(sketch, "E925", {"start": v(2.77, -9.16) * mm, "end": v(2.83, -9.3) * mm});
            skLineSegment(sketch, "E926", {"start": v(2.83, -9.3) * mm, "end": v(2.88, -9.43) * mm});
            skLineSegment(sketch, "E927", {"start": v(2.88, -9.43) * mm, "end": v(2.93, -9.57) * mm});
            skLineSegment(sketch, "E928", {"start": v(2.93, -9.57) * mm, "end": v(2.99, -9.71) * mm});
            skLineSegment(sketch, "E929", {"start": v(2.99, -9.71) * mm, "end": v(3.04, -9.85) * mm});
            skLineSegment(sketch, "E930", {"start": v(3.04, -9.85) * mm, "end": v(3.1, -9.99) * mm});
            skLineSegment(sketch, "E931", {"start": v(3.1, -9.99) * mm, "end": v(3.15, -10.13) * mm});
            skLineSegment(sketch, "E932", {"start": v(3.15, -10.13) * mm, "end": v(3.21, -10.28) * mm});
            skLineSegment(sketch, "E933", {"start": v(3.21, -10.28) * mm, "end": v(3.3, -10.4) * mm});
            skLineSegment(sketch, "E934", {"start": v(3.3, -10.4) * mm, "end": v(3.4, -10.5) * mm});
            skLineSegment(sketch, "E935", {"start": v(3.4, -10.5) * mm, "end": v(3.53, -10.58) * mm});
            skLineSegment(sketch, "E936", {"start": v(3.53, -10.58) * mm, "end": v(3.68, -10.62) * mm});
            skLineSegment(sketch, "E937", {"start": v(3.68, -10.62) * mm, "end": v(3.82, -10.63) * mm});
            skLineSegment(sketch, "E938", {"start": v(3.82, -10.63) * mm, "end": v(3.97, -10.6) * mm});
            skLineSegment(sketch, "E939", {"start": v(3.97, -10.6) * mm, "end": v(4.03, -10.57) * mm});
            skLineSegment(sketch, "E940", {"start": v(4.03, -10.57) * mm, "end": v(4.16, -10.5) * mm});
            skLineSegment(sketch, "E941", {"start": v(4.16, -10.5) * mm, "end": v(4.27, -10.4) * mm});
            skLineSegment(sketch, "E942", {"start": v(4.27, -10.4) * mm, "end": v(4.34, -10.26) * mm});
            skLineSegment(sketch, "E943", {"start": v(4.34, -10.26) * mm, "end": v(4.39, -10.12) * mm});
            skLineSegment(sketch, "E944", {"start": v(4.39, -10.12) * mm, "end": v(4.4, -9.97) * mm});
            skLineSegment(sketch, "E945", {"start": v(4.4, -9.97) * mm, "end": v(4.37, -9.82) * mm});
            skLineSegment(sketch, "E946", {"start": v(4.37, -9.82) * mm, "end": v(4.33, -9.73) * mm});
            skLineSegment(sketch, "E947", {"start": v(4.33, -9.73) * mm, "end": v(4.27, -9.6) * mm});
            skLineSegment(sketch, "E948", {"start": v(4.27, -9.6) * mm, "end": v(4.2, -9.47) * mm});
            skLineSegment(sketch, "E949", {"start": v(4.2, -9.47) * mm, "end": v(4.13, -9.33) * mm});
            skLineSegment(sketch, "E950", {"start": v(4.13, -9.33) * mm, "end": v(4.06, -9.2) * mm});
            skLineSegment(sketch, "E951", {"start": v(4.06, -9.2) * mm, "end": v(3.99, -9.07) * mm});
            skLineSegment(sketch, "E952", {"start": v(3.99, -9.07) * mm, "end": v(3.92, -8.94) * mm});
            skLineSegment(sketch, "E953", {"start": v(3.92, -8.94) * mm, "end": v(3.85, -8.8) * mm});
            skLineSegment(sketch, "E954", {"start": v(3.85, -8.8) * mm, "end": v(3.78, -8.68) * mm});
            skLineSegment(sketch, "E955", {"start": v(3.78, -8.68) * mm, "end": v(3.7, -8.54) * mm});
            skLineSegment(sketch, "E956", {"start": v(3.7, -8.54) * mm, "end": v(3.64, -8.41) * mm});
            skLineSegment(sketch, "E957", {"start": v(3.64, -8.41) * mm, "end": v(3.57, -8.28) * mm});
            skLineSegment(sketch, "E958", {"start": v(3.57, -8.28) * mm, "end": v(3.5, -8.15) * mm});
            skLineSegment(sketch, "E959", {"start": v(3.5, -8.15) * mm, "end": v(3.44, -8.03) * mm});
            skLineSegment(sketch, "E960", {"start": v(3.44, -8.03) * mm, "end": v(3.56, -7.95) * mm});
            skLineSegment(sketch, "E961", {"start": v(3.56, -7.95) * mm, "end": v(3.69, -7.87) * mm});
            skLineSegment(sketch, "E962", {"start": v(3.69, -7.87) * mm, "end": v(3.81, -7.8) * mm});
            skLineSegment(sketch, "E963", {"start": v(3.81, -7.8) * mm, "end": v(3.94, -7.71) * mm});
            skLineSegment(sketch, "E964", {"start": v(3.94, -7.71) * mm, "end": v(4.06, -7.63) * mm});
            skLineSegment(sketch, "E965", {"start": v(4.06, -7.63) * mm, "end": v(4.19, -7.55) * mm});
            skLineSegment(sketch, "E966", {"start": v(4.19, -7.55) * mm, "end": v(4.31, -7.47) * mm});
            skLineSegment(sketch, "E967", {"start": v(4.31, -7.47) * mm, "end": v(4.44, -7.4) * mm});
            skLineSegment(sketch, "E968", {"start": v(4.44, -7.4) * mm, "end": v(4.56, -7.31) * mm});
            skLineSegment(sketch, "E969", {"start": v(4.56, -7.31) * mm, "end": v(4.68, -7.23) * mm});
            skLineSegment(sketch, "E970", {"start": v(4.68, -7.23) * mm, "end": v(4.75, -7.2) * mm});
            skLineSegment(sketch, "E971", {"start": v(4.75, -7.2) * mm, "end": v(4.84, -7.3) * mm});
            skLineSegment(sketch, "E972", {"start": v(4.84, -7.3) * mm, "end": v(4.93, -7.43) * mm});
            skLineSegment(sketch, "E973", {"start": v(4.93, -7.43) * mm, "end": v(5.03, -7.55) * mm});
            skLineSegment(sketch, "E974", {"start": v(5.03, -7.55) * mm, "end": v(5.12, -7.66) * mm});
            skLineSegment(sketch, "E975", {"start": v(5.12, -7.66) * mm, "end": v(5.2, -7.78) * mm});
            skLineSegment(sketch, "E976", {"start": v(5.2, -7.78) * mm, "end": v(5.3, -7.9) * mm});
            skLineSegment(sketch, "E977", {"start": v(5.3, -7.9) * mm, "end": v(5.39, -8.02) * mm});
            skLineSegment(sketch, "E978", {"start": v(5.39, -8.02) * mm, "end": v(5.48, -8.13) * mm});
            skLineSegment(sketch, "E979", {"start": v(5.48, -8.13) * mm, "end": v(5.57, -8.25) * mm});
            skLineSegment(sketch, "E980", {"start": v(5.57, -8.25) * mm, "end": v(5.66, -8.37) * mm});
            skLineSegment(sketch, "E981", {"start": v(5.66, -8.37) * mm, "end": v(5.75, -8.49) * mm});
            skLineSegment(sketch, "E982", {"start": v(5.75, -8.49) * mm, "end": v(5.85, -8.6) * mm});
            skLineSegment(sketch, "E983", {"start": v(5.85, -8.6) * mm, "end": v(5.95, -8.73) * mm});
            skLineSegment(sketch, "E984", {"start": v(5.95, -8.73) * mm, "end": v(6.06, -8.83) * mm});
            skLineSegment(sketch, "E985", {"start": v(6.06, -8.83) * mm, "end": v(6.2, -8.9) * mm});
            skLineSegment(sketch, "E986", {"start": v(6.2, -8.9) * mm, "end": v(6.34, -8.93) * mm});
            skLineSegment(sketch, "E987", {"start": v(6.34, -8.93) * mm, "end": v(6.49, -8.93) * mm});
            skLineSegment(sketch, "E988", {"start": v(6.49, -8.93) * mm, "end": v(6.63, -8.9) * mm});
            skLineSegment(sketch, "E989", {"start": v(6.63, -8.9) * mm, "end": v(6.76, -8.83) * mm});
            skLineSegment(sketch, "E990", {"start": v(6.76, -8.83) * mm, "end": v(6.82, -8.79) * mm});
            skLineSegment(sketch, "E991", {"start": v(6.82, -8.79) * mm, "end": v(6.91, -8.67) * mm});
            skLineSegment(sketch, "E992", {"start": v(6.91, -8.67) * mm, "end": v(6.99, -8.54) * mm});
            skLineSegment(sketch, "E993", {"start": v(6.99, -8.54) * mm, "end": v(7.02, -8.4) * mm});
            skLineSegment(sketch, "E994", {"start": v(7.02, -8.4) * mm, "end": v(7.03, -8.25) * mm});
            skLineSegment(sketch, "E995", {"start": v(7.03, -8.25) * mm, "end": v(7, -8.1) * mm});
            skLineSegment(sketch, "E996", {"start": v(7, -8.1) * mm, "end": v(6.93, -7.97) * mm});
            skLineSegment(sketch, "E997", {"start": v(6.93, -7.97) * mm, "end": v(6.87, -7.9) * mm});
            skLineSegment(sketch, "E998", {"start": v(6.87, -7.9) * mm, "end": v(6.77, -7.78) * mm});
            skLineSegment(sketch, "E999", {"start": v(6.77, -7.78) * mm, "end": v(6.66, -7.68) * mm});
            skLineSegment(sketch, "E1000", {"start": v(6.66, -7.68) * mm, "end": v(6.56, -7.57) * mm});
            skLineSegment(sketch, "E1001", {"start": v(6.56, -7.57) * mm, "end": v(6.45, -7.46) * mm});
            skLineSegment(sketch, "E1002", {"start": v(6.45, -7.46) * mm, "end": v(6.35, -7.36) * mm});
            skLineSegment(sketch, "E1003", {"start": v(6.35, -7.36) * mm, "end": v(6.24, -7.25) * mm});
            skLineSegment(sketch, "E1004", {"start": v(6.24, -7.25) * mm, "end": v(6.14, -7.14) * mm});
            skLineSegment(sketch, "E1005", {"start": v(6.14, -7.14) * mm, "end": v(6.04, -7.04) * mm});
            skLineSegment(sketch, "E1006", {"start": v(6.04, -7.04) * mm, "end": v(5.93, -6.93) * mm});
            skLineSegment(sketch, "E1007", {"start": v(5.93, -6.93) * mm, "end": v(5.83, -6.82) * mm});
            skLineSegment(sketch, "E1008", {"start": v(5.83, -6.82) * mm, "end": v(5.73, -6.72) * mm});
            skLineSegment(sketch, "E1009", {"start": v(5.73, -6.72) * mm, "end": v(5.62, -6.6) * mm});
            skLineSegment(sketch, "E1010", {"start": v(5.62, -6.6) * mm, "end": v(5.53, -6.52) * mm});
            skLineSegment(sketch, "E1011", {"start": v(5.53, -6.52) * mm, "end": v(5.63, -6.4) * mm});
            skLineSegment(sketch, "E1012", {"start": v(5.63, -6.4) * mm, "end": v(5.73, -6.3) * mm});
            skLineSegment(sketch, "E1013", {"start": v(5.73, -6.3) * mm, "end": v(5.82, -6.18) * mm});
            skLineSegment(sketch, "E1014", {"start": v(5.82, -6.18) * mm, "end": v(5.92, -6.07) * mm});
            skLineSegment(sketch, "E1015", {"start": v(5.92, -6.07) * mm, "end": v(6.02, -5.96) * mm});
            skLineSegment(sketch, "E1016", {"start": v(6.02, -5.96) * mm, "end": v(6.11, -5.84) * mm});
            skLineSegment(sketch, "E1017", {"start": v(6.11, -5.84) * mm, "end": v(6.21, -5.73) * mm});
            skLineSegment(sketch, "E1018", {"start": v(6.21, -5.73) * mm, "end": v(6.3, -5.62) * mm});
            skLineSegment(sketch, "E1019", {"start": v(6.3, -5.62) * mm, "end": v(6.4, -5.5) * mm});
            skLineSegment(sketch, "E1020", {"start": v(6.4, -5.5) * mm, "end": v(6.5, -5.4) * mm});
            skLineSegment(sketch, "E1021", {"start": v(6.5, -5.4) * mm, "end": v(6.55, -5.34) * mm});
            skLineSegment(sketch, "E1022", {"start": v(6.55, -5.34) * mm, "end": v(6.67, -5.42) * mm});
            skLineSegment(sketch, "E1023", {"start": v(6.67, -5.42) * mm, "end": v(6.8, -5.51) * mm});
            skLineSegment(sketch, "E1024", {"start": v(6.8, -5.51) * mm, "end": v(6.92, -5.6) * mm});
            skLineSegment(sketch, "E1025", {"start": v(6.92, -5.6) * mm, "end": v(7.04, -5.69) * mm});
            skLineSegment(sketch, "E1026", {"start": v(7.04, -5.69) * mm, "end": v(7.15, -5.77) * mm});
            skLineSegment(sketch, "E1027", {"start": v(7.15, -5.77) * mm, "end": v(7.28, -5.86) * mm});
            skLineSegment(sketch, "E1028", {"start": v(7.28, -5.86) * mm, "end": v(7.4, -5.95) * mm});
            skLineSegment(sketch, "E1029", {"start": v(7.4, -5.95) * mm, "end": v(7.52, -6.04) * mm});
            skLineSegment(sketch, "E1030", {"start": v(7.52, -6.04) * mm, "end": v(7.64, -6.13) * mm});
            skLineSegment(sketch, "E1031", {"start": v(7.64, -6.13) * mm, "end": v(7.76, -6.21) * mm});
            skLineSegment(sketch, "E1032", {"start": v(7.76, -6.21) * mm, "end": v(7.88, -6.3) * mm});
            skLineSegment(sketch, "E1033", {"start": v(7.88, -6.3) * mm, "end": v(8, -6.39) * mm});
            skLineSegment(sketch, "E1034", {"start": v(8, -6.39) * mm, "end": v(8.13, -6.48) * mm});
            skLineSegment(sketch, "E1035", {"start": v(8.13, -6.48) * mm, "end": v(8.27, -6.54) * mm});
            skLineSegment(sketch, "E1036", {"start": v(8.27, -6.54) * mm, "end": v(8.42, -6.57) * mm});
            skLineSegment(sketch, "E1037", {"start": v(8.42, -6.57) * mm, "end": v(8.56, -6.56) * mm});
            skLineSegment(sketch, "E1038", {"start": v(8.56, -6.56) * mm, "end": v(8.7, -6.52) * mm});
            skLineSegment(sketch, "E1039", {"start": v(8.7, -6.52) * mm, "end": v(8.84, -6.44) * mm});
            skLineSegment(sketch, "E1040", {"start": v(8.84, -6.44) * mm, "end": v(8.94, -6.34) * mm});
            skLineSegment(sketch, "E1041", {"start": v(8.94, -6.34) * mm, "end": v(8.98, -6.29) * mm});
            skLineSegment(sketch, "E1042", {"start": v(8.98, -6.29) * mm, "end": v(9.05, -6.15) * mm});
            skLineSegment(sketch, "E1043", {"start": v(9.05, -6.15) * mm, "end": v(9.08, -6) * mm});
            skLineSegment(sketch, "E1044", {"start": v(9.08, -6) * mm, "end": v(9.07, -5.86) * mm});
            skLineSegment(sketch, "E1045", {"start": v(9.07, -5.86) * mm, "end": v(9.04, -5.71) * mm});
            skLineSegment(sketch, "E1046", {"start": v(9.04, -5.71) * mm, "end": v(8.96, -5.58) * mm});
            skLineSegment(sketch, "E1047", {"start": v(8.96, -5.58) * mm, "end": v(8.86, -5.47) * mm});
            skLineSegment(sketch, "E1048", {"start": v(8.86, -5.47) * mm, "end": v(8.78, -5.41) * mm});
            skLineSegment(sketch, "E1049", {"start": v(8.78, -5.41) * mm, "end": v(8.65, -5.34) * mm});
            skLineSegment(sketch, "E1050", {"start": v(8.65, -5.34) * mm, "end": v(8.52, -5.27) * mm});
            skLineSegment(sketch, "E1051", {"start": v(8.52, -5.27) * mm, "end": v(8.4, -5.2) * mm});
            skLineSegment(sketch, "E1052", {"start": v(8.4, -5.2) * mm, "end": v(8.26, -5.12) * mm});
            skLineSegment(sketch, "E1053", {"start": v(8.26, -5.12) * mm, "end": v(8.13, -5.05) * mm});
            skLineSegment(sketch, "E1054", {"start": v(8.13, -5.05) * mm, "end": v(8, -4.97) * mm});
            skLineSegment(sketch, "E1055", {"start": v(8, -4.97) * mm, "end": v(7.87, -4.9) * mm});
            skLineSegment(sketch, "E1056", {"start": v(7.87, -4.9) * mm, "end": v(7.74, -4.83) * mm});
            skLineSegment(sketch, "E1057", {"start": v(7.74, -4.83) * mm, "end": v(7.61, -4.75) * mm});
            skLineSegment(sketch, "E1058", {"start": v(7.61, -4.75) * mm, "end": v(7.48, -4.68) * mm});
            skLineSegment(sketch, "E1059", {"start": v(7.48, -4.68) * mm, "end": v(7.35, -4.6) * mm});
            skLineSegment(sketch, "E1060", {"start": v(7.35, -4.6) * mm, "end": v(7.22, -4.53) * mm});
            skLineSegment(sketch, "E1061", {"start": v(7.22, -4.53) * mm, "end": v(7.11, -4.47) * mm});
            skLineSegment(sketch, "E1062", {"start": v(7.11, -4.47) * mm, "end": v(7.17, -4.33) * mm});
            skLineSegment(sketch, "E1063", {"start": v(7.17, -4.33) * mm, "end": v(7.23, -4.2) * mm});
            skLineSegment(sketch, "E1064", {"start": v(7.23, -4.2) * mm, "end": v(7.3, -4.07) * mm});
            skLineSegment(sketch, "E1065", {"start": v(7.3, -4.07) * mm, "end": v(7.36, -3.93) * mm});
            skLineSegment(sketch, "E1066", {"start": v(7.36, -3.93) * mm, "end": v(7.42, -3.8) * mm});
            skLineSegment(sketch, "E1067", {"start": v(7.42, -3.8) * mm, "end": v(7.48, -3.66) * mm});
            skLineSegment(sketch, "E1068", {"start": v(7.48, -3.66) * mm, "end": v(7.54, -3.53) * mm});
            skLineSegment(sketch, "E1069", {"start": v(7.54, -3.53) * mm, "end": v(7.6, -3.4) * mm});
            skLineSegment(sketch, "E1070", {"start": v(7.6, -3.4) * mm, "end": v(7.66, -3.26) * mm});
            skLineSegment(sketch, "E1071", {"start": v(7.66, -3.26) * mm, "end": v(7.73, -3.12) * mm});
            skLineSegment(sketch, "E1072", {"start": v(7.73, -3.12) * mm, "end": v(7.76, -3.05) * mm});
            skLineSegment(sketch, "E1073", {"start": v(7.76, -3.05) * mm, "end": v(7.9, -3.1) * mm});
            skLineSegment(sketch, "E1074", {"start": v(7.9, -3.1) * mm, "end": v(8.04, -3.15) * mm});
            skLineSegment(sketch, "E1075", {"start": v(8.04, -3.15) * mm, "end": v(8.18, -3.2) * mm});
            skLineSegment(sketch, "E1076", {"start": v(8.18, -3.2) * mm, "end": v(8.32, -3.25) * mm});
            skLineSegment(sketch, "E1077", {"start": v(8.32, -3.25) * mm, "end": v(8.46, -3.3) * mm});
            skLineSegment(sketch, "E1078", {"start": v(8.46, -3.3) * mm, "end": v(8.6, -3.35) * mm});
            skLineSegment(sketch, "E1079", {"start": v(8.6, -3.35) * mm, "end": v(8.74, -3.4) * mm});
            skLineSegment(sketch, "E1080", {"start": v(8.74, -3.4) * mm, "end": v(8.88, -3.45) * mm});
            skLineSegment(sketch, "E1081", {"start": v(8.88, -3.45) * mm, "end": v(9.02, -3.5) * mm});
            skLineSegment(sketch, "E1082", {"start": v(9.02, -3.5) * mm, "end": v(9.16, -3.55) * mm});
            skLineSegment(sketch, "E1083", {"start": v(9.16, -3.55) * mm, "end": v(9.3, -3.6) * mm});
            skLineSegment(sketch, "E1084", {"start": v(9.3, -3.6) * mm, "end": v(9.45, -3.65) * mm});
            skLineSegment(sketch, "E1085", {"start": v(9.45, -3.65) * mm, "end": v(9.6, -3.7) * mm});
            skLineSegment(sketch, "E1086", {"start": v(9.6, -3.7) * mm, "end": v(9.74, -3.72) * mm});
            skLineSegment(sketch, "E1087", {"start": v(9.74, -3.72) * mm, "end": v(9.9, -3.7) * mm});
            skLineSegment(sketch, "E1088", {"start": v(9.9, -3.7) * mm, "end": v(10.03, -3.66) * mm});
            skLineSegment(sketch, "E1089", {"start": v(10.03, -3.66) * mm, "end": v(10.16, -3.58) * mm});
            skLineSegment(sketch, "E1090", {"start": v(10.16, -3.58) * mm, "end": v(10.26, -3.47) * mm});
            skLineSegment(sketch, "E1091", {"start": v(10.26, -3.47) * mm, "end": v(10.34, -3.34) * mm});
            skLineSegment(sketch, "E1092", {"start": v(10.34, -3.34) * mm, "end": v(10.36, -3.28) * mm});
            skLineSegment(sketch, "E1093", {"start": v(10.36, -3.28) * mm, "end": v(10.38, -3.13) * mm});
            skLineSegment(sketch, "E1094", {"start": v(10.38, -3.13) * mm, "end": v(10.37, -2.98) * mm});
            skLineSegment(sketch, "E1095", {"start": v(10.37, -2.98) * mm, "end": v(10.32, -2.84) * mm});
            skLineSegment(sketch, "E1096", {"start": v(10.32, -2.84) * mm, "end": v(10.25, -2.7) * mm});
            skLineSegment(sketch, "E1097", {"start": v(10.25, -2.7) * mm, "end": v(10.14, -2.6) * mm});
            skLineSegment(sketch, "E1098", {"start": v(10.14, -2.6) * mm, "end": v(10.01, -2.53) * mm});
            skLineSegment(sketch, "E1099", {"start": v(10.01, -2.53) * mm, "end": v(9.92, -2.5) * mm});
            skLineSegment(sketch, "E1100", {"start": v(9.92, -2.5) * mm, "end": v(9.77, -2.46) * mm});
            skLineSegment(sketch, "E1101", {"start": v(9.77, -2.46) * mm, "end": v(9.63, -2.43) * mm});
            skLineSegment(sketch, "E1102", {"start": v(9.63, -2.43) * mm, "end": v(9.48, -2.4) * mm});
            skLineSegment(sketch, "E1103", {"start": v(9.48, -2.4) * mm, "end": v(9.34, -2.36) * mm});
            skLineSegment(sketch, "E1104", {"start": v(9.34, -2.36) * mm, "end": v(9.2, -2.33) * mm});
            skLineSegment(sketch, "E1105", {"start": v(9.2, -2.33) * mm, "end": v(9.05, -2.3) * mm});
            skLineSegment(sketch, "E1106", {"start": v(9.05, -2.3) * mm, "end": v(8.9, -2.26) * mm});
            skLineSegment(sketch, "E1107", {"start": v(8.9, -2.26) * mm, "end": v(8.76, -2.22) * mm});
            skLineSegment(sketch, "E1108", {"start": v(8.76, -2.22) * mm, "end": v(8.61, -2.2) * mm});
            skLineSegment(sketch, "E1109", {"start": v(8.61, -2.2) * mm, "end": v(8.47, -2.16) * mm});
            skLineSegment(sketch, "E1110", {"start": v(8.47, -2.16) * mm, "end": v(8.32, -2.12) * mm});
            skLineSegment(sketch, "E1111", {"start": v(8.32, -2.12) * mm, "end": v(8.17, -2.09) * mm});
            skLineSegment(sketch, "E1112", {"start": v(8.17, -2.09) * mm, "end": v(8.05, -2.06) * mm});
            skLineSegment(sketch, "E1113", {"start": v(8.05, -2.06) * mm, "end": v(8.07, -1.91) * mm});
            skLineSegment(sketch, "E1114", {"start": v(8.07, -1.91) * mm, "end": v(8.1, -1.77) * mm});
            skLineSegment(sketch, "E1115", {"start": v(8.1, -1.77) * mm, "end": v(8.11, -1.62) * mm});
            skLineSegment(sketch, "E1116", {"start": v(8.11, -1.62) * mm, "end": v(8.13, -1.47) * mm});
            skLineSegment(sketch, "E1117", {"start": v(8.13, -1.47) * mm, "end": v(8.16, -1.33) * mm});
            skLineSegment(sketch, "E1118", {"start": v(8.16, -1.33) * mm, "end": v(8.18, -1.18) * mm});
            skLineSegment(sketch, "E1119", {"start": v(8.18, -1.18) * mm, "end": v(8.2, -1.04) * mm});
            skLineSegment(sketch, "E1120", {"start": v(8.2, -1.04) * mm, "end": v(8.22, -0.89) * mm});
            skLineSegment(sketch, "E1121", {"start": v(8.22, -0.89) * mm, "end": v(8.24, -0.74) * mm});
            skLineSegment(sketch, "E1122", {"start": v(8.24, -0.74) * mm, "end": v(8.26, -0.6) * mm});
            skLineSegment(sketch, "E1123", {"start": v(8.26, -0.6) * mm, "end": v(8.27, -0.52) * mm});
            skLineSegment(sketch, "E1124", {"start": v(-8.9, 0.54) * mm, "end": v(-8.8, 0.58) * mm});
            skLineSegment(sketch, "E1125", {"start": v(-8.8, 0.58) * mm, "end": v(-8.7, 0.63) * mm});
            skLineSegment(sketch, "E1126", {"start": v(-8.7, 0.63) * mm, "end": v(-8.59, 0.66) * mm});
            skLineSegment(sketch, "E1127", {"start": v(-8.59, 0.66) * mm, "end": v(-8.49, 0.7) * mm});
            skLineSegment(sketch, "E1128", {"start": v(-8.49, 0.7) * mm, "end": v(-8.39, 0.74) * mm});
            skLineSegment(sketch, "E1129", {"start": v(-8.39, 0.74) * mm, "end": v(-8.28, 0.78) * mm});
            skLineSegment(sketch, "E1130", {"start": v(-8.28, 0.78) * mm, "end": v(-8.18, 0.8) * mm});
            skLineSegment(sketch, "E1131", {"start": v(-8.18, 0.8) * mm, "end": v(-8.08, 0.84) * mm});
            skLineSegment(sketch, "E1132", {"start": v(-8.08, 0.84) * mm, "end": v(-7.98, 0.87) * mm});
            skLineSegment(sketch, "E1133", {"start": v(-7.98, 0.87) * mm, "end": v(-7.88, 0.9) * mm});
            skLineSegment(sketch, "E1134", {"start": v(-7.88, 0.9) * mm, "end": v(-7.77, 0.93) * mm});
            skLineSegment(sketch, "E1135", {"start": v(-7.77, 0.93) * mm, "end": v(-7.67, 0.96) * mm});
            skLineSegment(sketch, "E1136", {"start": v(-7.67, 0.96) * mm, "end": v(-7.57, 0.98) * mm});
            skLineSegment(sketch, "E1137", {"start": v(-7.57, 0.98) * mm, "end": v(-7.47, 1) * mm});
            skLineSegment(sketch, "E1138", {"start": v(-7.47, 1) * mm, "end": v(-7.36, 1.03) * mm});
            skLineSegment(sketch, "E1139", {"start": v(-7.36, 1.03) * mm, "end": v(-7.26, 1.05) * mm});
            skLineSegment(sketch, "E1140", {"start": v(-7.26, 1.05) * mm, "end": v(-7.16, 1.07) * mm});
            skLineSegment(sketch, "E1141", {"start": v(-7.16, 1.07) * mm, "end": v(-7.06, 1.09) * mm});
            skLineSegment(sketch, "E1142", {"start": v(-7.06, 1.09) * mm, "end": v(-6.95, 1.1) * mm});
            skLineSegment(sketch, "E1143", {"start": v(-6.95, 1.1) * mm, "end": v(-6.85, 1.12) * mm});
            skLineSegment(sketch, "E1144", {"start": v(-6.85, 1.12) * mm, "end": v(-6.75, 1.14) * mm});
            skLineSegment(sketch, "E1145", {"start": v(-6.75, 1.14) * mm, "end": v(-6.64, 1.15) * mm});
            skLineSegment(sketch, "E1146", {"start": v(-6.64, 1.15) * mm, "end": v(-6.54, 1.16) * mm});
            skLineSegment(sketch, "E1147", {"start": v(-6.54, 1.16) * mm, "end": v(-6.44, 1.17) * mm});
            skLineSegment(sketch, "E1148", {"start": v(-6.44, 1.17) * mm, "end": v(-6.33, 1.18) * mm});
            skLineSegment(sketch, "E1149", {"start": v(-6.33, 1.18) * mm, "end": v(-6.23, 1.18) * mm});
            skLineSegment(sketch, "E1150", {"start": v(-6.23, 1.18) * mm, "end": v(-6.12, 1.19) * mm});
            skLineSegment(sketch, "E1151", {"start": v(-6.12, 1.19) * mm, "end": v(-6.02, 1.2) * mm});
            skLineSegment(sketch, "E1152", {"start": v(-6.02, 1.2) * mm, "end": v(-5.92, 1.2) * mm});
            skLineSegment(sketch, "E1153", {"start": v(-5.92, 1.2) * mm, "end": v(-5.81, 1.2) * mm});
            skLineSegment(sketch, "E1154", {"start": v(-5.81, 1.2) * mm, "end": v(-5.7, 1.2) * mm});
            skLineSegment(sketch, "E1155", {"start": v(-5.7, 1.2) * mm, "end": v(-5.6, 1.2) * mm});
            skLineSegment(sketch, "E1156", {"start": v(-5.6, 1.2) * mm, "end": v(-5.5, 1.19) * mm});
            skLineSegment(sketch, "E1157", {"start": v(-5.5, 1.19) * mm, "end": v(-5.4, 1.18) * mm});
            skLineSegment(sketch, "E1158", {"start": v(-5.4, 1.18) * mm, "end": v(-5.3, 1.18) * mm});
            skLineSegment(sketch, "E1159", {"start": v(-5.3, 1.18) * mm, "end": v(-5.2, 1.17) * mm});
            skLineSegment(sketch, "E1160", {"start": v(-5.2, 1.17) * mm, "end": v(-5.1, 1.16) * mm});
            skLineSegment(sketch, "E1161", {"start": v(-5.1, 1.16) * mm, "end": v(-5, 1.15) * mm});
            skLineSegment(sketch, "E1162", {"start": v(-5, 1.15) * mm, "end": v(-4.9, 1.14) * mm});
            skLineSegment(sketch, "E1163", {"start": v(-4.9, 1.14) * mm, "end": v(-4.79, 1.12) * mm});
            skLineSegment(sketch, "E1164", {"start": v(-4.79, 1.12) * mm, "end": v(-4.69, 1.1) * mm});
            skLineSegment(sketch, "E1165", {"start": v(-4.69, 1.1) * mm, "end": v(-4.59, 1.1) * mm});
            skLineSegment(sketch, "E1166", {"start": v(-4.59, 1.1) * mm, "end": v(-4.48, 1.07) * mm});
            skLineSegment(sketch, "E1167", {"start": v(-4.48, 1.07) * mm, "end": v(-4.38, 1.06) * mm});
            skLineSegment(sketch, "E1168", {"start": v(-4.38, 1.06) * mm, "end": v(-4.28, 1.03) * mm});
            skLineSegment(sketch, "E1169", {"start": v(-4.28, 1.03) * mm, "end": v(-4.18, 1.01) * mm});
            skLineSegment(sketch, "E1170", {"start": v(-4.18, 1.01) * mm, "end": v(-4.08, 0.99) * mm});
            skLineSegment(sketch, "E1171", {"start": v(-4.08, 0.99) * mm, "end": v(-3.98, 0.96) * mm});
            skLineSegment(sketch, "E1172", {"start": v(-3.98, 0.96) * mm, "end": v(-3.88, 0.94) * mm});
            skLineSegment(sketch, "E1173", {"start": v(-3.88, 0.94) * mm, "end": v(-3.78, 0.91) * mm});
            skLineSegment(sketch, "E1174", {"start": v(-3.78, 0.91) * mm, "end": v(-3.68, 0.88) * mm});
            skLineSegment(sketch, "E1175", {"start": v(-3.68, 0.88) * mm, "end": v(-3.57, 0.85) * mm});
            skLineSegment(sketch, "E1176", {"start": v(-3.57, 0.85) * mm, "end": v(-3.47, 0.82) * mm});
            skLineSegment(sketch, "E1177", {"start": v(-3.47, 0.82) * mm, "end": v(-3.37, 0.79) * mm});
            skLineSegment(sketch, "E1178", {"start": v(-3.37, 0.79) * mm, "end": v(-3.27, 0.75) * mm});
            skLineSegment(sketch, "E1179", {"start": v(-3.27, 0.75) * mm, "end": v(-3.17, 0.72) * mm});
            skLineSegment(sketch, "E1180", {"start": v(-3.17, 0.72) * mm, "end": v(-3.07, 0.68) * mm});
            skLineSegment(sketch, "E1181", {"start": v(-3.07, 0.68) * mm, "end": v(-2.97, 0.64) * mm});
            skLineSegment(sketch, "E1182", {"start": v(-2.97, 0.64) * mm, "end": v(-2.87, 0.6) * mm});
            skLineSegment(sketch, "E1183", {"start": v(-2.87, 0.6) * mm, "end": v(-2.82, 0.58) * mm});
            skLineSegment(sketch, "E1184", {"start": v(-2.82, 0.58) * mm, "end": v(-2.8, 0.65) * mm});
            skLineSegment(sketch, "E1185", {"start": v(-2.8, 0.65) * mm, "end": v(-2.76, 0.78) * mm});
            skLineSegment(sketch, "E1186", {"start": v(-2.76, 0.78) * mm, "end": v(-2.7, 0.9) * mm});
            skLineSegment(sketch, "E1187", {"start": v(-2.7, 0.9) * mm, "end": v(-2.64, 1.02) * mm});
            skLineSegment(sketch, "E1188", {"start": v(-2.64, 1.02) * mm, "end": v(-2.58, 1.13) * mm});
            skLineSegment(sketch, "E1189", {"start": v(-2.58, 1.13) * mm, "end": v(-2.5, 1.24) * mm});
            skLineSegment(sketch, "E1190", {"start": v(-2.5, 1.24) * mm, "end": v(-2.42, 1.34) * mm});
            skLineSegment(sketch, "E1191", {"start": v(-2.42, 1.34) * mm, "end": v(-2.33, 1.44) * mm});
            skLineSegment(sketch, "E1192", {"start": v(-2.33, 1.44) * mm, "end": v(-2.24, 1.54) * mm});
            skLineSegment(sketch, "E1193", {"start": v(-2.24, 1.54) * mm, "end": v(-2.14, 1.62) * mm});
            skLineSegment(sketch, "E1194", {"start": v(-2.14, 1.62) * mm, "end": v(-2.03, 1.7) * mm});
            skLineSegment(sketch, "E1195", {"start": v(-2.03, 1.7) * mm, "end": v(-1.93, 1.78) * mm});
            skLineSegment(sketch, "E1196", {"start": v(-1.93, 1.78) * mm, "end": v(-1.81, 1.85) * mm});
            skLineSegment(sketch, "E1197", {"start": v(-1.81, 1.85) * mm, "end": v(-1.7, 1.9) * mm});
            skLineSegment(sketch, "E1198", {"start": v(-1.7, 1.9) * mm, "end": v(-1.57, 1.96) * mm});
            skLineSegment(sketch, "E1199", {"start": v(-1.57, 1.96) * mm, "end": v(-1.45, 2) * mm});
            skLineSegment(sketch, "E1200", {"start": v(-1.45, 2) * mm, "end": v(-1.33, 2.04) * mm});
            skLineSegment(sketch, "E1201", {"start": v(-1.33, 2.04) * mm, "end": v(-1.35, 2.08) * mm});
            skLineSegment(sketch, "E1202", {"start": v(-1.35, 2.08) * mm, "end": v(-1.4, 2.18) * mm});
            skLineSegment(sketch, "E1203", {"start": v(-1.4, 2.18) * mm, "end": v(-1.44, 2.28) * mm});
            skLineSegment(sketch, "E1204", {"start": v(-1.44, 2.28) * mm, "end": v(-1.49, 2.38) * mm});
            skLineSegment(sketch, "E1205", {"start": v(-1.49, 2.38) * mm, "end": v(-1.53, 2.48) * mm});
            skLineSegment(sketch, "E1206", {"start": v(-1.53, 2.48) * mm, "end": v(-1.57, 2.58) * mm});
            skLineSegment(sketch, "E1207", {"start": v(-1.57, 2.58) * mm, "end": v(-1.6, 2.68) * mm});
            skLineSegment(sketch, "E1208", {"start": v(-1.6, 2.68) * mm, "end": v(-1.64, 2.78) * mm});
            skLineSegment(sketch, "E1209", {"start": v(-1.64, 2.78) * mm, "end": v(-1.68, 2.88) * mm});
            skLineSegment(sketch, "E1210", {"start": v(-1.68, 2.88) * mm, "end": v(-1.71, 2.98) * mm});
            skLineSegment(sketch, "E1211", {"start": v(-1.71, 2.98) * mm, "end": v(-1.75, 3.08) * mm});
            skLineSegment(sketch, "E1212", {"start": v(-1.75, 3.08) * mm, "end": v(-1.78, 3.18) * mm});
            skLineSegment(sketch, "E1213", {"start": v(-1.78, 3.18) * mm, "end": v(-1.8, 3.28) * mm});
            skLineSegment(sketch, "E1214", {"start": v(-1.8, 3.28) * mm, "end": v(-1.83, 3.38) * mm});
            skLineSegment(sketch, "E1215", {"start": v(-1.83, 3.38) * mm, "end": v(-1.86, 3.49) * mm});
            skLineSegment(sketch, "E1216", {"start": v(-1.86, 3.49) * mm, "end": v(-1.88, 3.59) * mm});
            skLineSegment(sketch, "E1217", {"start": v(-1.88, 3.59) * mm, "end": v(-1.9, 3.69) * mm});
            skLineSegment(sketch, "E1218", {"start": v(-1.9, 3.69) * mm, "end": v(-1.92, 3.8) * mm});
            skLineSegment(sketch, "E1219", {"start": v(-1.92, 3.8) * mm, "end": v(-1.94, 3.9) * mm});
            skLineSegment(sketch, "E1220", {"start": v(-1.94, 3.9) * mm, "end": v(-1.96, 4) * mm});
            skLineSegment(sketch, "E1221", {"start": v(-1.96, 4) * mm, "end": v(-1.98, 4.1) * mm});
            skLineSegment(sketch, "E1222", {"start": v(-1.98, 4.1) * mm, "end": v(-2, 4.2) * mm});
            skLineSegment(sketch, "E1223", {"start": v(-2, 4.2) * mm, "end": v(-2, 4.3) * mm});
            skLineSegment(sketch, "E1224", {"start": v(-2, 4.3) * mm, "end": v(-2.01, 4.4) * mm});
            skLineSegment(sketch, "E1225", {"start": v(-2.01, 4.4) * mm, "end": v(-2.02, 4.5) * mm});
            skLineSegment(sketch, "E1226", {"start": v(-2.02, 4.5) * mm, "end": v(-2.03, 4.6) * mm});
            skLineSegment(sketch, "E1227", {"start": v(-2.03, 4.6) * mm, "end": v(-2.04, 4.7) * mm});
            skLineSegment(sketch, "E1228", {"start": v(-2.04, 4.7) * mm, "end": v(-2.04, 4.81) * mm});
            skLineSegment(sketch, "E1229", {"start": v(-2.04, 4.81) * mm, "end": v(-2.04, 4.91) * mm});
            skLineSegment(sketch, "E1230", {"start": v(-2.04, 4.91) * mm, "end": v(-2.04, 5.02) * mm});
            skLineSegment(sketch, "E1231", {"start": v(-2.04, 5.02) * mm, "end": v(-2.04, 5.12) * mm});
            skLineSegment(sketch, "E1232", {"start": v(-2.04, 5.12) * mm, "end": v(-2.04, 5.22) * mm});
            skLineSegment(sketch, "E1233", {"start": v(-2.04, 5.22) * mm, "end": v(-2.04, 5.33) * mm});
            skLineSegment(sketch, "E1234", {"start": v(-2.04, 5.33) * mm, "end": v(-2.03, 5.43) * mm});
            skLineSegment(sketch, "E1235", {"start": v(-2.03, 5.43) * mm, "end": v(-2.02, 5.54) * mm});
            skLineSegment(sketch, "E1236", {"start": v(-2.02, 5.54) * mm, "end": v(-2.01, 5.64) * mm});
            skLineSegment(sketch, "E1237", {"start": v(-2.01, 5.64) * mm, "end": v(-2, 5.74) * mm});
            skLineSegment(sketch, "E1238", {"start": v(-2, 5.74) * mm, "end": v(-1.99, 5.85) * mm});
            skLineSegment(sketch, "E1239", {"start": v(-1.99, 5.85) * mm, "end": v(-1.97, 5.95) * mm});
            skLineSegment(sketch, "E1240", {"start": v(-1.97, 5.95) * mm, "end": v(-1.96, 6.05) * mm});
            skLineSegment(sketch, "E1241", {"start": v(-1.96, 6.05) * mm, "end": v(-1.94, 6.16) * mm});
            skLineSegment(sketch, "E1242", {"start": v(-1.94, 6.16) * mm, "end": v(-1.92, 6.26) * mm});
            skLineSegment(sketch, "E1243", {"start": v(-1.92, 6.26) * mm, "end": v(-1.9, 6.36) * mm});
            skLineSegment(sketch, "E1244", {"start": v(-1.9, 6.36) * mm, "end": v(-1.88, 6.46) * mm});
            skLineSegment(sketch, "E1245", {"start": v(-1.88, 6.46) * mm, "end": v(-1.85, 6.57) * mm});
            skLineSegment(sketch, "E1246", {"start": v(-1.85, 6.57) * mm, "end": v(-1.83, 6.67) * mm});
            skLineSegment(sketch, "E1247", {"start": v(-1.83, 6.67) * mm, "end": v(-1.8, 6.77) * mm});
            skLineSegment(sketch, "E1248", {"start": v(-1.8, 6.77) * mm, "end": v(-1.77, 6.88) * mm});
            skLineSegment(sketch, "E1249", {"start": v(-1.77, 6.88) * mm, "end": v(-1.74, 6.98) * mm});
            skLineSegment(sketch, "E1250", {"start": v(-1.74, 6.98) * mm, "end": v(-1.7, 7.08) * mm});
            skLineSegment(sketch, "E1251", {"start": v(-1.7, 7.08) * mm, "end": v(-1.67, 7.18) * mm});
            skLineSegment(sketch, "E1252", {"start": v(-1.67, 7.18) * mm, "end": v(-1.63, 7.28) * mm});
            skLineSegment(sketch, "E1253", {"start": v(-1.63, 7.28) * mm, "end": v(-1.6, 7.39) * mm});
            skLineSegment(sketch, "E1254", {"start": v(-1.6, 7.39) * mm, "end": v(-1.56, 7.49) * mm});
            skLineSegment(sketch, "E1255", {"start": v(-1.56, 7.49) * mm, "end": v(-1.51, 7.6) * mm});
            skLineSegment(sketch, "E1256", {"start": v(-1.51, 7.6) * mm, "end": v(-1.47, 7.7) * mm});
            skLineSegment(sketch, "E1257", {"start": v(-1.47, 7.7) * mm, "end": v(-1.43, 7.8) * mm});
            skLineSegment(sketch, "E1258", {"start": v(-1.43, 7.8) * mm, "end": v(-1.38, 7.9) * mm});
            skLineSegment(sketch, "E1259", {"start": v(-1.38, 7.9) * mm, "end": v(-1.33, 8) * mm});
            skLineSegment(sketch, "E1260", {"start": v(-1.33, 8) * mm, "end": v(-1.28, 8.1) * mm});
            skLineSegment(sketch, "E1261", {"start": v(-1.28, 8.1) * mm, "end": v(-1.25, 8.16) * mm});
            skLineSegment(sketch, "E1262", {"start": v(-1.25, 8.16) * mm, "end": v(-1.3, 8.16) * mm});
            skLineSegment(sketch, "E1263", {"start": v(-1.3, 8.16) * mm, "end": v(-1.82, 8.1) * mm});
            skLineSegment(sketch, "E1264", {"start": v(-1.82, 8.1) * mm, "end": v(-2.33, 8.03) * mm});
            skLineSegment(sketch, "E1265", {"start": v(-2.33, 8.03) * mm, "end": v(-2.83, 7.92) * mm});
            skLineSegment(sketch, "E1266", {"start": v(-2.83, 7.92) * mm, "end": v(-3.32, 7.77) * mm});
            skLineSegment(sketch, "E1267", {"start": v(-3.32, 7.77) * mm, "end": v(-3.8, 7.6) * mm});
            skLineSegment(sketch, "E1268", {"start": v(-3.8, 7.6) * mm, "end": v(-4.28, 7.4) * mm});
            skLineSegment(sketch, "E1269", {"start": v(-4.28, 7.4) * mm, "end": v(-4.73, 7.16) * mm});
            skLineSegment(sketch, "E1270", {"start": v(-4.73, 7.16) * mm, "end": v(-5.18, 6.9) * mm});
            skLineSegment(sketch, "E1271", {"start": v(-5.18, 6.9) * mm, "end": v(-5.6, 6.61) * mm});
            skLineSegment(sketch, "E1272", {"start": v(-5.6, 6.61) * mm, "end": v(-6, 6.3) * mm});
            skLineSegment(sketch, "E1273", {"start": v(-6, 6.3) * mm, "end": v(-6.4, 5.96) * mm});
            skLineSegment(sketch, "E1274", {"start": v(-6.4, 5.96) * mm, "end": v(-6.75, 5.6) * mm});
            skLineSegment(sketch, "E1275", {"start": v(-6.75, 5.6) * mm, "end": v(-7.1, 5.2) * mm});
            skLineSegment(sketch, "E1276", {"start": v(-7.1, 5.2) * mm, "end": v(-7.4, 4.8) * mm});
            skLineSegment(sketch, "E1277", {"start": v(-7.4, 4.8) * mm, "end": v(-7.7, 4.38) * mm});
            skLineSegment(sketch, "E1278", {"start": v(-7.7, 4.38) * mm, "end": v(-7.96, 3.94) * mm});
            skLineSegment(sketch, "E1279", {"start": v(-7.96, 3.94) * mm, "end": v(-8.2, 3.48) * mm});
            skLineSegment(sketch, "E1280", {"start": v(-8.2, 3.48) * mm, "end": v(-8.4, 3) * mm});
            skLineSegment(sketch, "E1281", {"start": v(-8.4, 3) * mm, "end": v(-8.57, 2.53) * mm});
            skLineSegment(sketch, "E1282", {"start": v(-8.57, 2.53) * mm, "end": v(-8.71, 2.03) * mm});
            skLineSegment(sketch, "E1283", {"start": v(-8.71, 2.03) * mm, "end": v(-8.82, 1.53) * mm});
            skLineSegment(sketch, "E1284", {"start": v(-8.82, 1.53) * mm, "end": v(-8.9, 1.02) * mm});
            skLineSegment(sketch, "E1285", {"start": v(-8.9, 1.02) * mm, "end": v(-8.95, 0.52) * mm});
            skLineSegment(sketch, "E1286", {"start": v(-8.95, 0.52) * mm, "end": v(-8.9, 0.54) * mm});
            skLineSegment(sketch, "E1287", {"start": v(7.36, 0.51) * mm, "end": v(7.31, 1.02) * mm});
            skLineSegment(sketch, "E1288", {"start": v(7.31, 1.02) * mm, "end": v(7.23, 1.53) * mm});
            skLineSegment(sketch, "E1289", {"start": v(7.23, 1.53) * mm, "end": v(7.12, 2.03) * mm});
            skLineSegment(sketch, "E1290", {"start": v(7.12, 2.03) * mm, "end": v(6.98, 2.53) * mm});
            skLineSegment(sketch, "E1291", {"start": v(6.98, 2.53) * mm, "end": v(6.8, 3) * mm});
            skLineSegment(sketch, "E1292", {"start": v(6.8, 3) * mm, "end": v(6.6, 3.48) * mm});
            skLineSegment(sketch, "E1293", {"start": v(6.6, 3.48) * mm, "end": v(6.37, 3.94) * mm});
            skLineSegment(sketch, "E1294", {"start": v(6.37, 3.94) * mm, "end": v(6.1, 4.38) * mm});
            skLineSegment(sketch, "E1295", {"start": v(6.1, 4.38) * mm, "end": v(5.82, 4.8) * mm});
            skLineSegment(sketch, "E1296", {"start": v(5.82, 4.8) * mm, "end": v(5.5, 5.2) * mm});
            skLineSegment(sketch, "E1297", {"start": v(5.5, 5.2) * mm, "end": v(5.16, 5.6) * mm});
            skLineSegment(sketch, "E1298", {"start": v(5.16, 5.6) * mm, "end": v(4.8, 5.96) * mm});
            skLineSegment(sketch, "E1299", {"start": v(4.8, 5.96) * mm, "end": v(4.41, 6.3) * mm});
            skLineSegment(sketch, "E1300", {"start": v(4.41, 6.3) * mm, "end": v(4, 6.61) * mm});
            skLineSegment(sketch, "E1301", {"start": v(4, 6.61) * mm, "end": v(3.58, 6.9) * mm});
            skLineSegment(sketch, "E1302", {"start": v(3.58, 6.9) * mm, "end": v(3.14, 7.16) * mm});
            skLineSegment(sketch, "E1303", {"start": v(3.14, 7.16) * mm, "end": v(2.68, 7.4) * mm});
            skLineSegment(sketch, "E1304", {"start": v(2.68, 7.4) * mm, "end": v(2.21, 7.6) * mm});
            skLineSegment(sketch, "E1305", {"start": v(2.21, 7.6) * mm, "end": v(1.73, 7.77) * mm});
            skLineSegment(sketch, "E1306", {"start": v(1.73, 7.77) * mm, "end": v(1.24, 7.92) * mm});
            skLineSegment(sketch, "E1307", {"start": v(1.24, 7.92) * mm, "end": v(0.74, 8.03) * mm});
            skLineSegment(sketch, "E1308", {"start": v(0.74, 8.03) * mm, "end": v(0.23, 8.1) * mm});
            skLineSegment(sketch, "E1309", {"start": v(0.23, 8.1) * mm, "end": v(-0.28, 8.16) * mm});
            skLineSegment(sketch, "E1310", {"start": v(-0.28, 8.16) * mm, "end": v(-0.25, 8.1) * mm});
            skLineSegment(sketch, "E1311", {"start": v(-0.25, 8.1) * mm, "end": v(-0.21, 8) * mm});
            skLineSegment(sketch, "E1312", {"start": v(-0.21, 8) * mm, "end": v(-0.17, 7.9) * mm});
            skLineSegment(sketch, "E1313", {"start": v(-0.17, 7.9) * mm, "end": v(-0.13, 7.8) * mm});
            skLineSegment(sketch, "E1314", {"start": v(-0.13, 7.8) * mm, "end": v(-0.1, 7.7) * mm});
            skLineSegment(sketch, "E1315", {"start": v(-0.1, 7.7) * mm, "end": v(-0.06, 7.6) * mm});
            skLineSegment(sketch, "E1316", {"start": v(-0.06, 7.6) * mm, "end": v(-0.02, 7.49) * mm});
            skLineSegment(sketch, "E1317", {"start": v(-0.02, 7.49) * mm, "end": v(0.01, 7.39) * mm});
            skLineSegment(sketch, "E1318", {"start": v(0.01, 7.39) * mm, "end": v(0.05, 7.28) * mm});
            skLineSegment(sketch, "E1319", {"start": v(0.05, 7.28) * mm, "end": v(0.08, 7.18) * mm});
            skLineSegment(sketch, "E1320", {"start": v(0.08, 7.18) * mm, "end": v(0.1, 7.08) * mm});
            skLineSegment(sketch, "E1321", {"start": v(0.1, 7.08) * mm, "end": v(0.14, 6.98) * mm});
            skLineSegment(sketch, "E1322", {"start": v(0.14, 6.98) * mm, "end": v(0.16, 6.88) * mm});
            skLineSegment(sketch, "E1323", {"start": v(0.16, 6.88) * mm, "end": v(0.19, 6.77) * mm});
            skLineSegment(sketch, "E1324", {"start": v(0.19, 6.77) * mm, "end": v(0.21, 6.67) * mm});
            skLineSegment(sketch, "E1325", {"start": v(0.21, 6.67) * mm, "end": v(0.23, 6.57) * mm});
            skLineSegment(sketch, "E1326", {"start": v(0.23, 6.57) * mm, "end": v(0.26, 6.46) * mm});
            skLineSegment(sketch, "E1327", {"start": v(0.26, 6.46) * mm, "end": v(0.28, 6.36) * mm});
            skLineSegment(sketch, "E1328", {"start": v(0.28, 6.36) * mm, "end": v(0.3, 6.26) * mm});
            skLineSegment(sketch, "E1329", {"start": v(0.3, 6.26) * mm, "end": v(0.31, 6.16) * mm});
            skLineSegment(sketch, "E1330", {"start": v(0.31, 6.16) * mm, "end": v(0.33, 6.05) * mm});
            skLineSegment(sketch, "E1331", {"start": v(0.33, 6.05) * mm, "end": v(0.34, 5.95) * mm});
            skLineSegment(sketch, "E1332", {"start": v(0.34, 5.95) * mm, "end": v(0.35, 5.85) * mm});
            skLineSegment(sketch, "E1333", {"start": v(0.35, 5.85) * mm, "end": v(0.36, 5.74) * mm});
            skLineSegment(sketch, "E1334", {"start": v(0.36, 5.74) * mm, "end": v(0.37, 5.64) * mm});
            skLineSegment(sketch, "E1335", {"start": v(0.37, 5.64) * mm, "end": v(0.38, 5.54) * mm});
            skLineSegment(sketch, "E1336", {"start": v(0.38, 5.54) * mm, "end": v(0.39, 5.43) * mm});
            skLineSegment(sketch, "E1337", {"start": v(0.39, 5.43) * mm, "end": v(0.4, 5.33) * mm});
            skLineSegment(sketch, "E1338", {"start": v(0.4, 5.33) * mm, "end": v(0.4, 5.22) * mm});
            skLineSegment(sketch, "E1339", {"start": v(0.4, 5.22) * mm, "end": v(0.4, 5.12) * mm});
            skLineSegment(sketch, "E1340", {"start": v(0.4, 5.12) * mm, "end": v(0.4, 5.02) * mm});
            skLineSegment(sketch, "E1341", {"start": v(0.4, 5.02) * mm, "end": v(0.4, 4.91) * mm});
            skLineSegment(sketch, "E1342", {"start": v(0.4, 4.91) * mm, "end": v(0.4, 4.81) * mm});
            skLineSegment(sketch, "E1343", {"start": v(0.4, 4.81) * mm, "end": v(0.4, 4.7) * mm});
            skLineSegment(sketch, "E1344", {"start": v(0.4, 4.7) * mm, "end": v(0.39, 4.6) * mm});
            skLineSegment(sketch, "E1345", {"start": v(0.39, 4.6) * mm, "end": v(0.38, 4.5) * mm});
            skLineSegment(sketch, "E1346", {"start": v(0.38, 4.5) * mm, "end": v(0.37, 4.4) * mm});
            skLineSegment(sketch, "E1347", {"start": v(0.37, 4.4) * mm, "end": v(0.36, 4.3) * mm});
            skLineSegment(sketch, "E1348", {"start": v(0.36, 4.3) * mm, "end": v(0.35, 4.2) * mm});
            skLineSegment(sketch, "E1349", {"start": v(0.35, 4.2) * mm, "end": v(0.34, 4.1) * mm});
            skLineSegment(sketch, "E1350", {"start": v(0.34, 4.1) * mm, "end": v(0.33, 4) * mm});
            skLineSegment(sketch, "E1351", {"start": v(0.33, 4) * mm, "end": v(0.31, 3.9) * mm});
            skLineSegment(sketch, "E1352", {"start": v(0.31, 3.9) * mm, "end": v(0.3, 3.8) * mm});
            skLineSegment(sketch, "E1353", {"start": v(0.3, 3.8) * mm, "end": v(0.28, 3.69) * mm});
            skLineSegment(sketch, "E1354", {"start": v(0.28, 3.69) * mm, "end": v(0.26, 3.59) * mm});
            skLineSegment(sketch, "E1355", {"start": v(0.26, 3.59) * mm, "end": v(0.24, 3.49) * mm});
            skLineSegment(sketch, "E1356", {"start": v(0.24, 3.49) * mm, "end": v(0.22, 3.38) * mm});
            skLineSegment(sketch, "E1357", {"start": v(0.22, 3.38) * mm, "end": v(0.2, 3.28) * mm});
            skLineSegment(sketch, "E1358", {"start": v(0.2, 3.28) * mm, "end": v(0.17, 3.18) * mm});
            skLineSegment(sketch, "E1359", {"start": v(0.17, 3.18) * mm, "end": v(0.14, 3.08) * mm});
            skLineSegment(sketch, "E1360", {"start": v(0.14, 3.08) * mm, "end": v(0.12, 2.98) * mm});
            skLineSegment(sketch, "E1361", {"start": v(0.12, 2.98) * mm, "end": v(0.09, 2.88) * mm});
            skLineSegment(sketch, "E1362", {"start": v(0.09, 2.88) * mm, "end": v(0.06, 2.78) * mm});
            skLineSegment(sketch, "E1363", {"start": v(0.06, 2.78) * mm, "end": v(0.02, 2.68) * mm});
            skLineSegment(sketch, "E1364", {"start": v(0.02, 2.68) * mm, "end": v(0, 2.58) * mm});
            skLineSegment(sketch, "E1365", {"start": v(0, 2.58) * mm, "end": v(-0.04, 2.48) * mm});
            skLineSegment(sketch, "E1366", {"start": v(-0.04, 2.48) * mm, "end": v(-0.08, 2.38) * mm});
            skLineSegment(sketch, "E1367", {"start": v(-0.08, 2.38) * mm, "end": v(-0.12, 2.28) * mm});
            skLineSegment(sketch, "E1368", {"start": v(-0.12, 2.28) * mm, "end": v(-0.15, 2.18) * mm});
            skLineSegment(sketch, "E1369", {"start": v(-0.15, 2.18) * mm, "end": v(-0.2, 2.08) * mm});
            skLineSegment(sketch, "E1370", {"start": v(-0.2, 2.08) * mm, "end": v(-0.22, 2.03) * mm});
            skLineSegment(sketch, "E1371", {"start": v(-0.22, 2.03) * mm, "end": v(-0.14, 2) * mm});
            skLineSegment(sketch, "E1372", {"start": v(-0.14, 2) * mm, "end": v(-0.02, 1.96) * mm});
            skLineSegment(sketch, "E1373", {"start": v(-0.02, 1.96) * mm, "end": v(0.1, 1.9) * mm});
            skLineSegment(sketch, "E1374", {"start": v(0.1, 1.9) * mm, "end": v(0.22, 1.85) * mm});
            skLineSegment(sketch, "E1375", {"start": v(0.22, 1.85) * mm, "end": v(0.33, 1.78) * mm});
            skLineSegment(sketch, "E1376", {"start": v(0.33, 1.78) * mm, "end": v(0.44, 1.7) * mm});
            skLineSegment(sketch, "E1377", {"start": v(0.44, 1.7) * mm, "end": v(0.55, 1.62) * mm});
            skLineSegment(sketch, "E1378", {"start": v(0.55, 1.62) * mm, "end": v(0.65, 1.54) * mm});
            skLineSegment(sketch, "E1379", {"start": v(0.65, 1.54) * mm, "end": v(0.74, 1.44) * mm});
            skLineSegment(sketch, "E1380", {"start": v(0.74, 1.44) * mm, "end": v(0.83, 1.34) * mm});
            skLineSegment(sketch, "E1381", {"start": v(0.83, 1.34) * mm, "end": v(0.9, 1.24) * mm});
            skLineSegment(sketch, "E1382", {"start": v(0.9, 1.24) * mm, "end": v(0.98, 1.13) * mm});
            skLineSegment(sketch, "E1383", {"start": v(0.98, 1.13) * mm, "end": v(1.05, 1.02) * mm});
            skLineSegment(sketch, "E1384", {"start": v(1.05, 1.02) * mm, "end": v(1.11, 0.9) * mm});
            skLineSegment(sketch, "E1385", {"start": v(1.11, 0.9) * mm, "end": v(1.16, 0.78) * mm});
            skLineSegment(sketch, "E1386", {"start": v(1.16, 0.78) * mm, "end": v(1.2, 0.65) * mm});
            skLineSegment(sketch, "E1387", {"start": v(1.2, 0.65) * mm, "end": v(1.24, 0.54) * mm});
            skLineSegment(sketch, "E1388", {"start": v(1.24, 0.54) * mm, "end": v(1.28, 0.56) * mm});
            skLineSegment(sketch, "E1389", {"start": v(1.28, 0.56) * mm, "end": v(1.38, 0.6) * mm});
            skLineSegment(sketch, "E1390", {"start": v(1.38, 0.6) * mm, "end": v(1.48, 0.65) * mm});
            skLineSegment(sketch, "E1391", {"start": v(1.48, 0.65) * mm, "end": v(1.58, 0.7) * mm});
            skLineSegment(sketch, "E1392", {"start": v(1.58, 0.7) * mm, "end": v(1.68, 0.73) * mm});
            skLineSegment(sketch, "E1393", {"start": v(1.68, 0.73) * mm, "end": v(1.78, 0.77) * mm});
            skLineSegment(sketch, "E1394", {"start": v(1.78, 0.77) * mm, "end": v(1.88, 0.81) * mm});
            skLineSegment(sketch, "E1395", {"start": v(1.88, 0.81) * mm, "end": v(1.98, 0.85) * mm});
            skLineSegment(sketch, "E1396", {"start": v(1.98, 0.85) * mm, "end": v(2.08, 0.88) * mm});
            skLineSegment(sketch, "E1397", {"start": v(2.08, 0.88) * mm, "end": v(2.18, 0.92) * mm});
            skLineSegment(sketch, "E1398", {"start": v(2.18, 0.92) * mm, "end": v(2.29, 0.95) * mm});
            skLineSegment(sketch, "E1399", {"start": v(2.29, 0.95) * mm, "end": v(2.39, 0.98) * mm});
            skLineSegment(sketch, "E1400", {"start": v(2.39, 0.98) * mm, "end": v(2.49, 1) * mm});
            skLineSegment(sketch, "E1401", {"start": v(2.49, 1) * mm, "end": v(2.59, 1.04) * mm});
            skLineSegment(sketch, "E1402", {"start": v(2.59, 1.04) * mm, "end": v(2.7, 1.06) * mm});
            skLineSegment(sketch, "E1403", {"start": v(2.7, 1.06) * mm, "end": v(2.8, 1.09) * mm});
            skLineSegment(sketch, "E1404", {"start": v(2.8, 1.09) * mm, "end": v(2.9, 1.1) * mm});
            skLineSegment(sketch, "E1405", {"start": v(2.9, 1.1) * mm, "end": v(3, 1.13) * mm});
            skLineSegment(sketch, "E1406", {"start": v(3, 1.13) * mm, "end": v(3.1, 1.15) * mm});
            skLineSegment(sketch, "E1407", {"start": v(3.1, 1.15) * mm, "end": v(3.2, 1.16) * mm});
            skLineSegment(sketch, "E1408", {"start": v(3.2, 1.16) * mm, "end": v(3.3, 1.18) * mm});
            skLineSegment(sketch, "E1409", {"start": v(3.3, 1.18) * mm, "end": v(3.4, 1.2) * mm});
            skLineSegment(sketch, "E1410", {"start": v(3.4, 1.2) * mm, "end": v(3.5, 1.2) * mm});
            skLineSegment(sketch, "E1411", {"start": v(3.5, 1.2) * mm, "end": v(3.6, 1.22) * mm});
            skLineSegment(sketch, "E1412", {"start": v(3.6, 1.22) * mm, "end": v(3.7, 1.23) * mm});
            skLineSegment(sketch, "E1413", {"start": v(3.7, 1.23) * mm, "end": v(3.81, 1.23) * mm});
            skLineSegment(sketch, "E1414", {"start": v(3.81, 1.23) * mm, "end": v(3.91, 1.24) * mm});
            skLineSegment(sketch, "E1415", {"start": v(3.91, 1.24) * mm, "end": v(4.02, 1.24) * mm});
            skLineSegment(sketch, "E1416", {"start": v(4.02, 1.24) * mm, "end": v(4.12, 1.25) * mm});
            skLineSegment(sketch, "E1417", {"start": v(4.12, 1.25) * mm, "end": v(4.22, 1.25) * mm});
            skLineSegment(sketch, "E1418", {"start": v(4.22, 1.25) * mm, "end": v(4.32, 1.25) * mm});
            skLineSegment(sketch, "E1419", {"start": v(4.32, 1.25) * mm, "end": v(4.43, 1.24) * mm});
            skLineSegment(sketch, "E1420", {"start": v(4.43, 1.24) * mm, "end": v(4.53, 1.24) * mm});
            skLineSegment(sketch, "E1421", {"start": v(4.53, 1.24) * mm, "end": v(4.64, 1.23) * mm});
            skLineSegment(sketch, "E1422", {"start": v(4.64, 1.23) * mm, "end": v(4.74, 1.23) * mm});
            skLineSegment(sketch, "E1423", {"start": v(4.74, 1.23) * mm, "end": v(4.84, 1.22) * mm});
            skLineSegment(sketch, "E1424", {"start": v(4.84, 1.22) * mm, "end": v(4.95, 1.2) * mm});
            skLineSegment(sketch, "E1425", {"start": v(4.95, 1.2) * mm, "end": v(5.05, 1.2) * mm});
            skLineSegment(sketch, "E1426", {"start": v(5.05, 1.2) * mm, "end": v(5.15, 1.18) * mm});
            skLineSegment(sketch, "E1427", {"start": v(5.15, 1.18) * mm, "end": v(5.26, 1.16) * mm});
            skLineSegment(sketch, "E1428", {"start": v(5.26, 1.16) * mm, "end": v(5.36, 1.14) * mm});
            skLineSegment(sketch, "E1429", {"start": v(5.36, 1.14) * mm, "end": v(5.46, 1.12) * mm});
            skLineSegment(sketch, "E1430", {"start": v(5.46, 1.12) * mm, "end": v(5.57, 1.1) * mm});
            skLineSegment(sketch, "E1431", {"start": v(5.57, 1.1) * mm, "end": v(5.67, 1.08) * mm});
            skLineSegment(sketch, "E1432", {"start": v(5.67, 1.08) * mm, "end": v(5.77, 1.06) * mm});
            skLineSegment(sketch, "E1433", {"start": v(5.77, 1.06) * mm, "end": v(5.87, 1.03) * mm});
            skLineSegment(sketch, "E1434", {"start": v(5.87, 1.03) * mm, "end": v(5.98, 1) * mm});
            skLineSegment(sketch, "E1435", {"start": v(5.98, 1) * mm, "end": v(6.08, 0.97) * mm});
            skLineSegment(sketch, "E1436", {"start": v(6.08, 0.97) * mm, "end": v(6.18, 0.94) * mm});
            skLineSegment(sketch, "E1437", {"start": v(6.18, 0.94) * mm, "end": v(6.28, 0.9) * mm});
            skLineSegment(sketch, "E1438", {"start": v(6.28, 0.9) * mm, "end": v(6.39, 0.87) * mm});
            skLineSegment(sketch, "E1439", {"start": v(6.39, 0.87) * mm, "end": v(6.49, 0.84) * mm});
            skLineSegment(sketch, "E1440", {"start": v(6.49, 0.84) * mm, "end": v(6.6, 0.8) * mm});
            skLineSegment(sketch, "E1441", {"start": v(6.6, 0.8) * mm, "end": v(6.7, 0.76) * mm});
            skLineSegment(sketch, "E1442", {"start": v(6.7, 0.76) * mm, "end": v(6.8, 0.72) * mm});
            skLineSegment(sketch, "E1443", {"start": v(6.8, 0.72) * mm, "end": v(6.9, 0.68) * mm});
            skLineSegment(sketch, "E1444", {"start": v(6.9, 0.68) * mm, "end": v(7, 0.63) * mm});
            skLineSegment(sketch, "E1445", {"start": v(7, 0.63) * mm, "end": v(7.1, 0.58) * mm});
            skLineSegment(sketch, "E1446", {"start": v(7.1, 0.58) * mm, "end": v(7.2, 0.54) * mm});
            skLineSegment(sketch, "E1447", {"start": v(7.2, 0.54) * mm, "end": v(7.3, 0.49) * mm});
            skLineSegment(sketch, "E1448", {"start": v(7.3, 0.49) * mm, "end": v(7.36, 0.46) * mm});
            skLineSegment(sketch, "E1449", {"start": v(7.36, 0.46) * mm, "end": v(7.36, 0.51) * mm});
            skLineSegment(sketch, "E1450", {"start": v(-0.63, 3.42) * mm, "end": v(-0.6, 3.47) * mm});
            skLineSegment(sketch, "E1451", {"start": v(-0.6, 3.47) * mm, "end": v(-0.58, 3.53) * mm});
            skLineSegment(sketch, "E1452", {"start": v(-0.58, 3.53) * mm, "end": v(-0.56, 3.58) * mm});
            skLineSegment(sketch, "E1453", {"start": v(-0.56, 3.58) * mm, "end": v(-0.54, 3.63) * mm});
            skLineSegment(sketch, "E1454", {"start": v(-0.54, 3.63) * mm, "end": v(-0.52, 3.69) * mm});
            skLineSegment(sketch, "E1455", {"start": v(-0.52, 3.69) * mm, "end": v(-0.5, 3.74) * mm});
            skLineSegment(sketch, "E1456", {"start": v(-0.5, 3.74) * mm, "end": v(-0.48, 3.8) * mm});
            skLineSegment(sketch, "E1457", {"start": v(-0.48, 3.8) * mm, "end": v(-0.46, 3.85) * mm});
            skLineSegment(sketch, "E1458", {"start": v(-0.46, 3.85) * mm, "end": v(-0.44, 3.9) * mm});
            skLineSegment(sketch, "E1459", {"start": v(-0.44, 3.9) * mm, "end": v(-0.43, 3.95) * mm});
            skLineSegment(sketch, "E1460", {"start": v(-0.43, 3.95) * mm, "end": v(-0.41, 4) * mm});
            skLineSegment(sketch, "E1461", {"start": v(-0.41, 4) * mm, "end": v(-0.4, 4.06) * mm});
            skLineSegment(sketch, "E1462", {"start": v(-0.4, 4.06) * mm, "end": v(-0.38, 4.11) * mm});
            skLineSegment(sketch, "E1463", {"start": v(-0.38, 4.11) * mm, "end": v(-0.37, 4.17) * mm});
            skLineSegment(sketch, "E1464", {"start": v(-0.37, 4.17) * mm, "end": v(-0.36, 4.22) * mm});
            skLineSegment(sketch, "E1465", {"start": v(-0.36, 4.22) * mm, "end": v(-0.35, 4.28) * mm});
            skLineSegment(sketch, "E1466", {"start": v(-0.35, 4.28) * mm, "end": v(-0.33, 4.33) * mm});
            skLineSegment(sketch, "E1467", {"start": v(-0.33, 4.33) * mm, "end": v(-0.32, 4.38) * mm});
            skLineSegment(sketch, "E1468", {"start": v(-0.32, 4.38) * mm, "end": v(-0.32, 4.44) * mm});
            skLineSegment(sketch, "E1469", {"start": v(-0.32, 4.44) * mm, "end": v(-0.3, 4.5) * mm});
            skLineSegment(sketch, "E1470", {"start": v(-0.3, 4.5) * mm, "end": v(-0.3, 4.55) * mm});
            skLineSegment(sketch, "E1471", {"start": v(-0.3, 4.55) * mm, "end": v(-0.3, 4.6) * mm});
            skLineSegment(sketch, "E1472", {"start": v(-0.3, 4.6) * mm, "end": v(-0.29, 4.65) * mm});
            skLineSegment(sketch, "E1473", {"start": v(-0.29, 4.65) * mm, "end": v(-0.28, 4.7) * mm});
            skLineSegment(sketch, "E1474", {"start": v(-0.28, 4.7) * mm, "end": v(-0.28, 4.76) * mm});
            skLineSegment(sketch, "E1475", {"start": v(-0.28, 4.76) * mm, "end": v(-0.27, 4.82) * mm});
            skLineSegment(sketch, "E1476", {"start": v(-0.27, 4.82) * mm, "end": v(-0.27, 4.87) * mm});
            skLineSegment(sketch, "E1477", {"start": v(-0.27, 4.87) * mm, "end": v(-0.27, 4.93) * mm});
            skLineSegment(sketch, "E1478", {"start": v(-0.27, 4.93) * mm, "end": v(-0.27, 4.98) * mm});
            skLineSegment(sketch, "E1479", {"start": v(-0.27, 4.98) * mm, "end": v(-0.27, 5.03) * mm});
            skLineSegment(sketch, "E1480", {"start": v(-0.27, 5.03) * mm, "end": v(-0.27, 5.09) * mm});
            skLineSegment(sketch, "E1481", {"start": v(-0.27, 5.09) * mm, "end": v(-0.27, 5.14) * mm});
            skLineSegment(sketch, "E1482", {"start": v(-0.27, 5.14) * mm, "end": v(-0.27, 5.2) * mm});
            skLineSegment(sketch, "E1483", {"start": v(-0.27, 5.2) * mm, "end": v(-0.27, 5.25) * mm});
            skLineSegment(sketch, "E1484", {"start": v(-0.27, 5.25) * mm, "end": v(-0.28, 5.3) * mm});
            skLineSegment(sketch, "E1485", {"start": v(-0.28, 5.3) * mm, "end": v(-0.28, 5.36) * mm});
            skLineSegment(sketch, "E1486", {"start": v(-0.28, 5.36) * mm, "end": v(-0.29, 5.42) * mm});
            skLineSegment(sketch, "E1487", {"start": v(-0.29, 5.42) * mm, "end": v(-0.3, 5.47) * mm});
            skLineSegment(sketch, "E1488", {"start": v(-0.3, 5.47) * mm, "end": v(-0.3, 5.53) * mm});
            skLineSegment(sketch, "E1489", {"start": v(-0.3, 5.53) * mm, "end": v(-0.3, 5.58) * mm});
            skLineSegment(sketch, "E1490", {"start": v(-0.3, 5.58) * mm, "end": v(-0.32, 5.64) * mm});
            skLineSegment(sketch, "E1491", {"start": v(-0.32, 5.64) * mm, "end": v(-0.33, 5.7) * mm});
            skLineSegment(sketch, "E1492", {"start": v(-0.33, 5.7) * mm, "end": v(-0.34, 5.75) * mm});
            skLineSegment(sketch, "E1493", {"start": v(-0.34, 5.75) * mm, "end": v(-0.35, 5.8) * mm});
            skLineSegment(sketch, "E1494", {"start": v(-0.35, 5.8) * mm, "end": v(-0.36, 5.86) * mm});
            skLineSegment(sketch, "E1495", {"start": v(-0.36, 5.86) * mm, "end": v(-0.37, 5.91) * mm});
            skLineSegment(sketch, "E1496", {"start": v(-0.37, 5.91) * mm, "end": v(-0.39, 5.97) * mm});
            skLineSegment(sketch, "E1497", {"start": v(-0.39, 5.97) * mm, "end": v(-0.4, 6.02) * mm});
            skLineSegment(sketch, "E1498", {"start": v(-0.4, 6.02) * mm, "end": v(-0.42, 6.08) * mm});
            skLineSegment(sketch, "E1499", {"start": v(-0.42, 6.08) * mm, "end": v(-0.43, 6.13) * mm});
            skLineSegment(sketch, "E1500", {"start": v(-0.43, 6.13) * mm, "end": v(-0.45, 6.18) * mm});
            skLineSegment(sketch, "E1501", {"start": v(-0.45, 6.18) * mm, "end": v(-0.47, 6.24) * mm});
            skLineSegment(sketch, "E1502", {"start": v(-0.47, 6.24) * mm, "end": v(-0.49, 6.3) * mm});
            skLineSegment(sketch, "E1503", {"start": v(-0.49, 6.3) * mm, "end": v(-0.5, 6.35) * mm});
            skLineSegment(sketch, "E1504", {"start": v(-0.5, 6.35) * mm, "end": v(-0.53, 6.4) * mm});
            skLineSegment(sketch, "E1505", {"start": v(-0.53, 6.4) * mm, "end": v(-0.55, 6.46) * mm});
            skLineSegment(sketch, "E1506", {"start": v(-0.55, 6.46) * mm, "end": v(-0.57, 6.51) * mm});
            skLineSegment(sketch, "E1507", {"start": v(-0.57, 6.51) * mm, "end": v(-0.6, 6.57) * mm});
            skLineSegment(sketch, "E1508", {"start": v(-0.6, 6.57) * mm, "end": v(-0.62, 6.62) * mm});
            skLineSegment(sketch, "E1509", {"start": v(-0.62, 6.62) * mm, "end": v(-0.64, 6.67) * mm});
            skLineSegment(sketch, "E1510", {"start": v(-0.64, 6.67) * mm, "end": v(-0.64, 6.68) * mm});
            skLineSegment(sketch, "E1511", {"start": v(-0.64, 6.68) * mm, "end": v(-0.9, 6.68) * mm});
            skLineSegment(sketch, "E1512", {"start": v(-0.9, 6.68) * mm, "end": v(-0.92, 6.66) * mm});
            skLineSegment(sketch, "E1513", {"start": v(-0.92, 6.66) * mm, "end": v(-0.94, 6.61) * mm});
            skLineSegment(sketch, "E1514", {"start": v(-0.94, 6.61) * mm, "end": v(-0.97, 6.56) * mm});
            skLineSegment(sketch, "E1515", {"start": v(-0.97, 6.56) * mm, "end": v(-1, 6.5) * mm});
            skLineSegment(sketch, "E1516", {"start": v(-1, 6.5) * mm, "end": v(-1.02, 6.45) * mm});
            skLineSegment(sketch, "E1517", {"start": v(-1.02, 6.45) * mm, "end": v(-1.05, 6.4) * mm});
            skLineSegment(sketch, "E1518", {"start": v(-1.05, 6.4) * mm, "end": v(-1.07, 6.34) * mm});
            skLineSegment(sketch, "E1519", {"start": v(-1.07, 6.34) * mm, "end": v(-1.1, 6.29) * mm});
            skLineSegment(sketch, "E1520", {"start": v(-1.1, 6.29) * mm, "end": v(-1.12, 6.23) * mm});
            skLineSegment(sketch, "E1521", {"start": v(-1.12, 6.23) * mm, "end": v(-1.14, 6.18) * mm});
            skLineSegment(sketch, "E1522", {"start": v(-1.14, 6.18) * mm, "end": v(-1.16, 6.12) * mm});
            skLineSegment(sketch, "E1523", {"start": v(-1.16, 6.12) * mm, "end": v(-1.17, 6.07) * mm});
            skLineSegment(sketch, "E1524", {"start": v(-1.17, 6.07) * mm, "end": v(-1.2, 6.02) * mm});
            skLineSegment(sketch, "E1525", {"start": v(-1.2, 6.02) * mm, "end": v(-1.2, 5.96) * mm});
            skLineSegment(sketch, "E1526", {"start": v(-1.2, 5.96) * mm, "end": v(-1.22, 5.9) * mm});
            skLineSegment(sketch, "E1527", {"start": v(-1.22, 5.9) * mm, "end": v(-1.24, 5.85) * mm});
            skLineSegment(sketch, "E1528", {"start": v(-1.24, 5.85) * mm, "end": v(-1.25, 5.8) * mm});
            skLineSegment(sketch, "E1529", {"start": v(-1.25, 5.8) * mm, "end": v(-1.27, 5.74) * mm});
            skLineSegment(sketch, "E1530", {"start": v(-1.27, 5.74) * mm, "end": v(-1.28, 5.69) * mm});
            skLineSegment(sketch, "E1531", {"start": v(-1.28, 5.69) * mm, "end": v(-1.3, 5.63) * mm});
            skLineSegment(sketch, "E1532", {"start": v(-1.3, 5.63) * mm, "end": v(-1.3, 5.58) * mm});
            skLineSegment(sketch, "E1533", {"start": v(-1.3, 5.58) * mm, "end": v(-1.3, 5.53) * mm});
            skLineSegment(sketch, "E1534", {"start": v(-1.3, 5.53) * mm, "end": v(-1.32, 5.47) * mm});
            skLineSegment(sketch, "E1535", {"start": v(-1.32, 5.47) * mm, "end": v(-1.32, 5.42) * mm});
            skLineSegment(sketch, "E1536", {"start": v(-1.32, 5.42) * mm, "end": v(-1.33, 5.36) * mm});
            skLineSegment(sketch, "E1537", {"start": v(-1.33, 5.36) * mm, "end": v(-1.34, 5.3) * mm});
            skLineSegment(sketch, "E1538", {"start": v(-1.34, 5.3) * mm, "end": v(-1.34, 5.25) * mm});
            skLineSegment(sketch, "E1539", {"start": v(-1.34, 5.25) * mm, "end": v(-1.34, 5.2) * mm});
            skLineSegment(sketch, "E1540", {"start": v(-1.34, 5.2) * mm, "end": v(-1.35, 5.14) * mm});
            skLineSegment(sketch, "E1541", {"start": v(-1.35, 5.14) * mm, "end": v(-1.35, 5.09) * mm});
            skLineSegment(sketch, "E1542", {"start": v(-1.35, 5.09) * mm, "end": v(-1.35, 5.03) * mm});
            skLineSegment(sketch, "E1543", {"start": v(-1.35, 5.03) * mm, "end": v(-1.35, 4.98) * mm});
            skLineSegment(sketch, "E1544", {"start": v(-1.35, 4.98) * mm, "end": v(-1.35, 4.93) * mm});
            skLineSegment(sketch, "E1545", {"start": v(-1.35, 4.93) * mm, "end": v(-1.34, 4.87) * mm});
            skLineSegment(sketch, "E1546", {"start": v(-1.34, 4.87) * mm, "end": v(-1.34, 4.82) * mm});
            skLineSegment(sketch, "E1547", {"start": v(-1.34, 4.82) * mm, "end": v(-1.34, 4.76) * mm});
            skLineSegment(sketch, "E1548", {"start": v(-1.34, 4.76) * mm, "end": v(-1.33, 4.71) * mm});
            skLineSegment(sketch, "E1549", {"start": v(-1.33, 4.71) * mm, "end": v(-1.33, 4.66) * mm});
            skLineSegment(sketch, "E1550", {"start": v(-1.33, 4.66) * mm, "end": v(-1.32, 4.6) * mm});
            skLineSegment(sketch, "E1551", {"start": v(-1.32, 4.6) * mm, "end": v(-1.31, 4.55) * mm});
            skLineSegment(sketch, "E1552", {"start": v(-1.31, 4.55) * mm, "end": v(-1.3, 4.5) * mm});
            skLineSegment(sketch, "E1553", {"start": v(-1.3, 4.5) * mm, "end": v(-1.3, 4.44) * mm});
            skLineSegment(sketch, "E1554", {"start": v(-1.3, 4.44) * mm, "end": v(-1.28, 4.39) * mm});
            skLineSegment(sketch, "E1555", {"start": v(-1.28, 4.39) * mm, "end": v(-1.27, 4.33) * mm});
            skLineSegment(sketch, "E1556", {"start": v(-1.27, 4.33) * mm, "end": v(-1.26, 4.28) * mm});
            skLineSegment(sketch, "E1557", {"start": v(-1.26, 4.28) * mm, "end": v(-1.24, 4.23) * mm});
            skLineSegment(sketch, "E1558", {"start": v(-1.24, 4.23) * mm, "end": v(-1.23, 4.17) * mm});
            skLineSegment(sketch, "E1559", {"start": v(-1.23, 4.17) * mm, "end": v(-1.21, 4.12) * mm});
            skLineSegment(sketch, "E1560", {"start": v(-1.21, 4.12) * mm, "end": v(-1.2, 4.07) * mm});
            skLineSegment(sketch, "E1561", {"start": v(-1.2, 4.07) * mm, "end": v(-1.18, 4.01) * mm});
            skLineSegment(sketch, "E1562", {"start": v(-1.18, 4.01) * mm, "end": v(-1.16, 3.96) * mm});
            skLineSegment(sketch, "E1563", {"start": v(-1.16, 3.96) * mm, "end": v(-1.14, 3.9) * mm});
            skLineSegment(sketch, "E1564", {"start": v(-1.14, 3.9) * mm, "end": v(-1.12, 3.85) * mm});
            skLineSegment(sketch, "E1565", {"start": v(-1.12, 3.85) * mm, "end": v(-1.1, 3.8) * mm});
            skLineSegment(sketch, "E1566", {"start": v(-1.1, 3.8) * mm, "end": v(-1.08, 3.75) * mm});
            skLineSegment(sketch, "E1567", {"start": v(-1.08, 3.75) * mm, "end": v(-1.06, 3.7) * mm});
            skLineSegment(sketch, "E1568", {"start": v(-1.06, 3.7) * mm, "end": v(-1.03, 3.64) * mm});
            skLineSegment(sketch, "E1569", {"start": v(-1.03, 3.64) * mm, "end": v(-1, 3.59) * mm});
            skLineSegment(sketch, "E1570", {"start": v(-1, 3.59) * mm, "end": v(-0.98, 3.53) * mm});
            skLineSegment(sketch, "E1571", {"start": v(-0.98, 3.53) * mm, "end": v(-0.95, 3.48) * mm});
            skLineSegment(sketch, "E1572", {"start": v(-0.95, 3.48) * mm, "end": v(-0.93, 3.43) * mm});
            skLineSegment(sketch, "E1573", {"start": v(-0.93, 3.43) * mm, "end": v(-0.92, 3.41) * mm});
            skLineSegment(sketch, "E1574", {"start": v(-0.92, 3.41) * mm, "end": v(-0.63, 3.41) * mm});
            skLineSegment(sketch, "E1575", {"start": v(-0.63, 3.41) * mm, "end": v(-0.63, 3.42) * mm});
            skLineSegment(sketch, "E1576", {"start": v(4.3, -0.53) * mm, "end": v(4.35, -0.53) * mm});
            skLineSegment(sketch, "E1577", {"start": v(4.35, -0.53) * mm, "end": v(4.4, -0.53) * mm});
            skLineSegment(sketch, "E1578", {"start": v(4.4, -0.53) * mm, "end": v(4.46, -0.52) * mm});
            skLineSegment(sketch, "E1579", {"start": v(4.46, -0.52) * mm, "end": v(4.51, -0.52) * mm});
            skLineSegment(sketch, "E1580", {"start": v(4.51, -0.52) * mm, "end": v(4.57, -0.51) * mm});
            skLineSegment(sketch, "E1581", {"start": v(4.57, -0.51) * mm, "end": v(4.62, -0.5) * mm});
            skLineSegment(sketch, "E1582", {"start": v(4.62, -0.5) * mm, "end": v(4.68, -0.5) * mm});
            skLineSegment(sketch, "E1583", {"start": v(4.68, -0.5) * mm, "end": v(4.73, -0.5) * mm});
            skLineSegment(sketch, "E1584", {"start": v(4.73, -0.5) * mm, "end": v(4.79, -0.49) * mm});
            skLineSegment(sketch, "E1585", {"start": v(4.79, -0.49) * mm, "end": v(4.84, -0.48) * mm});
            skLineSegment(sketch, "E1586", {"start": v(4.84, -0.48) * mm, "end": v(4.9, -0.47) * mm});
            skLineSegment(sketch, "E1587", {"start": v(4.9, -0.47) * mm, "end": v(4.95, -0.46) * mm});
            skLineSegment(sketch, "E1588", {"start": v(4.95, -0.46) * mm, "end": v(5, -0.45) * mm});
            skLineSegment(sketch, "E1589", {"start": v(5, -0.45) * mm, "end": v(5.06, -0.44) * mm});
            skLineSegment(sketch, "E1590", {"start": v(5.06, -0.44) * mm, "end": v(5.12, -0.42) * mm});
            skLineSegment(sketch, "E1591", {"start": v(5.12, -0.42) * mm, "end": v(5.17, -0.4) * mm});
            skLineSegment(sketch, "E1592", {"start": v(5.17, -0.4) * mm, "end": v(5.23, -0.4) * mm});
            skLineSegment(sketch, "E1593", {"start": v(5.23, -0.4) * mm, "end": v(5.28, -0.38) * mm});
            skLineSegment(sketch, "E1594", {"start": v(5.28, -0.38) * mm, "end": v(5.33, -0.36) * mm});
            skLineSegment(sketch, "E1595", {"start": v(5.33, -0.36) * mm, "end": v(5.39, -0.35) * mm});
            skLineSegment(sketch, "E1596", {"start": v(5.39, -0.35) * mm, "end": v(5.44, -0.33) * mm});
            skLineSegment(sketch, "E1597", {"start": v(5.44, -0.33) * mm, "end": v(5.5, -0.3) * mm});
            skLineSegment(sketch, "E1598", {"start": v(5.5, -0.3) * mm, "end": v(5.55, -0.29) * mm});
            skLineSegment(sketch, "E1599", {"start": v(5.55, -0.29) * mm, "end": v(5.6, -0.27) * mm});
            skLineSegment(sketch, "E1600", {"start": v(5.6, -0.27) * mm, "end": v(5.66, -0.25) * mm});
            skLineSegment(sketch, "E1601", {"start": v(5.66, -0.25) * mm, "end": v(5.72, -0.23) * mm});
            skLineSegment(sketch, "E1602", {"start": v(5.72, -0.23) * mm, "end": v(5.77, -0.2) * mm});
            skLineSegment(sketch, "E1603", {"start": v(5.77, -0.2) * mm, "end": v(5.82, -0.18) * mm});
            skLineSegment(sketch, "E1604", {"start": v(5.82, -0.18) * mm, "end": v(5.88, -0.16) * mm});
            skLineSegment(sketch, "E1605", {"start": v(5.88, -0.16) * mm, "end": v(5.88, -0.15) * mm});
            skLineSegment(sketch, "E1606", {"start": v(5.88, -0.15) * mm, "end": v(5.88, 0.11) * mm});
            skLineSegment(sketch, "E1607", {"start": v(5.88, 0.11) * mm, "end": v(5.87, 0.12) * mm});
            skLineSegment(sketch, "E1608", {"start": v(5.87, 0.12) * mm, "end": v(5.81, 0.15) * mm});
            skLineSegment(sketch, "E1609", {"start": v(5.81, 0.15) * mm, "end": v(5.76, 0.17) * mm});
            skLineSegment(sketch, "E1610", {"start": v(5.76, 0.17) * mm, "end": v(5.7, 0.2) * mm});
            skLineSegment(sketch, "E1611", {"start": v(5.7, 0.2) * mm, "end": v(5.65, 0.23) * mm});
            skLineSegment(sketch, "E1612", {"start": v(5.65, 0.23) * mm, "end": v(5.6, 0.25) * mm});
            skLineSegment(sketch, "E1613", {"start": v(5.6, 0.25) * mm, "end": v(5.54, 0.27) * mm});
            skLineSegment(sketch, "E1614", {"start": v(5.54, 0.27) * mm, "end": v(5.5, 0.3) * mm});
            skLineSegment(sketch, "E1615", {"start": v(5.5, 0.3) * mm, "end": v(5.44, 0.32) * mm});
            skLineSegment(sketch, "E1616", {"start": v(5.44, 0.32) * mm, "end": v(5.38, 0.34) * mm});
            skLineSegment(sketch, "E1617", {"start": v(5.38, 0.34) * mm, "end": v(5.33, 0.36) * mm});
            skLineSegment(sketch, "E1618", {"start": v(5.33, 0.36) * mm, "end": v(5.27, 0.38) * mm});
            skLineSegment(sketch, "E1619", {"start": v(5.27, 0.38) * mm, "end": v(5.22, 0.4) * mm});
            skLineSegment(sketch, "E1620", {"start": v(5.22, 0.4) * mm, "end": v(5.17, 0.41) * mm});
            skLineSegment(sketch, "E1621", {"start": v(5.17, 0.41) * mm, "end": v(5.11, 0.43) * mm});
            skLineSegment(sketch, "E1622", {"start": v(5.11, 0.43) * mm, "end": v(5.06, 0.44) * mm});
            skLineSegment(sketch, "E1623", {"start": v(5.06, 0.44) * mm, "end": v(5, 0.46) * mm});
            skLineSegment(sketch, "E1624", {"start": v(5, 0.46) * mm, "end": v(4.95, 0.47) * mm});
            skLineSegment(sketch, "E1625", {"start": v(4.95, 0.47) * mm, "end": v(4.9, 0.48) * mm});
            skLineSegment(sketch, "E1626", {"start": v(4.9, 0.48) * mm, "end": v(4.84, 0.5) * mm});
            skLineSegment(sketch, "E1627", {"start": v(4.84, 0.5) * mm, "end": v(4.78, 0.5) * mm});
            skLineSegment(sketch, "E1628", {"start": v(4.78, 0.5) * mm, "end": v(4.73, 0.51) * mm});
            skLineSegment(sketch, "E1629", {"start": v(4.73, 0.51) * mm, "end": v(4.68, 0.52) * mm});
            skLineSegment(sketch, "E1630", {"start": v(4.68, 0.52) * mm, "end": v(4.62, 0.53) * mm});
            skLineSegment(sketch, "E1631", {"start": v(4.62, 0.53) * mm, "end": v(4.57, 0.54) * mm});
            skLineSegment(sketch, "E1632", {"start": v(4.57, 0.54) * mm, "end": v(4.51, 0.54) * mm});
            skLineSegment(sketch, "E1633", {"start": v(4.51, 0.54) * mm, "end": v(4.46, 0.54) * mm});
            skLineSegment(sketch, "E1634", {"start": v(4.46, 0.54) * mm, "end": v(4.4, 0.55) * mm});
            skLineSegment(sketch, "E1635", {"start": v(4.4, 0.55) * mm, "end": v(4.35, 0.55) * mm});
            skLineSegment(sketch, "E1636", {"start": v(4.35, 0.55) * mm, "end": v(4.3, 0.55) * mm});
            skLineSegment(sketch, "E1637", {"start": v(4.3, 0.55) * mm, "end": v(4.24, 0.55) * mm});
            skLineSegment(sketch, "E1638", {"start": v(4.24, 0.55) * mm, "end": v(4.18, 0.55) * mm});
            skLineSegment(sketch, "E1639", {"start": v(4.18, 0.55) * mm, "end": v(4.13, 0.55) * mm});
            skLineSegment(sketch, "E1640", {"start": v(4.13, 0.55) * mm, "end": v(4.08, 0.55) * mm});
            skLineSegment(sketch, "E1641", {"start": v(4.08, 0.55) * mm, "end": v(4.02, 0.55) * mm});
            skLineSegment(sketch, "E1642", {"start": v(4.02, 0.55) * mm, "end": v(3.97, 0.54) * mm});
            skLineSegment(sketch, "E1643", {"start": v(3.97, 0.54) * mm, "end": v(3.92, 0.54) * mm});
            skLineSegment(sketch, "E1644", {"start": v(3.92, 0.54) * mm, "end": v(3.86, 0.53) * mm});
            skLineSegment(sketch, "E1645", {"start": v(3.86, 0.53) * mm, "end": v(3.8, 0.52) * mm});
            skLineSegment(sketch, "E1646", {"start": v(3.8, 0.52) * mm, "end": v(3.75, 0.51) * mm});
            skLineSegment(sketch, "E1647", {"start": v(3.75, 0.51) * mm, "end": v(3.7, 0.5) * mm});
            skLineSegment(sketch, "E1648", {"start": v(3.7, 0.5) * mm, "end": v(3.65, 0.5) * mm});
            skLineSegment(sketch, "E1649", {"start": v(3.65, 0.5) * mm, "end": v(3.6, 0.48) * mm});
            skLineSegment(sketch, "E1650", {"start": v(3.6, 0.48) * mm, "end": v(3.54, 0.47) * mm});
            skLineSegment(sketch, "E1651", {"start": v(3.54, 0.47) * mm, "end": v(3.49, 0.46) * mm});
            skLineSegment(sketch, "E1652", {"start": v(3.49, 0.46) * mm, "end": v(3.43, 0.45) * mm});
            skLineSegment(sketch, "E1653", {"start": v(3.43, 0.45) * mm, "end": v(3.38, 0.43) * mm});
            skLineSegment(sketch, "E1654", {"start": v(3.38, 0.43) * mm, "end": v(3.33, 0.42) * mm});
            skLineSegment(sketch, "E1655", {"start": v(3.33, 0.42) * mm, "end": v(3.27, 0.4) * mm});
            skLineSegment(sketch, "E1656", {"start": v(3.27, 0.4) * mm, "end": v(3.22, 0.38) * mm});
            skLineSegment(sketch, "E1657", {"start": v(3.22, 0.38) * mm, "end": v(3.16, 0.37) * mm});
            skLineSegment(sketch, "E1658", {"start": v(3.16, 0.37) * mm, "end": v(3.11, 0.35) * mm});
            skLineSegment(sketch, "E1659", {"start": v(3.11, 0.35) * mm, "end": v(3.06, 0.33) * mm});
            skLineSegment(sketch, "E1660", {"start": v(3.06, 0.33) * mm, "end": v(3, 0.3) * mm});
            skLineSegment(sketch, "E1661", {"start": v(3, 0.3) * mm, "end": v(2.95, 0.28) * mm});
            skLineSegment(sketch, "E1662", {"start": v(2.95, 0.28) * mm, "end": v(2.9, 0.26) * mm});
            skLineSegment(sketch, "E1663", {"start": v(2.9, 0.26) * mm, "end": v(2.84, 0.24) * mm});
            skLineSegment(sketch, "E1664", {"start": v(2.84, 0.24) * mm, "end": v(2.8, 0.21) * mm});
            skLineSegment(sketch, "E1665", {"start": v(2.8, 0.21) * mm, "end": v(2.74, 0.19) * mm});
            skLineSegment(sketch, "E1666", {"start": v(2.74, 0.19) * mm, "end": v(2.68, 0.16) * mm});
            skLineSegment(sketch, "E1667", {"start": v(2.68, 0.16) * mm, "end": v(2.63, 0.13) * mm});
            skLineSegment(sketch, "E1668", {"start": v(2.63, 0.13) * mm, "end": v(2.62, 0.12) * mm});
            skLineSegment(sketch, "E1669", {"start": v(2.62, 0.12) * mm, "end": v(2.62, -0.16) * mm});
            skLineSegment(sketch, "E1670", {"start": v(2.62, -0.16) * mm, "end": v(2.62, -0.17) * mm});
            skLineSegment(sketch, "E1671", {"start": v(2.62, -0.17) * mm, "end": v(2.68, -0.19) * mm});
            skLineSegment(sketch, "E1672", {"start": v(2.68, -0.19) * mm, "end": v(2.73, -0.21) * mm});
            skLineSegment(sketch, "E1673", {"start": v(2.73, -0.21) * mm, "end": v(2.78, -0.23) * mm});
            skLineSegment(sketch, "E1674", {"start": v(2.78, -0.23) * mm, "end": v(2.84, -0.26) * mm});
            skLineSegment(sketch, "E1675", {"start": v(2.84, -0.26) * mm, "end": v(2.89, -0.28) * mm});
            skLineSegment(sketch, "E1676", {"start": v(2.89, -0.28) * mm, "end": v(2.94, -0.3) * mm});
            skLineSegment(sketch, "E1677", {"start": v(2.94, -0.3) * mm, "end": v(3, -0.32) * mm});
            skLineSegment(sketch, "E1678", {"start": v(3, -0.32) * mm, "end": v(3.05, -0.33) * mm});
            skLineSegment(sketch, "E1679", {"start": v(3.05, -0.33) * mm, "end": v(3.1, -0.35) * mm});
            skLineSegment(sketch, "E1680", {"start": v(3.1, -0.35) * mm, "end": v(3.16, -0.37) * mm});
            skLineSegment(sketch, "E1681", {"start": v(3.16, -0.37) * mm, "end": v(3.21, -0.38) * mm});
            skLineSegment(sketch, "E1682", {"start": v(3.21, -0.38) * mm, "end": v(3.27, -0.4) * mm});
            skLineSegment(sketch, "E1683", {"start": v(3.27, -0.4) * mm, "end": v(3.32, -0.41) * mm});
            skLineSegment(sketch, "E1684", {"start": v(3.32, -0.41) * mm, "end": v(3.37, -0.43) * mm});
            skLineSegment(sketch, "E1685", {"start": v(3.37, -0.43) * mm, "end": v(3.43, -0.44) * mm});
            skLineSegment(sketch, "E1686", {"start": v(3.43, -0.44) * mm, "end": v(3.48, -0.45) * mm});
            skLineSegment(sketch, "E1687", {"start": v(3.48, -0.45) * mm, "end": v(3.53, -0.46) * mm});
            skLineSegment(sketch, "E1688", {"start": v(3.53, -0.46) * mm, "end": v(3.59, -0.47) * mm});
            skLineSegment(sketch, "E1689", {"start": v(3.59, -0.47) * mm, "end": v(3.64, -0.48) * mm});
            skLineSegment(sketch, "E1690", {"start": v(3.64, -0.48) * mm, "end": v(3.7, -0.49) * mm});
            skLineSegment(sketch, "E1691", {"start": v(3.7, -0.49) * mm, "end": v(3.75, -0.5) * mm});
            skLineSegment(sketch, "E1692", {"start": v(3.75, -0.5) * mm, "end": v(3.8, -0.5) * mm});
            skLineSegment(sketch, "E1693", {"start": v(3.8, -0.5) * mm, "end": v(3.86, -0.5) * mm});
            skLineSegment(sketch, "E1694", {"start": v(3.86, -0.5) * mm, "end": v(3.91, -0.52) * mm});
            skLineSegment(sketch, "E1695", {"start": v(3.91, -0.52) * mm, "end": v(3.97, -0.52) * mm});
            skLineSegment(sketch, "E1696", {"start": v(3.97, -0.52) * mm, "end": v(4.02, -0.52) * mm});
            skLineSegment(sketch, "E1697", {"start": v(4.02, -0.52) * mm, "end": v(4.08, -0.53) * mm});
            skLineSegment(sketch, "E1698", {"start": v(4.08, -0.53) * mm, "end": v(4.13, -0.53) * mm});
            skLineSegment(sketch, "E1699", {"start": v(4.13, -0.53) * mm, "end": v(4.18, -0.53) * mm});
            skLineSegment(sketch, "E1700", {"start": v(4.18, -0.53) * mm, "end": v(4.24, -0.53) * mm});
            skLineSegment(sketch, "E1701", {"start": v(4.24, -0.53) * mm, "end": v(4.3, -0.53) * mm});
            skLineSegment(sketch, "E1702", {"start": v(-5.78, -0.55) * mm, "end": v(-5.72, -0.55) * mm});
            skLineSegment(sketch, "E1703", {"start": v(-5.72, -0.55) * mm, "end": v(-5.67, -0.55) * mm});
            skLineSegment(sketch, "E1704", {"start": v(-5.67, -0.55) * mm, "end": v(-5.61, -0.55) * mm});
            skLineSegment(sketch, "E1705", {"start": v(-5.61, -0.55) * mm, "end": v(-5.56, -0.54) * mm});
            skLineSegment(sketch, "E1706", {"start": v(-5.56, -0.54) * mm, "end": v(-5.5, -0.54) * mm});
            skLineSegment(sketch, "E1707", {"start": v(-5.5, -0.54) * mm, "end": v(-5.45, -0.53) * mm});
            skLineSegment(sketch, "E1708", {"start": v(-5.45, -0.53) * mm, "end": v(-5.4, -0.52) * mm});
            skLineSegment(sketch, "E1709", {"start": v(-5.4, -0.52) * mm, "end": v(-5.35, -0.51) * mm});
            skLineSegment(sketch, "E1710", {"start": v(-5.35, -0.51) * mm, "end": v(-5.3, -0.5) * mm});
            skLineSegment(sketch, "E1711", {"start": v(-5.3, -0.5) * mm, "end": v(-5.24, -0.5) * mm});
            skLineSegment(sketch, "E1712", {"start": v(-5.24, -0.5) * mm, "end": v(-5.18, -0.49) * mm});
            skLineSegment(sketch, "E1713", {"start": v(-5.18, -0.49) * mm, "end": v(-5.13, -0.47) * mm});
            skLineSegment(sketch, "E1714", {"start": v(-5.13, -0.47) * mm, "end": v(-5.08, -0.46) * mm});
            skLineSegment(sketch, "E1715", {"start": v(-5.08, -0.46) * mm, "end": v(-5.02, -0.45) * mm});
            skLineSegment(sketch, "E1716", {"start": v(-5.02, -0.45) * mm, "end": v(-4.97, -0.43) * mm});
            skLineSegment(sketch, "E1717", {"start": v(-4.97, -0.43) * mm, "end": v(-4.92, -0.42) * mm});
            skLineSegment(sketch, "E1718", {"start": v(-4.92, -0.42) * mm, "end": v(-4.86, -0.4) * mm});
            skLineSegment(sketch, "E1719", {"start": v(-4.86, -0.4) * mm, "end": v(-4.8, -0.38) * mm});
            skLineSegment(sketch, "E1720", {"start": v(-4.8, -0.38) * mm, "end": v(-4.76, -0.37) * mm});
            skLineSegment(sketch, "E1721", {"start": v(-4.76, -0.37) * mm, "end": v(-4.7, -0.35) * mm});
            skLineSegment(sketch, "E1722", {"start": v(-4.7, -0.35) * mm, "end": v(-4.65, -0.33) * mm});
            skLineSegment(sketch, "E1723", {"start": v(-4.65, -0.33) * mm, "end": v(-4.6, -0.3) * mm});
            skLineSegment(sketch, "E1724", {"start": v(-4.6, -0.3) * mm, "end": v(-4.54, -0.28) * mm});
            skLineSegment(sketch, "E1725", {"start": v(-4.54, -0.28) * mm, "end": v(-4.49, -0.26) * mm});
            skLineSegment(sketch, "E1726", {"start": v(-4.49, -0.26) * mm, "end": v(-4.44, -0.24) * mm});
            skLineSegment(sketch, "E1727", {"start": v(-4.44, -0.24) * mm, "end": v(-4.38, -0.21) * mm});
            skLineSegment(sketch, "E1728", {"start": v(-4.38, -0.21) * mm, "end": v(-4.33, -0.19) * mm});
            skLineSegment(sketch, "E1729", {"start": v(-4.33, -0.19) * mm, "end": v(-4.28, -0.16) * mm});
            skLineSegment(sketch, "E1730", {"start": v(-4.28, -0.16) * mm, "end": v(-4.22, -0.13) * mm});
            skLineSegment(sketch, "E1731", {"start": v(-4.22, -0.13) * mm, "end": v(-4.2, -0.12) * mm});
            skLineSegment(sketch, "E1732", {"start": v(-4.2, -0.12) * mm, "end": v(-4.2, 0.16) * mm});
            skLineSegment(sketch, "E1733", {"start": v(-4.2, 0.16) * mm, "end": v(-4.21, 0.17) * mm});
            skLineSegment(sketch, "E1734", {"start": v(-4.21, 0.17) * mm, "end": v(-4.27, 0.19) * mm});
            skLineSegment(sketch, "E1735", {"start": v(-4.27, 0.19) * mm, "end": v(-4.32, 0.21) * mm});
            skLineSegment(sketch, "E1736", {"start": v(-4.32, 0.21) * mm, "end": v(-4.37, 0.23) * mm});
            skLineSegment(sketch, "E1737", {"start": v(-4.37, 0.23) * mm, "end": v(-4.43, 0.26) * mm});
            skLineSegment(sketch, "E1738", {"start": v(-4.43, 0.26) * mm, "end": v(-4.48, 0.28) * mm});
            skLineSegment(sketch, "E1739", {"start": v(-4.48, 0.28) * mm, "end": v(-4.53, 0.3) * mm});
            skLineSegment(sketch, "E1740", {"start": v(-4.53, 0.3) * mm, "end": v(-4.59, 0.32) * mm});
            skLineSegment(sketch, "E1741", {"start": v(-4.59, 0.32) * mm, "end": v(-4.64, 0.33) * mm});
            skLineSegment(sketch, "E1742", {"start": v(-4.64, 0.33) * mm, "end": v(-4.7, 0.35) * mm});
            skLineSegment(sketch, "E1743", {"start": v(-4.7, 0.35) * mm, "end": v(-4.75, 0.37) * mm});
            skLineSegment(sketch, "E1744", {"start": v(-4.75, 0.37) * mm, "end": v(-4.8, 0.38) * mm});
            skLineSegment(sketch, "E1745", {"start": v(-4.8, 0.38) * mm, "end": v(-4.86, 0.4) * mm});
            skLineSegment(sketch, "E1746", {"start": v(-4.86, 0.4) * mm, "end": v(-4.91, 0.41) * mm});
            skLineSegment(sketch, "E1747", {"start": v(-4.91, 0.41) * mm, "end": v(-4.96, 0.43) * mm});
            skLineSegment(sketch, "E1748", {"start": v(-4.96, 0.43) * mm, "end": v(-5.02, 0.44) * mm});
            skLineSegment(sketch, "E1749", {"start": v(-5.02, 0.44) * mm, "end": v(-5.07, 0.45) * mm});
            skLineSegment(sketch, "E1750", {"start": v(-5.07, 0.45) * mm, "end": v(-5.13, 0.46) * mm});
            skLineSegment(sketch, "E1751", {"start": v(-5.13, 0.46) * mm, "end": v(-5.18, 0.47) * mm});
            skLineSegment(sketch, "E1752", {"start": v(-5.18, 0.47) * mm, "end": v(-5.23, 0.48) * mm});
            skLineSegment(sketch, "E1753", {"start": v(-5.23, 0.48) * mm, "end": v(-5.29, 0.49) * mm});
            skLineSegment(sketch, "E1754", {"start": v(-5.29, 0.49) * mm, "end": v(-5.34, 0.5) * mm});
            skLineSegment(sketch, "E1755", {"start": v(-5.34, 0.5) * mm, "end": v(-5.4, 0.5) * mm});
            skLineSegment(sketch, "E1756", {"start": v(-5.4, 0.5) * mm, "end": v(-5.45, 0.5) * mm});
            skLineSegment(sketch, "E1757", {"start": v(-5.45, 0.5) * mm, "end": v(-5.5, 0.51) * mm});
            skLineSegment(sketch, "E1758", {"start": v(-5.5, 0.51) * mm, "end": v(-5.56, 0.52) * mm});
            skLineSegment(sketch, "E1759", {"start": v(-5.56, 0.52) * mm, "end": v(-5.61, 0.52) * mm});
            skLineSegment(sketch, "E1760", {"start": v(-5.61, 0.52) * mm, "end": v(-5.67, 0.53) * mm});
            skLineSegment(sketch, "E1761", {"start": v(-5.67, 0.53) * mm, "end": v(-5.72, 0.53) * mm});
            skLineSegment(sketch, "E1762", {"start": v(-5.72, 0.53) * mm, "end": v(-5.78, 0.53) * mm});
            skLineSegment(sketch, "E1763", {"start": v(-5.78, 0.53) * mm, "end": v(-5.83, 0.53) * mm});
            skLineSegment(sketch, "E1764", {"start": v(-5.83, 0.53) * mm, "end": v(-5.89, 0.53) * mm});
            skLineSegment(sketch, "E1765", {"start": v(-5.89, 0.53) * mm, "end": v(-5.94, 0.53) * mm});
            skLineSegment(sketch, "E1766", {"start": v(-5.94, 0.53) * mm, "end": v(-6, 0.53) * mm});
            skLineSegment(sketch, "E1767", {"start": v(-6, 0.53) * mm, "end": v(-6.05, 0.52) * mm});
            skLineSegment(sketch, "E1768", {"start": v(-6.05, 0.52) * mm, "end": v(-6.1, 0.52) * mm});
            skLineSegment(sketch, "E1769", {"start": v(-6.1, 0.52) * mm, "end": v(-6.16, 0.51) * mm});
            skLineSegment(sketch, "E1770", {"start": v(-6.16, 0.51) * mm, "end": v(-6.22, 0.5) * mm});
            skLineSegment(sketch, "E1771", {"start": v(-6.22, 0.5) * mm, "end": v(-6.27, 0.5) * mm});
            skLineSegment(sketch, "E1772", {"start": v(-6.27, 0.5) * mm, "end": v(-6.33, 0.5) * mm});
            skLineSegment(sketch, "E1773", {"start": v(-6.33, 0.5) * mm, "end": v(-6.38, 0.49) * mm});
            skLineSegment(sketch, "E1774", {"start": v(-6.38, 0.49) * mm, "end": v(-6.44, 0.48) * mm});
            skLineSegment(sketch, "E1775", {"start": v(-6.44, 0.48) * mm, "end": v(-6.49, 0.47) * mm});
            skLineSegment(sketch, "E1776", {"start": v(-6.49, 0.47) * mm, "end": v(-6.54, 0.46) * mm});
            skLineSegment(sketch, "E1777", {"start": v(-6.54, 0.46) * mm, "end": v(-6.6, 0.45) * mm});
            skLineSegment(sketch, "E1778", {"start": v(-6.6, 0.45) * mm, "end": v(-6.65, 0.44) * mm});
            skLineSegment(sketch, "E1779", {"start": v(-6.65, 0.44) * mm, "end": v(-6.7, 0.42) * mm});
            skLineSegment(sketch, "E1780", {"start": v(-6.7, 0.42) * mm, "end": v(-6.76, 0.4) * mm});
            skLineSegment(sketch, "E1781", {"start": v(-6.76, 0.4) * mm, "end": v(-6.82, 0.4) * mm});
            skLineSegment(sketch, "E1782", {"start": v(-6.82, 0.4) * mm, "end": v(-6.87, 0.38) * mm});
            skLineSegment(sketch, "E1783", {"start": v(-6.87, 0.38) * mm, "end": v(-6.93, 0.36) * mm});
            skLineSegment(sketch, "E1784", {"start": v(-6.93, 0.36) * mm, "end": v(-6.98, 0.35) * mm});
            skLineSegment(sketch, "E1785", {"start": v(-6.98, 0.35) * mm, "end": v(-7.04, 0.33) * mm});
            skLineSegment(sketch, "E1786", {"start": v(-7.04, 0.33) * mm, "end": v(-7.09, 0.3) * mm});
            skLineSegment(sketch, "E1787", {"start": v(-7.09, 0.3) * mm, "end": v(-7.14, 0.29) * mm});
            skLineSegment(sketch, "E1788", {"start": v(-7.14, 0.29) * mm, "end": v(-7.2, 0.27) * mm});
            skLineSegment(sketch, "E1789", {"start": v(-7.2, 0.27) * mm, "end": v(-7.25, 0.25) * mm});
            skLineSegment(sketch, "E1790", {"start": v(-7.25, 0.25) * mm, "end": v(-7.3, 0.23) * mm});
            skLineSegment(sketch, "E1791", {"start": v(-7.3, 0.23) * mm, "end": v(-7.36, 0.2) * mm});
            skLineSegment(sketch, "E1792", {"start": v(-7.36, 0.2) * mm, "end": v(-7.42, 0.18) * mm});
            skLineSegment(sketch, "E1793", {"start": v(-7.42, 0.18) * mm, "end": v(-7.47, 0.16) * mm});
            skLineSegment(sketch, "E1794", {"start": v(-7.47, 0.16) * mm, "end": v(-7.48, 0.15) * mm});
            skLineSegment(sketch, "E1795", {"start": v(-7.48, 0.15) * mm, "end": v(-7.48, -0.11) * mm});
            skLineSegment(sketch, "E1796", {"start": v(-7.48, -0.11) * mm, "end": v(-7.46, -0.12) * mm});
            skLineSegment(sketch, "E1797", {"start": v(-7.46, -0.12) * mm, "end": v(-7.4, -0.15) * mm});
            skLineSegment(sketch, "E1798", {"start": v(-7.4, -0.15) * mm, "end": v(-7.35, -0.18) * mm});
            skLineSegment(sketch, "E1799", {"start": v(-7.35, -0.18) * mm, "end": v(-7.3, -0.2) * mm});
            skLineSegment(sketch, "E1800", {"start": v(-7.3, -0.2) * mm, "end": v(-7.24, -0.23) * mm});
            skLineSegment(sketch, "E1801", {"start": v(-7.24, -0.23) * mm, "end": v(-7.2, -0.25) * mm});
            skLineSegment(sketch, "E1802", {"start": v(-7.2, -0.25) * mm, "end": v(-7.14, -0.28) * mm});
            skLineSegment(sketch, "E1803", {"start": v(-7.14, -0.28) * mm, "end": v(-7.08, -0.3) * mm});
            skLineSegment(sketch, "E1804", {"start": v(-7.08, -0.3) * mm, "end": v(-7.03, -0.32) * mm});
            skLineSegment(sketch, "E1805", {"start": v(-7.03, -0.32) * mm, "end": v(-6.97, -0.34) * mm});
            skLineSegment(sketch, "E1806", {"start": v(-6.97, -0.34) * mm, "end": v(-6.92, -0.36) * mm});
            skLineSegment(sketch, "E1807", {"start": v(-6.92, -0.36) * mm, "end": v(-6.87, -0.38) * mm});
            skLineSegment(sketch, "E1808", {"start": v(-6.87, -0.38) * mm, "end": v(-6.81, -0.4) * mm});
            skLineSegment(sketch, "E1809", {"start": v(-6.81, -0.4) * mm, "end": v(-6.76, -0.41) * mm});
            skLineSegment(sketch, "E1810", {"start": v(-6.76, -0.41) * mm, "end": v(-6.7, -0.43) * mm});
            skLineSegment(sketch, "E1811", {"start": v(-6.7, -0.43) * mm, "end": v(-6.65, -0.44) * mm});
            skLineSegment(sketch, "E1812", {"start": v(-6.65, -0.44) * mm, "end": v(-6.6, -0.46) * mm});
            skLineSegment(sketch, "E1813", {"start": v(-6.6, -0.46) * mm, "end": v(-6.54, -0.47) * mm});
            skLineSegment(sketch, "E1814", {"start": v(-6.54, -0.47) * mm, "end": v(-6.49, -0.48) * mm});
            skLineSegment(sketch, "E1815", {"start": v(-6.49, -0.48) * mm, "end": v(-6.43, -0.5) * mm});
            skLineSegment(sketch, "E1816", {"start": v(-6.43, -0.5) * mm, "end": v(-6.38, -0.5) * mm});
            skLineSegment(sketch, "E1817", {"start": v(-6.38, -0.5) * mm, "end": v(-6.32, -0.51) * mm});
            skLineSegment(sketch, "E1818", {"start": v(-6.32, -0.51) * mm, "end": v(-6.27, -0.52) * mm});
            skLineSegment(sketch, "E1819", {"start": v(-6.27, -0.52) * mm, "end": v(-6.21, -0.53) * mm});
            skLineSegment(sketch, "E1820", {"start": v(-6.21, -0.53) * mm, "end": v(-6.16, -0.54) * mm});
            skLineSegment(sketch, "E1821", {"start": v(-6.16, -0.54) * mm, "end": v(-6.1, -0.54) * mm});
            skLineSegment(sketch, "E1822", {"start": v(-6.1, -0.54) * mm, "end": v(-6.05, -0.55) * mm});
            skLineSegment(sketch, "E1823", {"start": v(-6.05, -0.55) * mm, "end": v(-6, -0.55) * mm});
            skLineSegment(sketch, "E1824", {"start": v(-6, -0.55) * mm, "end": v(-5.94, -0.55) * mm});
            skLineSegment(sketch, "E1825", {"start": v(-5.94, -0.55) * mm, "end": v(-5.89, -0.55) * mm});
            skLineSegment(sketch, "E1826", {"start": v(-5.89, -0.55) * mm, "end": v(-5.83, -0.55) * mm});
            skLineSegment(sketch, "E1827", {"start": v(-5.83, -0.55) * mm, "end": v(-5.78, -0.55) * mm});
            skLineSegment(sketch, "E1828", {"start": v(-1.34, -8.1) * mm, "end": v(-1.38, -8) * mm});
            skLineSegment(sketch, "E1829", {"start": v(-1.38, -8) * mm, "end": v(-1.42, -7.9) * mm});
            skLineSegment(sketch, "E1830", {"start": v(-1.42, -7.9) * mm, "end": v(-1.46, -7.8) * mm});
            skLineSegment(sketch, "E1831", {"start": v(-1.46, -7.8) * mm, "end": v(-1.5, -7.7) * mm});
            skLineSegment(sketch, "E1832", {"start": v(-1.5, -7.7) * mm, "end": v(-1.54, -7.6) * mm});
            skLineSegment(sketch, "E1833", {"start": v(-1.54, -7.6) * mm, "end": v(-1.57, -7.49) * mm});
            skLineSegment(sketch, "E1834", {"start": v(-1.57, -7.49) * mm, "end": v(-1.6, -7.39) * mm});
            skLineSegment(sketch, "E1835", {"start": v(-1.6, -7.39) * mm, "end": v(-1.64, -7.28) * mm});
            skLineSegment(sketch, "E1836", {"start": v(-1.64, -7.28) * mm, "end": v(-1.67, -7.18) * mm});
            skLineSegment(sketch, "E1837", {"start": v(-1.67, -7.18) * mm, "end": v(-1.7, -7.08) * mm});
            skLineSegment(sketch, "E1838", {"start": v(-1.7, -7.08) * mm, "end": v(-1.73, -6.98) * mm});
            skLineSegment(sketch, "E1839", {"start": v(-1.73, -6.98) * mm, "end": v(-1.75, -6.88) * mm});
            skLineSegment(sketch, "E1840", {"start": v(-1.75, -6.88) * mm, "end": v(-1.78, -6.77) * mm});
            skLineSegment(sketch, "E1841", {"start": v(-1.78, -6.77) * mm, "end": v(-1.8, -6.67) * mm});
            skLineSegment(sketch, "E1842", {"start": v(-1.8, -6.67) * mm, "end": v(-1.83, -6.57) * mm});
            skLineSegment(sketch, "E1843", {"start": v(-1.83, -6.57) * mm, "end": v(-1.85, -6.47) * mm});
            skLineSegment(sketch, "E1844", {"start": v(-1.85, -6.47) * mm, "end": v(-1.87, -6.36) * mm});
            skLineSegment(sketch, "E1845", {"start": v(-1.87, -6.36) * mm, "end": v(-1.89, -6.26) * mm});
            skLineSegment(sketch, "E1846", {"start": v(-1.89, -6.26) * mm, "end": v(-1.9, -6.16) * mm});
            skLineSegment(sketch, "E1847", {"start": v(-1.9, -6.16) * mm, "end": v(-1.92, -6.05) * mm});
            skLineSegment(sketch, "E1848", {"start": v(-1.92, -6.05) * mm, "end": v(-1.93, -5.95) * mm});
            skLineSegment(sketch, "E1849", {"start": v(-1.93, -5.95) * mm, "end": v(-1.94, -5.85) * mm});
            skLineSegment(sketch, "E1850", {"start": v(-1.94, -5.85) * mm, "end": v(-1.95, -5.74) * mm});
            skLineSegment(sketch, "E1851", {"start": v(-1.95, -5.74) * mm, "end": v(-1.96, -5.64) * mm});
            skLineSegment(sketch, "E1852", {"start": v(-1.96, -5.64) * mm, "end": v(-1.97, -5.54) * mm});
            skLineSegment(sketch, "E1853", {"start": v(-1.97, -5.54) * mm, "end": v(-1.98, -5.43) * mm});
            skLineSegment(sketch, "E1854", {"start": v(-1.98, -5.43) * mm, "end": v(-1.98, -5.33) * mm});
            skLineSegment(sketch, "E1855", {"start": v(-1.98, -5.33) * mm, "end": v(-1.99, -5.22) * mm});
            skLineSegment(sketch, "E1856", {"start": v(-1.99, -5.22) * mm, "end": v(-1.99, -5.12) * mm});
            skLineSegment(sketch, "E1857", {"start": v(-1.99, -5.12) * mm, "end": v(-2, -5.02) * mm});
            skLineSegment(sketch, "E1858", {"start": v(-2, -5.02) * mm, "end": v(-1.99, -4.91) * mm});
            skLineSegment(sketch, "E1859", {"start": v(-1.99, -4.91) * mm, "end": v(-1.99, -4.81) * mm});
            skLineSegment(sketch, "E1860", {"start": v(-1.99, -4.81) * mm, "end": v(-1.98, -4.7) * mm});
            skLineSegment(sketch, "E1861", {"start": v(-1.98, -4.7) * mm, "end": v(-1.98, -4.6) * mm});
            skLineSegment(sketch, "E1862", {"start": v(-1.98, -4.6) * mm, "end": v(-1.97, -4.5) * mm});
            skLineSegment(sketch, "E1863", {"start": v(-1.97, -4.5) * mm, "end": v(-1.96, -4.4) * mm});
            skLineSegment(sketch, "E1864", {"start": v(-1.96, -4.4) * mm, "end": v(-1.96, -4.3) * mm});
            skLineSegment(sketch, "E1865", {"start": v(-1.96, -4.3) * mm, "end": v(-1.94, -4.2) * mm});
            skLineSegment(sketch, "E1866", {"start": v(-1.94, -4.2) * mm, "end": v(-1.93, -4.1) * mm});
            skLineSegment(sketch, "E1867", {"start": v(-1.93, -4.1) * mm, "end": v(-1.92, -4) * mm});
            skLineSegment(sketch, "E1868", {"start": v(-1.92, -4) * mm, "end": v(-1.9, -3.9) * mm});
            skLineSegment(sketch, "E1869", {"start": v(-1.9, -3.9) * mm, "end": v(-1.89, -3.8) * mm});
            skLineSegment(sketch, "E1870", {"start": v(-1.89, -3.8) * mm, "end": v(-1.87, -3.69) * mm});
            skLineSegment(sketch, "E1871", {"start": v(-1.87, -3.69) * mm, "end": v(-1.85, -3.59) * mm});
            skLineSegment(sketch, "E1872", {"start": v(-1.85, -3.59) * mm, "end": v(-1.83, -3.49) * mm});
            skLineSegment(sketch, "E1873", {"start": v(-1.83, -3.49) * mm, "end": v(-1.8, -3.38) * mm});
            skLineSegment(sketch, "E1874", {"start": v(-1.8, -3.38) * mm, "end": v(-1.79, -3.28) * mm});
            skLineSegment(sketch, "E1875", {"start": v(-1.79, -3.28) * mm, "end": v(-1.76, -3.18) * mm});
            skLineSegment(sketch, "E1876", {"start": v(-1.76, -3.18) * mm, "end": v(-1.73, -3.08) * mm});
            skLineSegment(sketch, "E1877", {"start": v(-1.73, -3.08) * mm, "end": v(-1.7, -2.98) * mm});
            skLineSegment(sketch, "E1878", {"start": v(-1.7, -2.98) * mm, "end": v(-1.68, -2.88) * mm});
            skLineSegment(sketch, "E1879", {"start": v(-1.68, -2.88) * mm, "end": v(-1.65, -2.78) * mm});
            skLineSegment(sketch, "E1880", {"start": v(-1.65, -2.78) * mm, "end": v(-1.62, -2.68) * mm});
            skLineSegment(sketch, "E1881", {"start": v(-1.62, -2.68) * mm, "end": v(-1.58, -2.58) * mm});
            skLineSegment(sketch, "E1882", {"start": v(-1.58, -2.58) * mm, "end": v(-1.55, -2.48) * mm});
            skLineSegment(sketch, "E1883", {"start": v(-1.55, -2.48) * mm, "end": v(-1.51, -2.38) * mm});
            skLineSegment(sketch, "E1884", {"start": v(-1.51, -2.38) * mm, "end": v(-1.48, -2.28) * mm});
            skLineSegment(sketch, "E1885", {"start": v(-1.48, -2.28) * mm, "end": v(-1.44, -2.18) * mm});
            skLineSegment(sketch, "E1886", {"start": v(-1.44, -2.18) * mm, "end": v(-1.4, -2.08) * mm});
            skLineSegment(sketch, "E1887", {"start": v(-1.4, -2.08) * mm, "end": v(-1.38, -2.03) * mm});
            skLineSegment(sketch, "E1888", {"start": v(-1.38, -2.03) * mm, "end": v(-1.45, -2) * mm});
            skLineSegment(sketch, "E1889", {"start": v(-1.45, -2) * mm, "end": v(-1.57, -1.96) * mm});
            skLineSegment(sketch, "E1890", {"start": v(-1.57, -1.96) * mm, "end": v(-1.7, -1.9) * mm});
            skLineSegment(sketch, "E1891", {"start": v(-1.7, -1.9) * mm, "end": v(-1.81, -1.85) * mm});
            skLineSegment(sketch, "E1892", {"start": v(-1.81, -1.85) * mm, "end": v(-1.93, -1.78) * mm});
            skLineSegment(sketch, "E1893", {"start": v(-1.93, -1.78) * mm, "end": v(-2.03, -1.7) * mm});
            skLineSegment(sketch, "E1894", {"start": v(-2.03, -1.7) * mm, "end": v(-2.14, -1.62) * mm});
            skLineSegment(sketch, "E1895", {"start": v(-2.14, -1.62) * mm, "end": v(-2.24, -1.54) * mm});
            skLineSegment(sketch, "E1896", {"start": v(-2.24, -1.54) * mm, "end": v(-2.33, -1.44) * mm});
            skLineSegment(sketch, "E1897", {"start": v(-2.33, -1.44) * mm, "end": v(-2.42, -1.34) * mm});
            skLineSegment(sketch, "E1898", {"start": v(-2.42, -1.34) * mm, "end": v(-2.5, -1.24) * mm});
            skLineSegment(sketch, "E1899", {"start": v(-2.5, -1.24) * mm, "end": v(-2.58, -1.13) * mm});
            skLineSegment(sketch, "E1900", {"start": v(-2.58, -1.13) * mm, "end": v(-2.64, -1.02) * mm});
            skLineSegment(sketch, "E1901", {"start": v(-2.64, -1.02) * mm, "end": v(-2.7, -0.9) * mm});
            skLineSegment(sketch, "E1902", {"start": v(-2.7, -0.9) * mm, "end": v(-2.76, -0.78) * mm});
            skLineSegment(sketch, "E1903", {"start": v(-2.76, -0.78) * mm, "end": v(-2.8, -0.65) * mm});
            skLineSegment(sketch, "E1904", {"start": v(-2.8, -0.65) * mm, "end": v(-2.83, -0.54) * mm});
            skLineSegment(sketch, "E1905", {"start": v(-2.83, -0.54) * mm, "end": v(-2.87, -0.56) * mm});
            skLineSegment(sketch, "E1906", {"start": v(-2.87, -0.56) * mm, "end": v(-2.97, -0.6) * mm});
            skLineSegment(sketch, "E1907", {"start": v(-2.97, -0.6) * mm, "end": v(-3.07, -0.65) * mm});
            skLineSegment(sketch, "E1908", {"start": v(-3.07, -0.65) * mm, "end": v(-3.17, -0.7) * mm});
            skLineSegment(sketch, "E1909", {"start": v(-3.17, -0.7) * mm, "end": v(-3.27, -0.73) * mm});
            skLineSegment(sketch, "E1910", {"start": v(-3.27, -0.73) * mm, "end": v(-3.37, -0.77) * mm});
            skLineSegment(sketch, "E1911", {"start": v(-3.37, -0.77) * mm, "end": v(-3.47, -0.81) * mm});
            skLineSegment(sketch, "E1912", {"start": v(-3.47, -0.81) * mm, "end": v(-3.57, -0.85) * mm});
            skLineSegment(sketch, "E1913", {"start": v(-3.57, -0.85) * mm, "end": v(-3.68, -0.88) * mm});
            skLineSegment(sketch, "E1914", {"start": v(-3.68, -0.88) * mm, "end": v(-3.78, -0.92) * mm});
            skLineSegment(sketch, "E1915", {"start": v(-3.78, -0.92) * mm, "end": v(-3.88, -0.95) * mm});
            skLineSegment(sketch, "E1916", {"start": v(-3.88, -0.95) * mm, "end": v(-3.98, -0.98) * mm});
            skLineSegment(sketch, "E1917", {"start": v(-3.98, -0.98) * mm, "end": v(-4.08, -1) * mm});
            skLineSegment(sketch, "E1918", {"start": v(-4.08, -1) * mm, "end": v(-4.18, -1.04) * mm});
            skLineSegment(sketch, "E1919", {"start": v(-4.18, -1.04) * mm, "end": v(-4.28, -1.06) * mm});
            skLineSegment(sketch, "E1920", {"start": v(-4.28, -1.06) * mm, "end": v(-4.38, -1.09) * mm});
            skLineSegment(sketch, "E1921", {"start": v(-4.38, -1.09) * mm, "end": v(-4.48, -1.1) * mm});
            skLineSegment(sketch, "E1922", {"start": v(-4.48, -1.1) * mm, "end": v(-4.59, -1.13) * mm});
            skLineSegment(sketch, "E1923", {"start": v(-4.59, -1.13) * mm, "end": v(-4.69, -1.15) * mm});
            skLineSegment(sketch, "E1924", {"start": v(-4.69, -1.15) * mm, "end": v(-4.79, -1.16) * mm});
            skLineSegment(sketch, "E1925", {"start": v(-4.79, -1.16) * mm, "end": v(-4.9, -1.18) * mm});
            skLineSegment(sketch, "E1926", {"start": v(-4.9, -1.18) * mm, "end": v(-5, -1.2) * mm});
            skLineSegment(sketch, "E1927", {"start": v(-5, -1.2) * mm, "end": v(-5.1, -1.2) * mm});
            skLineSegment(sketch, "E1928", {"start": v(-5.1, -1.2) * mm, "end": v(-5.2, -1.22) * mm});
            skLineSegment(sketch, "E1929", {"start": v(-5.2, -1.22) * mm, "end": v(-5.3, -1.23) * mm});
            skLineSegment(sketch, "E1930", {"start": v(-5.3, -1.23) * mm, "end": v(-5.4, -1.23) * mm});
            skLineSegment(sketch, "E1931", {"start": v(-5.4, -1.23) * mm, "end": v(-5.5, -1.24) * mm});
            skLineSegment(sketch, "E1932", {"start": v(-5.5, -1.24) * mm, "end": v(-5.6, -1.24) * mm});
            skLineSegment(sketch, "E1933", {"start": v(-5.6, -1.24) * mm, "end": v(-5.7, -1.25) * mm});
            skLineSegment(sketch, "E1934", {"start": v(-5.7, -1.25) * mm, "end": v(-5.81, -1.25) * mm});
            skLineSegment(sketch, "E1935", {"start": v(-5.81, -1.25) * mm, "end": v(-5.92, -1.25) * mm});
            skLineSegment(sketch, "E1936", {"start": v(-5.92, -1.25) * mm, "end": v(-6.02, -1.24) * mm});
            skLineSegment(sketch, "E1937", {"start": v(-6.02, -1.24) * mm, "end": v(-6.12, -1.24) * mm});
            skLineSegment(sketch, "E1938", {"start": v(-6.12, -1.24) * mm, "end": v(-6.23, -1.23) * mm});
            skLineSegment(sketch, "E1939", {"start": v(-6.23, -1.23) * mm, "end": v(-6.33, -1.23) * mm});
            skLineSegment(sketch, "E1940", {"start": v(-6.33, -1.23) * mm, "end": v(-6.44, -1.22) * mm});
            skLineSegment(sketch, "E1941", {"start": v(-6.44, -1.22) * mm, "end": v(-6.54, -1.2) * mm});
            skLineSegment(sketch, "E1942", {"start": v(-6.54, -1.2) * mm, "end": v(-6.64, -1.2) * mm});
            skLineSegment(sketch, "E1943", {"start": v(-6.64, -1.2) * mm, "end": v(-6.75, -1.18) * mm});
            skLineSegment(sketch, "E1944", {"start": v(-6.75, -1.18) * mm, "end": v(-6.85, -1.16) * mm});
            skLineSegment(sketch, "E1945", {"start": v(-6.85, -1.16) * mm, "end": v(-6.95, -1.14) * mm});
            skLineSegment(sketch, "E1946", {"start": v(-6.95, -1.14) * mm, "end": v(-7.06, -1.13) * mm});
            skLineSegment(sketch, "E1947", {"start": v(-7.06, -1.13) * mm, "end": v(-7.16, -1.1) * mm});
            skLineSegment(sketch, "E1948", {"start": v(-7.16, -1.1) * mm, "end": v(-7.26, -1.08) * mm});
            skLineSegment(sketch, "E1949", {"start": v(-7.26, -1.08) * mm, "end": v(-7.36, -1.06) * mm});
            skLineSegment(sketch, "E1950", {"start": v(-7.36, -1.06) * mm, "end": v(-7.47, -1.03) * mm});
            skLineSegment(sketch, "E1951", {"start": v(-7.47, -1.03) * mm, "end": v(-7.57, -1) * mm});
            skLineSegment(sketch, "E1952", {"start": v(-7.57, -1) * mm, "end": v(-7.67, -0.97) * mm});
            skLineSegment(sketch, "E1953", {"start": v(-7.67, -0.97) * mm, "end": v(-7.77, -0.94) * mm});
            skLineSegment(sketch, "E1954", {"start": v(-7.77, -0.94) * mm, "end": v(-7.88, -0.9) * mm});
            skLineSegment(sketch, "E1955", {"start": v(-7.88, -0.9) * mm, "end": v(-7.98, -0.87) * mm});
            skLineSegment(sketch, "E1956", {"start": v(-7.98, -0.87) * mm, "end": v(-8.08, -0.84) * mm});
            skLineSegment(sketch, "E1957", {"start": v(-8.08, -0.84) * mm, "end": v(-8.18, -0.8) * mm});
            skLineSegment(sketch, "E1958", {"start": v(-8.18, -0.8) * mm, "end": v(-8.28, -0.76) * mm});
            skLineSegment(sketch, "E1959", {"start": v(-8.28, -0.76) * mm, "end": v(-8.39, -0.72) * mm});
            skLineSegment(sketch, "E1960", {"start": v(-8.39, -0.72) * mm, "end": v(-8.49, -0.68) * mm});
            skLineSegment(sketch, "E1961", {"start": v(-8.49, -0.68) * mm, "end": v(-8.59, -0.63) * mm});
            skLineSegment(sketch, "E1962", {"start": v(-8.59, -0.63) * mm, "end": v(-8.7, -0.59) * mm});
            skLineSegment(sketch, "E1963", {"start": v(-8.7, -0.59) * mm, "end": v(-8.8, -0.54) * mm});
            skLineSegment(sketch, "E1964", {"start": v(-8.8, -0.54) * mm, "end": v(-8.9, -0.49) * mm});
            skLineSegment(sketch, "E1965", {"start": v(-8.9, -0.49) * mm, "end": v(-8.96, -0.46) * mm});
            skLineSegment(sketch, "E1966", {"start": v(-8.96, -0.46) * mm, "end": v(-8.95, -0.51) * mm});
            skLineSegment(sketch, "E1967", {"start": v(-8.95, -0.51) * mm, "end": v(-8.9, -1.02) * mm});
            skLineSegment(sketch, "E1968", {"start": v(-8.9, -1.02) * mm, "end": v(-8.82, -1.53) * mm});
            skLineSegment(sketch, "E1969", {"start": v(-8.82, -1.53) * mm, "end": v(-8.71, -2.03) * mm});
            skLineSegment(sketch, "E1970", {"start": v(-8.71, -2.03) * mm, "end": v(-8.57, -2.53) * mm});
            skLineSegment(sketch, "E1971", {"start": v(-8.57, -2.53) * mm, "end": v(-8.4, -3) * mm});
            skLineSegment(sketch, "E1972", {"start": v(-8.4, -3) * mm, "end": v(-8.2, -3.48) * mm});
            skLineSegment(sketch, "E1973", {"start": v(-8.2, -3.48) * mm, "end": v(-7.96, -3.94) * mm});
            skLineSegment(sketch, "E1974", {"start": v(-7.96, -3.94) * mm, "end": v(-7.7, -4.38) * mm});
            skLineSegment(sketch, "E1975", {"start": v(-7.7, -4.38) * mm, "end": v(-7.4, -4.8) * mm});
            skLineSegment(sketch, "E1976", {"start": v(-7.4, -4.8) * mm, "end": v(-7.1, -5.21) * mm});
            skLineSegment(sketch, "E1977", {"start": v(-7.1, -5.21) * mm, "end": v(-6.75, -5.6) * mm});
            skLineSegment(sketch, "E1978", {"start": v(-6.75, -5.6) * mm, "end": v(-6.4, -5.96) * mm});
            skLineSegment(sketch, "E1979", {"start": v(-6.4, -5.96) * mm, "end": v(-6, -6.3) * mm});
            skLineSegment(sketch, "E1980", {"start": v(-6, -6.3) * mm, "end": v(-5.6, -6.61) * mm});
            skLineSegment(sketch, "E1981", {"start": v(-5.6, -6.61) * mm, "end": v(-5.18, -6.9) * mm});
            skLineSegment(sketch, "E1982", {"start": v(-5.18, -6.9) * mm, "end": v(-4.73, -7.16) * mm});
            skLineSegment(sketch, "E1983", {"start": v(-4.73, -7.16) * mm, "end": v(-4.28, -7.4) * mm});
            skLineSegment(sketch, "E1984", {"start": v(-4.28, -7.4) * mm, "end": v(-3.8, -7.6) * mm});
            skLineSegment(sketch, "E1985", {"start": v(-3.8, -7.6) * mm, "end": v(-3.32, -7.77) * mm});
            skLineSegment(sketch, "E1986", {"start": v(-3.32, -7.77) * mm, "end": v(-2.83, -7.92) * mm});
            skLineSegment(sketch, "E1987", {"start": v(-2.83, -7.92) * mm, "end": v(-2.33, -8.03) * mm});
            skLineSegment(sketch, "E1988", {"start": v(-2.33, -8.03) * mm, "end": v(-1.82, -8.1) * mm});
            skLineSegment(sketch, "E1989", {"start": v(-1.82, -8.1) * mm, "end": v(-1.31, -8.16) * mm});
            skLineSegment(sketch, "E1990", {"start": v(-1.31, -8.16) * mm, "end": v(-1.34, -8.1) * mm});
            skLineSegment(sketch, "E1991", {"start": v(-0.28, -8.16) * mm, "end": v(0.23, -8.1) * mm});
            skLineSegment(sketch, "E1992", {"start": v(0.23, -8.1) * mm, "end": v(0.74, -8.03) * mm});
            skLineSegment(sketch, "E1993", {"start": v(0.74, -8.03) * mm, "end": v(1.24, -7.92) * mm});
            skLineSegment(sketch, "E1994", {"start": v(1.24, -7.92) * mm, "end": v(1.73, -7.77) * mm});
            skLineSegment(sketch, "E1995", {"start": v(1.73, -7.77) * mm, "end": v(2.21, -7.6) * mm});
            skLineSegment(sketch, "E1996", {"start": v(2.21, -7.6) * mm, "end": v(2.68, -7.4) * mm});
            skLineSegment(sketch, "E1997", {"start": v(2.68, -7.4) * mm, "end": v(3.14, -7.16) * mm});
            skLineSegment(sketch, "E1998", {"start": v(3.14, -7.16) * mm, "end": v(3.58, -6.9) * mm});
            skLineSegment(sketch, "E1999", {"start": v(3.58, -6.9) * mm, "end": v(4, -6.61) * mm});
            skLineSegment(sketch, "E2000", {"start": v(4, -6.61) * mm, "end": v(4.41, -6.3) * mm});
            skLineSegment(sketch, "E2001", {"start": v(4.41, -6.3) * mm, "end": v(4.8, -5.96) * mm});
            skLineSegment(sketch, "E2002", {"start": v(4.8, -5.96) * mm, "end": v(5.16, -5.6) * mm});
            skLineSegment(sketch, "E2003", {"start": v(5.16, -5.6) * mm, "end": v(5.5, -5.21) * mm});
            skLineSegment(sketch, "E2004", {"start": v(5.5, -5.21) * mm, "end": v(5.82, -4.8) * mm});
            skLineSegment(sketch, "E2005", {"start": v(5.82, -4.8) * mm, "end": v(6.1, -4.38) * mm});
            skLineSegment(sketch, "E2006", {"start": v(6.1, -4.38) * mm, "end": v(6.37, -3.94) * mm});
            skLineSegment(sketch, "E2007", {"start": v(6.37, -3.94) * mm, "end": v(6.6, -3.48) * mm});
            skLineSegment(sketch, "E2008", {"start": v(6.6, -3.48) * mm, "end": v(6.8, -3) * mm});
            skLineSegment(sketch, "E2009", {"start": v(6.8, -3) * mm, "end": v(6.98, -2.53) * mm});
            skLineSegment(sketch, "E2010", {"start": v(6.98, -2.53) * mm, "end": v(7.12, -2.03) * mm});
            skLineSegment(sketch, "E2011", {"start": v(7.12, -2.03) * mm, "end": v(7.23, -1.53) * mm});
            skLineSegment(sketch, "E2012", {"start": v(7.23, -1.53) * mm, "end": v(7.31, -1.02) * mm});
            skLineSegment(sketch, "E2013", {"start": v(7.31, -1.02) * mm, "end": v(7.36, -0.52) * mm});
            skLineSegment(sketch, "E2014", {"start": v(7.36, -0.52) * mm, "end": v(7.3, -0.54) * mm});
            skLineSegment(sketch, "E2015", {"start": v(7.3, -0.54) * mm, "end": v(7.2, -0.58) * mm});
            skLineSegment(sketch, "E2016", {"start": v(7.2, -0.58) * mm, "end": v(7.1, -0.63) * mm});
            skLineSegment(sketch, "E2017", {"start": v(7.1, -0.63) * mm, "end": v(7, -0.67) * mm});
            skLineSegment(sketch, "E2018", {"start": v(7, -0.67) * mm, "end": v(6.9, -0.7) * mm});
            skLineSegment(sketch, "E2019", {"start": v(6.9, -0.7) * mm, "end": v(6.8, -0.74) * mm});
            skLineSegment(sketch, "E2020", {"start": v(6.8, -0.74) * mm, "end": v(6.7, -0.78) * mm});
            skLineSegment(sketch, "E2021", {"start": v(6.7, -0.78) * mm, "end": v(6.6, -0.8) * mm});
            skLineSegment(sketch, "E2022", {"start": v(6.6, -0.8) * mm, "end": v(6.49, -0.84) * mm});
            skLineSegment(sketch, "E2023", {"start": v(6.49, -0.84) * mm, "end": v(6.39, -0.87) * mm});
            skLineSegment(sketch, "E2024", {"start": v(6.39, -0.87) * mm, "end": v(6.28, -0.9) * mm});
            skLineSegment(sketch, "E2025", {"start": v(6.28, -0.9) * mm, "end": v(6.18, -0.93) * mm});
            skLineSegment(sketch, "E2026", {"start": v(6.18, -0.93) * mm, "end": v(6.08, -0.96) * mm});
            skLineSegment(sketch, "E2027", {"start": v(6.08, -0.96) * mm, "end": v(5.98, -0.98) * mm});
            skLineSegment(sketch, "E2028", {"start": v(5.98, -0.98) * mm, "end": v(5.87, -1) * mm});
            skLineSegment(sketch, "E2029", {"start": v(5.87, -1) * mm, "end": v(5.77, -1.03) * mm});
            skLineSegment(sketch, "E2030", {"start": v(5.77, -1.03) * mm, "end": v(5.67, -1.05) * mm});
            skLineSegment(sketch, "E2031", {"start": v(5.67, -1.05) * mm, "end": v(5.57, -1.07) * mm});
            skLineSegment(sketch, "E2032", {"start": v(5.57, -1.07) * mm, "end": v(5.46, -1.09) * mm});
            skLineSegment(sketch, "E2033", {"start": v(5.46, -1.09) * mm, "end": v(5.36, -1.1) * mm});
            skLineSegment(sketch, "E2034", {"start": v(5.36, -1.1) * mm, "end": v(5.26, -1.12) * mm});
            skLineSegment(sketch, "E2035", {"start": v(5.26, -1.12) * mm, "end": v(5.15, -1.14) * mm});
            skLineSegment(sketch, "E2036", {"start": v(5.15, -1.14) * mm, "end": v(5.05, -1.15) * mm});
            skLineSegment(sketch, "E2037", {"start": v(5.05, -1.15) * mm, "end": v(4.95, -1.16) * mm});
            skLineSegment(sketch, "E2038", {"start": v(4.95, -1.16) * mm, "end": v(4.84, -1.17) * mm});
            skLineSegment(sketch, "E2039", {"start": v(4.84, -1.17) * mm, "end": v(4.74, -1.18) * mm});
            skLineSegment(sketch, "E2040", {"start": v(4.74, -1.18) * mm, "end": v(4.64, -1.18) * mm});
            skLineSegment(sketch, "E2041", {"start": v(4.64, -1.18) * mm, "end": v(4.53, -1.19) * mm});
            skLineSegment(sketch, "E2042", {"start": v(4.53, -1.19) * mm, "end": v(4.43, -1.2) * mm});
            skLineSegment(sketch, "E2043", {"start": v(4.43, -1.2) * mm, "end": v(4.32, -1.2) * mm});
            skLineSegment(sketch, "E2044", {"start": v(4.32, -1.2) * mm, "end": v(4.22, -1.2) * mm});
            skLineSegment(sketch, "E2045", {"start": v(4.22, -1.2) * mm, "end": v(4.12, -1.2) * mm});
            skLineSegment(sketch, "E2046", {"start": v(4.12, -1.2) * mm, "end": v(4.02, -1.2) * mm});
            skLineSegment(sketch, "E2047", {"start": v(4.02, -1.2) * mm, "end": v(3.91, -1.19) * mm});
            skLineSegment(sketch, "E2048", {"start": v(3.91, -1.19) * mm, "end": v(3.81, -1.18) * mm});
            skLineSegment(sketch, "E2049", {"start": v(3.81, -1.18) * mm, "end": v(3.7, -1.18) * mm});
            skLineSegment(sketch, "E2050", {"start": v(3.7, -1.18) * mm, "end": v(3.6, -1.17) * mm});
            skLineSegment(sketch, "E2051", {"start": v(3.6, -1.17) * mm, "end": v(3.5, -1.16) * mm});
            skLineSegment(sketch, "E2052", {"start": v(3.5, -1.16) * mm, "end": v(3.4, -1.15) * mm});
            skLineSegment(sketch, "E2053", {"start": v(3.4, -1.15) * mm, "end": v(3.3, -1.14) * mm});
            skLineSegment(sketch, "E2054", {"start": v(3.3, -1.14) * mm, "end": v(3.2, -1.12) * mm});
            skLineSegment(sketch, "E2055", {"start": v(3.2, -1.12) * mm, "end": v(3.1, -1.1) * mm});
            skLineSegment(sketch, "E2056", {"start": v(3.1, -1.1) * mm, "end": v(3, -1.1) * mm});
            skLineSegment(sketch, "E2057", {"start": v(3, -1.1) * mm, "end": v(2.9, -1.07) * mm});
            skLineSegment(sketch, "E2058", {"start": v(2.9, -1.07) * mm, "end": v(2.8, -1.06) * mm});
            skLineSegment(sketch, "E2059", {"start": v(2.8, -1.06) * mm, "end": v(2.7, -1.03) * mm});
            skLineSegment(sketch, "E2060", {"start": v(2.7, -1.03) * mm, "end": v(2.59, -1.01) * mm});
            skLineSegment(sketch, "E2061", {"start": v(2.59, -1.01) * mm, "end": v(2.49, -0.99) * mm});
            skLineSegment(sketch, "E2062", {"start": v(2.49, -0.99) * mm, "end": v(2.39, -0.96) * mm});
            skLineSegment(sketch, "E2063", {"start": v(2.39, -0.96) * mm, "end": v(2.29, -0.94) * mm});
            skLineSegment(sketch, "E2064", {"start": v(2.29, -0.94) * mm, "end": v(2.18, -0.91) * mm});
            skLineSegment(sketch, "E2065", {"start": v(2.18, -0.91) * mm, "end": v(2.08, -0.88) * mm});
            skLineSegment(sketch, "E2066", {"start": v(2.08, -0.88) * mm, "end": v(1.98, -0.85) * mm});
            skLineSegment(sketch, "E2067", {"start": v(1.98, -0.85) * mm, "end": v(1.88, -0.82) * mm});
            skLineSegment(sketch, "E2068", {"start": v(1.88, -0.82) * mm, "end": v(1.78, -0.79) * mm});
            skLineSegment(sketch, "E2069", {"start": v(1.78, -0.79) * mm, "end": v(1.68, -0.75) * mm});
            skLineSegment(sketch, "E2070", {"start": v(1.68, -0.75) * mm, "end": v(1.58, -0.72) * mm});
            skLineSegment(sketch, "E2071", {"start": v(1.58, -0.72) * mm, "end": v(1.48, -0.68) * mm});
            skLineSegment(sketch, "E2072", {"start": v(1.48, -0.68) * mm, "end": v(1.38, -0.64) * mm});
            skLineSegment(sketch, "E2073", {"start": v(1.38, -0.64) * mm, "end": v(1.28, -0.6) * mm});
            skLineSegment(sketch, "E2074", {"start": v(1.28, -0.6) * mm, "end": v(1.23, -0.58) * mm});
            skLineSegment(sketch, "E2075", {"start": v(1.23, -0.58) * mm, "end": v(1.2, -0.65) * mm});
            skLineSegment(sketch, "E2076", {"start": v(1.2, -0.65) * mm, "end": v(1.16, -0.78) * mm});
            skLineSegment(sketch, "E2077", {"start": v(1.16, -0.78) * mm, "end": v(1.11, -0.9) * mm});
            skLineSegment(sketch, "E2078", {"start": v(1.11, -0.9) * mm, "end": v(1.05, -1.02) * mm});
            skLineSegment(sketch, "E2079", {"start": v(1.05, -1.02) * mm, "end": v(0.98, -1.13) * mm});
            skLineSegment(sketch, "E2080", {"start": v(0.98, -1.13) * mm, "end": v(0.9, -1.24) * mm});
            skLineSegment(sketch, "E2081", {"start": v(0.9, -1.24) * mm, "end": v(0.83, -1.34) * mm});
            skLineSegment(sketch, "E2082", {"start": v(0.83, -1.34) * mm, "end": v(0.74, -1.44) * mm});
            skLineSegment(sketch, "E2083", {"start": v(0.74, -1.44) * mm, "end": v(0.65, -1.54) * mm});
            skLineSegment(sketch, "E2084", {"start": v(0.65, -1.54) * mm, "end": v(0.55, -1.62) * mm});
            skLineSegment(sketch, "E2085", {"start": v(0.55, -1.62) * mm, "end": v(0.44, -1.7) * mm});
            skLineSegment(sketch, "E2086", {"start": v(0.44, -1.7) * mm, "end": v(0.33, -1.78) * mm});
            skLineSegment(sketch, "E2087", {"start": v(0.33, -1.78) * mm, "end": v(0.22, -1.85) * mm});
            skLineSegment(sketch, "E2088", {"start": v(0.22, -1.85) * mm, "end": v(0.1, -1.9) * mm});
            skLineSegment(sketch, "E2089", {"start": v(0.1, -1.9) * mm, "end": v(-0.02, -1.96) * mm});
            skLineSegment(sketch, "E2090", {"start": v(-0.02, -1.96) * mm, "end": v(-0.14, -2) * mm});
            skLineSegment(sketch, "E2091", {"start": v(-0.14, -2) * mm, "end": v(-0.26, -2.04) * mm});
            skLineSegment(sketch, "E2092", {"start": v(-0.26, -2.04) * mm, "end": v(-0.24, -2.08) * mm});
            skLineSegment(sketch, "E2093", {"start": v(-0.24, -2.08) * mm, "end": v(-0.2, -2.18) * mm});
            skLineSegment(sketch, "E2094", {"start": v(-0.2, -2.18) * mm, "end": v(-0.15, -2.28) * mm});
            skLineSegment(sketch, "E2095", {"start": v(-0.15, -2.28) * mm, "end": v(-0.1, -2.38) * mm});
            skLineSegment(sketch, "E2096", {"start": v(-0.1, -2.38) * mm, "end": v(-0.06, -2.48) * mm});
            skLineSegment(sketch, "E2097", {"start": v(-0.06, -2.48) * mm, "end": v(-0.02, -2.58) * mm});
            skLineSegment(sketch, "E2098", {"start": v(-0.02, -2.58) * mm, "end": v(0.02, -2.68) * mm});
            skLineSegment(sketch, "E2099", {"start": v(0.02, -2.68) * mm, "end": v(0.05, -2.78) * mm});
            skLineSegment(sketch, "E2100", {"start": v(0.05, -2.78) * mm, "end": v(0.09, -2.88) * mm});
            skLineSegment(sketch, "E2101", {"start": v(0.09, -2.88) * mm, "end": v(0.12, -2.98) * mm});
            skLineSegment(sketch, "E2102", {"start": v(0.12, -2.98) * mm, "end": v(0.15, -3.08) * mm});
            skLineSegment(sketch, "E2103", {"start": v(0.15, -3.08) * mm, "end": v(0.18, -3.18) * mm});
            skLineSegment(sketch, "E2104", {"start": v(0.18, -3.18) * mm, "end": v(0.21, -3.28) * mm});
            skLineSegment(sketch, "E2105", {"start": v(0.21, -3.28) * mm, "end": v(0.24, -3.38) * mm});
            skLineSegment(sketch, "E2106", {"start": v(0.24, -3.38) * mm, "end": v(0.27, -3.49) * mm});
            skLineSegment(sketch, "E2107", {"start": v(0.27, -3.49) * mm, "end": v(0.29, -3.59) * mm});
            skLineSegment(sketch, "E2108", {"start": v(0.29, -3.59) * mm, "end": v(0.31, -3.69) * mm});
            skLineSegment(sketch, "E2109", {"start": v(0.31, -3.69) * mm, "end": v(0.33, -3.8) * mm});
            skLineSegment(sketch, "E2110", {"start": v(0.33, -3.8) * mm, "end": v(0.35, -3.9) * mm});
            skLineSegment(sketch, "E2111", {"start": v(0.35, -3.9) * mm, "end": v(0.37, -4) * mm});
            skLineSegment(sketch, "E2112", {"start": v(0.37, -4) * mm, "end": v(0.38, -4.1) * mm});
            skLineSegment(sketch, "E2113", {"start": v(0.38, -4.1) * mm, "end": v(0.4, -4.2) * mm});
            skLineSegment(sketch, "E2114", {"start": v(0.4, -4.2) * mm, "end": v(0.41, -4.3) * mm});
            skLineSegment(sketch, "E2115", {"start": v(0.41, -4.3) * mm, "end": v(0.42, -4.4) * mm});
            skLineSegment(sketch, "E2116", {"start": v(0.42, -4.4) * mm, "end": v(0.43, -4.5) * mm});
            skLineSegment(sketch, "E2117", {"start": v(0.43, -4.5) * mm, "end": v(0.44, -4.6) * mm});
            skLineSegment(sketch, "E2118", {"start": v(0.44, -4.6) * mm, "end": v(0.44, -4.7) * mm});
            skLineSegment(sketch, "E2119", {"start": v(0.44, -4.7) * mm, "end": v(0.45, -4.81) * mm});
            skLineSegment(sketch, "E2120", {"start": v(0.45, -4.81) * mm, "end": v(0.45, -4.91) * mm});
            skLineSegment(sketch, "E2121", {"start": v(0.45, -4.91) * mm, "end": v(0.45, -5.02) * mm});
            skLineSegment(sketch, "E2122", {"start": v(0.45, -5.02) * mm, "end": v(0.45, -5.12) * mm});
            skLineSegment(sketch, "E2123", {"start": v(0.45, -5.12) * mm, "end": v(0.45, -5.22) * mm});
            skLineSegment(sketch, "E2124", {"start": v(0.45, -5.22) * mm, "end": v(0.44, -5.33) * mm});
            skLineSegment(sketch, "E2125", {"start": v(0.44, -5.33) * mm, "end": v(0.44, -5.43) * mm});
            skLineSegment(sketch, "E2126", {"start": v(0.44, -5.43) * mm, "end": v(0.43, -5.54) * mm});
            skLineSegment(sketch, "E2127", {"start": v(0.43, -5.54) * mm, "end": v(0.42, -5.64) * mm});
            skLineSegment(sketch, "E2128", {"start": v(0.42, -5.64) * mm, "end": v(0.41, -5.74) * mm});
            skLineSegment(sketch, "E2129", {"start": v(0.41, -5.74) * mm, "end": v(0.4, -5.85) * mm});
            skLineSegment(sketch, "E2130", {"start": v(0.4, -5.85) * mm, "end": v(0.38, -5.95) * mm});
            skLineSegment(sketch, "E2131", {"start": v(0.38, -5.95) * mm, "end": v(0.37, -6.05) * mm});
            skLineSegment(sketch, "E2132", {"start": v(0.37, -6.05) * mm, "end": v(0.35, -6.16) * mm});
            skLineSegment(sketch, "E2133", {"start": v(0.35, -6.16) * mm, "end": v(0.33, -6.26) * mm});
            skLineSegment(sketch, "E2134", {"start": v(0.33, -6.26) * mm, "end": v(0.3, -6.36) * mm});
            skLineSegment(sketch, "E2135", {"start": v(0.3, -6.36) * mm, "end": v(0.28, -6.47) * mm});
            skLineSegment(sketch, "E2136", {"start": v(0.28, -6.47) * mm, "end": v(0.26, -6.57) * mm});
            skLineSegment(sketch, "E2137", {"start": v(0.26, -6.57) * mm, "end": v(0.23, -6.67) * mm});
            skLineSegment(sketch, "E2138", {"start": v(0.23, -6.67) * mm, "end": v(0.2, -6.77) * mm});
            skLineSegment(sketch, "E2139", {"start": v(0.2, -6.77) * mm, "end": v(0.18, -6.88) * mm});
            skLineSegment(sketch, "E2140", {"start": v(0.18, -6.88) * mm, "end": v(0.15, -6.98) * mm});
            skLineSegment(sketch, "E2141", {"start": v(0.15, -6.98) * mm, "end": v(0.11, -7.08) * mm});
            skLineSegment(sketch, "E2142", {"start": v(0.11, -7.08) * mm, "end": v(0.08, -7.18) * mm});
            skLineSegment(sketch, "E2143", {"start": v(0.08, -7.18) * mm, "end": v(0.04, -7.28) * mm});
            skLineSegment(sketch, "E2144", {"start": v(0.04, -7.28) * mm, "end": v(0, -7.39) * mm});
            skLineSegment(sketch, "E2145", {"start": v(0, -7.39) * mm, "end": v(-0.04, -7.49) * mm});
            skLineSegment(sketch, "E2146", {"start": v(-0.04, -7.49) * mm, "end": v(-0.08, -7.6) * mm});
            skLineSegment(sketch, "E2147", {"start": v(-0.08, -7.6) * mm, "end": v(-0.12, -7.7) * mm});
            skLineSegment(sketch, "E2148", {"start": v(-0.12, -7.7) * mm, "end": v(-0.16, -7.8) * mm});
            skLineSegment(sketch, "E2149", {"start": v(-0.16, -7.8) * mm, "end": v(-0.21, -7.9) * mm});
            skLineSegment(sketch, "E2150", {"start": v(-0.21, -7.9) * mm, "end": v(-0.26, -8) * mm});
            skLineSegment(sketch, "E2151", {"start": v(-0.26, -8) * mm, "end": v(-0.3, -8.1) * mm});
            skLineSegment(sketch, "E2152", {"start": v(-0.3, -8.1) * mm, "end": v(-0.34, -8.16) * mm});
            skLineSegment(sketch, "E2153", {"start": v(-0.34, -8.16) * mm, "end": v(-0.28, -8.16) * mm});
            skLineSegment(sketch, "E2154", {"start": v(-0.68, -6.66) * mm, "end": v(-0.65, -6.61) * mm});
            skLineSegment(sketch, "E2155", {"start": v(-0.65, -6.61) * mm, "end": v(-0.62, -6.56) * mm});
            skLineSegment(sketch, "E2156", {"start": v(-0.62, -6.56) * mm, "end": v(-0.6, -6.5) * mm});
            skLineSegment(sketch, "E2157", {"start": v(-0.6, -6.5) * mm, "end": v(-0.57, -6.45) * mm});
            skLineSegment(sketch, "E2158", {"start": v(-0.57, -6.45) * mm, "end": v(-0.54, -6.4) * mm});
            skLineSegment(sketch, "E2159", {"start": v(-0.54, -6.4) * mm, "end": v(-0.52, -6.34) * mm});
            skLineSegment(sketch, "E2160", {"start": v(-0.52, -6.34) * mm, "end": v(-0.5, -6.29) * mm});
            skLineSegment(sketch, "E2161", {"start": v(-0.5, -6.29) * mm, "end": v(-0.48, -6.23) * mm});
            skLineSegment(sketch, "E2162", {"start": v(-0.48, -6.23) * mm, "end": v(-0.46, -6.18) * mm});
            skLineSegment(sketch, "E2163", {"start": v(-0.46, -6.18) * mm, "end": v(-0.44, -6.12) * mm});
            skLineSegment(sketch, "E2164", {"start": v(-0.44, -6.12) * mm, "end": v(-0.42, -6.07) * mm});
            skLineSegment(sketch, "E2165", {"start": v(-0.42, -6.07) * mm, "end": v(-0.4, -6.02) * mm});
            skLineSegment(sketch, "E2166", {"start": v(-0.4, -6.02) * mm, "end": v(-0.38, -5.96) * mm});
            skLineSegment(sketch, "E2167", {"start": v(-0.38, -5.96) * mm, "end": v(-0.37, -5.9) * mm});
            skLineSegment(sketch, "E2168", {"start": v(-0.37, -5.9) * mm, "end": v(-0.35, -5.85) * mm});
            skLineSegment(sketch, "E2169", {"start": v(-0.35, -5.85) * mm, "end": v(-0.34, -5.8) * mm});
            skLineSegment(sketch, "E2170", {"start": v(-0.34, -5.8) * mm, "end": v(-0.32, -5.74) * mm});
            skLineSegment(sketch, "E2171", {"start": v(-0.32, -5.74) * mm, "end": v(-0.31, -5.69) * mm});
            skLineSegment(sketch, "E2172", {"start": v(-0.31, -5.69) * mm, "end": v(-0.3, -5.64) * mm});
            skLineSegment(sketch, "E2173", {"start": v(-0.3, -5.64) * mm, "end": v(-0.3, -5.58) * mm});
            skLineSegment(sketch, "E2174", {"start": v(-0.3, -5.58) * mm, "end": v(-0.28, -5.53) * mm});
            skLineSegment(sketch, "E2175", {"start": v(-0.28, -5.53) * mm, "end": v(-0.27, -5.47) * mm});
            skLineSegment(sketch, "E2176", {"start": v(-0.27, -5.47) * mm, "end": v(-0.27, -5.42) * mm});
            skLineSegment(sketch, "E2177", {"start": v(-0.27, -5.42) * mm, "end": v(-0.26, -5.36) * mm});
            skLineSegment(sketch, "E2178", {"start": v(-0.26, -5.36) * mm, "end": v(-0.26, -5.3) * mm});
            skLineSegment(sketch, "E2179", {"start": v(-0.26, -5.3) * mm, "end": v(-0.25, -5.25) * mm});
            skLineSegment(sketch, "E2180", {"start": v(-0.25, -5.25) * mm, "end": v(-0.25, -5.2) * mm});
            skLineSegment(sketch, "E2181", {"start": v(-0.25, -5.2) * mm, "end": v(-0.24, -5.14) * mm});
            skLineSegment(sketch, "E2182", {"start": v(-0.24, -5.14) * mm, "end": v(-0.24, -5.09) * mm});
            skLineSegment(sketch, "E2183", {"start": v(-0.24, -5.09) * mm, "end": v(-0.24, -5.03) * mm});
            skLineSegment(sketch, "E2184", {"start": v(-0.24, -5.03) * mm, "end": v(-0.24, -4.98) * mm});
            skLineSegment(sketch, "E2185", {"start": v(-0.24, -4.98) * mm, "end": v(-0.24, -4.93) * mm});
            skLineSegment(sketch, "E2186", {"start": v(-0.24, -4.93) * mm, "end": v(-0.25, -4.87) * mm});
            skLineSegment(sketch, "E2187", {"start": v(-0.25, -4.87) * mm, "end": v(-0.25, -4.82) * mm});
            skLineSegment(sketch, "E2188", {"start": v(-0.25, -4.82) * mm, "end": v(-0.25, -4.76) * mm});
            skLineSegment(sketch, "E2189", {"start": v(-0.25, -4.76) * mm, "end": v(-0.26, -4.71) * mm});
            skLineSegment(sketch, "E2190", {"start": v(-0.26, -4.71) * mm, "end": v(-0.27, -4.66) * mm});
            skLineSegment(sketch, "E2191", {"start": v(-0.27, -4.66) * mm, "end": v(-0.27, -4.6) * mm});
            skLineSegment(sketch, "E2192", {"start": v(-0.27, -4.6) * mm, "end": v(-0.28, -4.55) * mm});
            skLineSegment(sketch, "E2193", {"start": v(-0.28, -4.55) * mm, "end": v(-0.3, -4.5) * mm});
            skLineSegment(sketch, "E2194", {"start": v(-0.3, -4.5) * mm, "end": v(-0.3, -4.44) * mm});
            skLineSegment(sketch, "E2195", {"start": v(-0.3, -4.44) * mm, "end": v(-0.31, -4.39) * mm});
            skLineSegment(sketch, "E2196", {"start": v(-0.31, -4.39) * mm, "end": v(-0.32, -4.34) * mm});
            skLineSegment(sketch, "E2197", {"start": v(-0.32, -4.34) * mm, "end": v(-0.34, -4.28) * mm});
            skLineSegment(sketch, "E2198", {"start": v(-0.34, -4.28) * mm, "end": v(-0.35, -4.23) * mm});
            skLineSegment(sketch, "E2199", {"start": v(-0.35, -4.23) * mm, "end": v(-0.36, -4.17) * mm});
            skLineSegment(sketch, "E2200", {"start": v(-0.36, -4.17) * mm, "end": v(-0.38, -4.12) * mm});
            skLineSegment(sketch, "E2201", {"start": v(-0.38, -4.12) * mm, "end": v(-0.4, -4.07) * mm});
            skLineSegment(sketch, "E2202", {"start": v(-0.4, -4.07) * mm, "end": v(-0.41, -4.01) * mm});
            skLineSegment(sketch, "E2203", {"start": v(-0.41, -4.01) * mm, "end": v(-0.43, -3.96) * mm});
            skLineSegment(sketch, "E2204", {"start": v(-0.43, -3.96) * mm, "end": v(-0.45, -3.9) * mm});
            skLineSegment(sketch, "E2205", {"start": v(-0.45, -3.9) * mm, "end": v(-0.47, -3.85) * mm});
            skLineSegment(sketch, "E2206", {"start": v(-0.47, -3.85) * mm, "end": v(-0.5, -3.8) * mm});
            skLineSegment(sketch, "E2207", {"start": v(-0.5, -3.8) * mm, "end": v(-0.51, -3.75) * mm});
            skLineSegment(sketch, "E2208", {"start": v(-0.51, -3.75) * mm, "end": v(-0.54, -3.7) * mm});
            skLineSegment(sketch, "E2209", {"start": v(-0.54, -3.7) * mm, "end": v(-0.56, -3.64) * mm});
            skLineSegment(sketch, "E2210", {"start": v(-0.56, -3.64) * mm, "end": v(-0.58, -3.59) * mm});
            skLineSegment(sketch, "E2211", {"start": v(-0.58, -3.59) * mm, "end": v(-0.61, -3.53) * mm});
            skLineSegment(sketch, "E2212", {"start": v(-0.61, -3.53) * mm, "end": v(-0.64, -3.48) * mm});
            skLineSegment(sketch, "E2213", {"start": v(-0.64, -3.48) * mm, "end": v(-0.66, -3.43) * mm});
            skLineSegment(sketch, "E2214", {"start": v(-0.66, -3.43) * mm, "end": v(-0.67, -3.41) * mm});
            skLineSegment(sketch, "E2215", {"start": v(-0.67, -3.41) * mm, "end": v(-0.96, -3.41) * mm});
            skLineSegment(sketch, "E2216", {"start": v(-0.96, -3.41) * mm, "end": v(-0.96, -3.42) * mm});
            skLineSegment(sketch, "E2217", {"start": v(-0.96, -3.42) * mm, "end": v(-0.99, -3.47) * mm});
            skLineSegment(sketch, "E2218", {"start": v(-0.99, -3.47) * mm, "end": v(-1, -3.53) * mm});
            skLineSegment(sketch, "E2219", {"start": v(-1, -3.53) * mm, "end": v(-1.03, -3.58) * mm});
            skLineSegment(sketch, "E2220", {"start": v(-1.03, -3.58) * mm, "end": v(-1.05, -3.63) * mm});
            skLineSegment(sketch, "E2221", {"start": v(-1.05, -3.63) * mm, "end": v(-1.07, -3.69) * mm});
            skLineSegment(sketch, "E2222", {"start": v(-1.07, -3.69) * mm, "end": v(-1.1, -3.74) * mm});
            skLineSegment(sketch, "E2223", {"start": v(-1.1, -3.74) * mm, "end": v(-1.11, -3.8) * mm});
            skLineSegment(sketch, "E2224", {"start": v(-1.11, -3.8) * mm, "end": v(-1.13, -3.85) * mm});
            skLineSegment(sketch, "E2225", {"start": v(-1.13, -3.85) * mm, "end": v(-1.15, -3.9) * mm});
            skLineSegment(sketch, "E2226", {"start": v(-1.15, -3.9) * mm, "end": v(-1.16, -3.95) * mm});
            skLineSegment(sketch, "E2227", {"start": v(-1.16, -3.95) * mm, "end": v(-1.18, -4) * mm});
            skLineSegment(sketch, "E2228", {"start": v(-1.18, -4) * mm, "end": v(-1.2, -4.06) * mm});
            skLineSegment(sketch, "E2229", {"start": v(-1.2, -4.06) * mm, "end": v(-1.2, -4.12) * mm});
            skLineSegment(sketch, "E2230", {"start": v(-1.2, -4.12) * mm, "end": v(-1.22, -4.17) * mm});
            skLineSegment(sketch, "E2231", {"start": v(-1.22, -4.17) * mm, "end": v(-1.23, -4.22) * mm});
            skLineSegment(sketch, "E2232", {"start": v(-1.23, -4.22) * mm, "end": v(-1.25, -4.28) * mm});
            skLineSegment(sketch, "E2233", {"start": v(-1.25, -4.28) * mm, "end": v(-1.26, -4.33) * mm});
            skLineSegment(sketch, "E2234", {"start": v(-1.26, -4.33) * mm, "end": v(-1.27, -4.38) * mm});
            skLineSegment(sketch, "E2235", {"start": v(-1.27, -4.38) * mm, "end": v(-1.28, -4.44) * mm});
            skLineSegment(sketch, "E2236", {"start": v(-1.28, -4.44) * mm, "end": v(-1.28, -4.5) * mm});
            skLineSegment(sketch, "E2237", {"start": v(-1.28, -4.5) * mm, "end": v(-1.3, -4.55) * mm});
            skLineSegment(sketch, "E2238", {"start": v(-1.3, -4.55) * mm, "end": v(-1.3, -4.6) * mm});
            skLineSegment(sketch, "E2239", {"start": v(-1.3, -4.6) * mm, "end": v(-1.3, -4.65) * mm});
            skLineSegment(sketch, "E2240", {"start": v(-1.3, -4.65) * mm, "end": v(-1.31, -4.7) * mm});
            skLineSegment(sketch, "E2241", {"start": v(-1.31, -4.7) * mm, "end": v(-1.32, -4.76) * mm});
            skLineSegment(sketch, "E2242", {"start": v(-1.32, -4.76) * mm, "end": v(-1.32, -4.82) * mm});
            skLineSegment(sketch, "E2243", {"start": v(-1.32, -4.82) * mm, "end": v(-1.32, -4.87) * mm});
            skLineSegment(sketch, "E2244", {"start": v(-1.32, -4.87) * mm, "end": v(-1.32, -4.93) * mm});
            skLineSegment(sketch, "E2245", {"start": v(-1.32, -4.93) * mm, "end": v(-1.33, -4.98) * mm});
            skLineSegment(sketch, "E2246", {"start": v(-1.33, -4.98) * mm, "end": v(-1.33, -5.03) * mm});
            skLineSegment(sketch, "E2247", {"start": v(-1.33, -5.03) * mm, "end": v(-1.32, -5.09) * mm});
            skLineSegment(sketch, "E2248", {"start": v(-1.32, -5.09) * mm, "end": v(-1.32, -5.15) * mm});
            skLineSegment(sketch, "E2249", {"start": v(-1.32, -5.15) * mm, "end": v(-1.32, -5.2) * mm});
            skLineSegment(sketch, "E2250", {"start": v(-1.32, -5.2) * mm, "end": v(-1.32, -5.26) * mm});
            skLineSegment(sketch, "E2251", {"start": v(-1.32, -5.26) * mm, "end": v(-1.31, -5.31) * mm});
            skLineSegment(sketch, "E2252", {"start": v(-1.31, -5.31) * mm, "end": v(-1.31, -5.37) * mm});
            skLineSegment(sketch, "E2253", {"start": v(-1.31, -5.37) * mm, "end": v(-1.3, -5.42) * mm});
            skLineSegment(sketch, "E2254", {"start": v(-1.3, -5.42) * mm, "end": v(-1.3, -5.48) * mm});
            skLineSegment(sketch, "E2255", {"start": v(-1.3, -5.48) * mm, "end": v(-1.3, -5.53) * mm});
            skLineSegment(sketch, "E2256", {"start": v(-1.3, -5.53) * mm, "end": v(-1.28, -5.58) * mm});
            skLineSegment(sketch, "E2257", {"start": v(-1.28, -5.58) * mm, "end": v(-1.27, -5.64) * mm});
            skLineSegment(sketch, "E2258", {"start": v(-1.27, -5.64) * mm, "end": v(-1.27, -5.7) * mm});
            skLineSegment(sketch, "E2259", {"start": v(-1.27, -5.7) * mm, "end": v(-1.25, -5.75) * mm});
            skLineSegment(sketch, "E2260", {"start": v(-1.25, -5.75) * mm, "end": v(-1.24, -5.8) * mm});
            skLineSegment(sketch, "E2261", {"start": v(-1.24, -5.8) * mm, "end": v(-1.23, -5.86) * mm});
            skLineSegment(sketch, "E2262", {"start": v(-1.23, -5.86) * mm, "end": v(-1.22, -5.91) * mm});
            skLineSegment(sketch, "E2263", {"start": v(-1.22, -5.91) * mm, "end": v(-1.2, -5.97) * mm});
            skLineSegment(sketch, "E2264", {"start": v(-1.2, -5.97) * mm, "end": v(-1.2, -6.02) * mm});
            skLineSegment(sketch, "E2265", {"start": v(-1.2, -6.02) * mm, "end": v(-1.17, -6.08) * mm});
            skLineSegment(sketch, "E2266", {"start": v(-1.17, -6.08) * mm, "end": v(-1.16, -6.13) * mm});
            skLineSegment(sketch, "E2267", {"start": v(-1.16, -6.13) * mm, "end": v(-1.14, -6.19) * mm});
            skLineSegment(sketch, "E2268", {"start": v(-1.14, -6.19) * mm, "end": v(-1.12, -6.24) * mm});
            skLineSegment(sketch, "E2269", {"start": v(-1.12, -6.24) * mm, "end": v(-1.1, -6.3) * mm});
            skLineSegment(sketch, "E2270", {"start": v(-1.1, -6.3) * mm, "end": v(-1.09, -6.35) * mm});
            skLineSegment(sketch, "E2271", {"start": v(-1.09, -6.35) * mm, "end": v(-1.07, -6.4) * mm});
            skLineSegment(sketch, "E2272", {"start": v(-1.07, -6.4) * mm, "end": v(-1.04, -6.46) * mm});
            skLineSegment(sketch, "E2273", {"start": v(-1.04, -6.46) * mm, "end": v(-1.02, -6.51) * mm});
            skLineSegment(sketch, "E2274", {"start": v(-1.02, -6.51) * mm, "end": v(-1, -6.57) * mm});
            skLineSegment(sketch, "E2275", {"start": v(-1, -6.57) * mm, "end": v(-0.98, -6.62) * mm});
            skLineSegment(sketch, "E2276", {"start": v(-0.98, -6.62) * mm, "end": v(-0.95, -6.67) * mm});
            skLineSegment(sketch, "E2277", {"start": v(-0.95, -6.67) * mm, "end": v(-0.95, -6.68) * mm});
            skLineSegment(sketch, "E2278", {"start": v(-0.95, -6.68) * mm, "end": v(-0.68, -6.68) * mm});
            skLineSegment(sketch, "E2279", {"start": v(-0.68, -6.68) * mm, "end": v(-0.68, -6.66) * mm});
            skPoint(sketch, "E2280", {"position": v(-0.8, 0) * mm});
            skCircle(sketch, "E2281", {"center": v(-0.8, 0) * mm, "radius": 1.5 * mm});
            skLineSegment(sketch, "E2282", {"start": v(-1.91, -1) * mm, "end": v(0.32, -1) * mm});
            skPoint(sketch, "E2283", {"position": v(-0.8, -1) * mm});
            skCircle(sketch, "E2284", {"center": v(-0.8, 0) * mm, "radius": 2.88 * mm});
            skSolve(sketch);
        }
        {
            var Q0;
            Q0=makeQuery(id+"F0.imprint","IMPRINT",FACE,{"disambiguationData":[TD([[makeQuery(id+"F0.imprint","IMPRINT",EDGE,{"derivedFrom":sQuery(id+"F0.wireOp",EDGE,"E0")}),1.0]])]});
            var Q1;
            {var subQ11=sQuery(id+"F0.wireOp",EDGE,"E1177");Q1=makeQuery(id+"F0.imprint","IMPRINT",FACE,{"disambiguationData":[TD([[makeQuery(id+"F0.imprint","IMPRINT",EDGE,{"derivedFrom":subQ11}),-1.0]])]});}
            var Q2;
            {var subQ0=sQuery(id+"F0.wireOp",EDGE,"E2282");Q2=makeQuery(id+"F0.imprint","IMPRINT",FACE,{"disambiguationData":[TD([[makeQuery(id+"F0.imprint","IMPRINT",EDGE,{"derivedFrom":subQ0}),-1.0]])]});}
            var Q3;
            {var subQ0=sQuery(id+"F0.wireOp",EDGE,"E2068");Q3=makeQuery(id+"F0.imprint","IMPRINT",FACE,{"disambiguationData":[TD([[makeQuery(id+"F0.imprint","IMPRINT",EDGE,{"derivedFrom":subQ0}),1.0]])]});}
            var Q4;
            {var subQ0=sQuery(id+"F0.wireOp",EDGE,"E1364");Q4=makeQuery(id+"F0.imprint","IMPRINT",FACE,{"disambiguationData":[TD([[makeQuery(id+"F0.imprint","IMPRINT",EDGE,{"derivedFrom":subQ0}),1.0]])]});}
            var Q5;
            {var subQ0=sQuery(id+"F0.wireOp",EDGE,"E1177");Q5=makeQuery(id+"F0.imprint","IMPRINT",FACE,{"disambiguationData":[TD([[makeQuery(id+"F0.imprint","IMPRINT",EDGE,{"derivedFrom":subQ0}),1.0]])]});}
            var Q6;
            {var subQ1=sQuery(id+"F0.wireOp",EDGE,"E1881");Q6=makeQuery(id+"F0.imprint","IMPRINT",FACE,{"disambiguationData":[TD([[makeQuery(id+"F0.imprint","IMPRINT",EDGE,{"derivedFrom":subQ1}),1.0]])]});}
            extrude(context, id + "F1", {"entities" : qUnion([Q0, Q1, Q2, Q3, Q4, Q5, Q6]), "depth" : 5 * mm});
        }
    });
